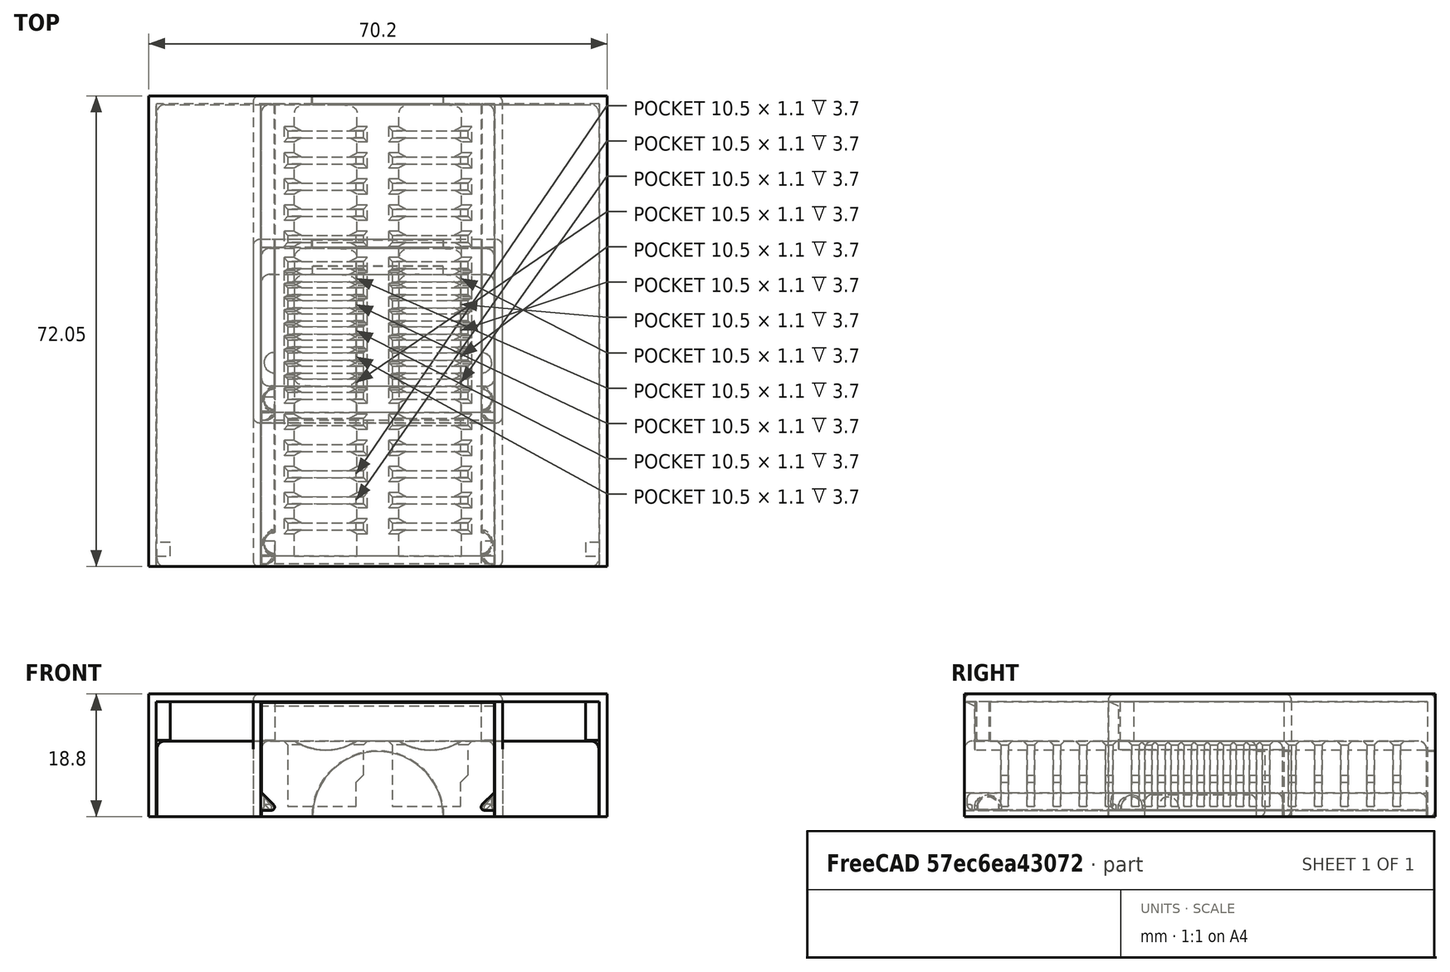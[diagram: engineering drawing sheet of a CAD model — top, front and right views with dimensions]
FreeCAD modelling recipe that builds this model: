
FCSTD DOCUMENT  (FreeCAD 1.0R39109 (Git))
Label: MicroSDHolder
License: All rights reserved
LicenseURL: http://en.wikipedia.org/wiki/All_rights_reserved
objects: Sketcher::SketchObject×55, PartDesign::Pad×27, PartDesign::Pocket×18, PartDesign::Fillet×16, PartDesign::Chamfer×7, PartDesign::Body×7, PartDesign::SubShapeBinder×6, PartDesign::Plane×4, PartDesign::LinearPattern×4, App::Part×3, PartDesign::ShapeBinder×2, Spreadsheet::Sheet×1
note: 341 computed .brp shape members not serialized (recipe doc carries the construction recipe); baked Part::Feature solids carry a one-line shape summary decoded from their .brp

FEATURE [Spreadsheet::Sheet] Spreadsheet
  cells = B3='Tolerance; C3(Tolerance)==0.1 mm; B4='BaseHeight; C4(BaseHeight)==SDOffset + SDHeight - SDFree; B5='WallThickness; C5(WallThickness)==1.2 mm; B6='BackWallThickness; C6(BackWallThickness)==1.6 mm; B7='SDHoleWidth; C7(SDHoleWidth)==11.6 mm; B8='SDHoleWidthSrinkage; C8(SDHoleWidthSrinkage)==1 mm; B9='SDHoleThickness; C9(SDHoleThickness)==1.1 mm; B10='SDHeight; C10(SDHeight)==15 mm; B11='SDFree; C11(SDFree)==5 mm; B12='SDOffset; C12(SDOffset)==1.6 mm; B13='SpacingX; C13(SpacingX)==16 mm; B14='SpacingY; C14(SpacingY)==4 mm; B15='Margin; C15(Margin)==4 mm; B16='Columns_4; C16(Columns_4)=4; B17='Columns_2; C17(Columns_2)=2; B18='Rows; C18(Rows)=16; B19='Rows_short; C19(Rows_short)=5; B20='Rows_test; C20(Rows_test)=3; B21='RidgeDepth; C21(RidgeDepth)==2 mm; B22='RidgeOffset; C22(RidgeOffset)==1 mm; B23='LockRadius; C23(LockRadius)==1.6 mm
FEATURE [Sketcher::SketchObject] Sketch  label="Template_XY"
  ArcFitTolerance = 0
  AttachmentSupport = -> [XY_Plane]
  FullyConstrained = true
  MakeInternals = false
  MapMode = 5
  expr: .Constraints.BaseLength = <<Spreadsheet>>.SpacingY * (<<Spreadsheet>>.Rows - 1) + <<Spreadsheet>>.SDHoleThickness + 2 * <<Spreadsheet>>.Margin
  expr: .Constraints.Width = <<Spreadsheet>>.SpacingX * (<<Spreadsheet>>.Columns_4 - 1) + <<Spreadsheet>>.SDHoleWidth + 2 * <<Spreadsheet>>.Margin
  expr: Constraints[42] = <<Spreadsheet>>.LockRadius
  expr: Constraints[43] = <<Spreadsheet>>.LockRadius + <<Spreadsheet>>.Tolerance
  expr: Constraints[55] = <<Spreadsheet>>.Tolerance * 1.5
  expr: Constraints[59] = <<Spreadsheet>>.BackWallThickness
  expr: Constraints[64] = <<Spreadsheet>>.RidgeDepth
  expr: Constraints[67] = <<Spreadsheet>>.Tolerance
  sketch-geometry (22):
    g0: LineSegment StartX=33.8 StartY=34.55 StartZ=0 EndX=33.8 EndY=-36.15 EndZ=0
    g1: LineSegment StartX=33.8 StartY=-36.15 StartZ=0 EndX=-33.8 EndY=-36.15 EndZ=0
    g2: LineSegment StartX=-33.8 StartY=-36.15 StartZ=0 EndX=-33.8 EndY=34.55 EndZ=0
    g3: LineSegment StartX=-33.8 StartY=-6.2e-15 StartZ=0 EndX=33.8 EndY=-6.2e-15 EndZ=0
    g4: LineSegment StartX=-2.3e-15 StartY=34.55 StartZ=0 EndX=-2.3e-15 EndY=-36.15 EndZ=0
    g5: LineSegment StartX=-33.8 StartY=34.55 StartZ=0 EndX=-31.8 EndY=34.55 EndZ=0
    g6: LineSegment StartX=-31.8 StartY=34.55 StartZ=0 EndX=31.8 EndY=34.55 EndZ=0
    g7: ArcOfCircle CenterX=-31.8 CenterY=-32.55 CenterZ=0 NormalX=0 NormalY=0 NormalZ=1 AngleXU=0 Radius=1.6 StartAngle=1.5708 EndAngle=4.71239
    g8: LineSegment StartX=-31.8 StartY=-36.15 StartZ=0 EndX=-31.8 EndY=34.55 EndZ=0
    g9: ArcOfCircle CenterX=-31.8 CenterY=-32.55 CenterZ=0 NormalX=0 NormalY=0 NormalZ=1 AngleXU=0 Radius=1.7 StartAngle=1.5708 EndAngle=4.71239
    g10: LineSegment StartX=31.8 StartY=34.55 StartZ=0 EndX=31.8 EndY=-36.15 EndZ=0
    g11: ArcOfCircle CenterX=31.8 CenterY=-32.55 CenterZ=0 NormalX=0 NormalY=0 NormalZ=1 AngleXU=0 Radius=1.6 StartAngle=4.71239 EndAngle=7.85398
    g12: ArcOfCircle CenterX=31.8 CenterY=-32.55 CenterZ=0 NormalX=0 NormalY=0 NormalZ=1 AngleXU=0 Radius=1.7 StartAngle=4.71239 EndAngle=7.85398
    g13: LineSegment [constr] StartX=-31.8 StartY=-32.55 StartZ=0 EndX=31.8 EndY=-32.55 EndZ=0
    g14: LineSegment StartX=31.8 StartY=34.55 StartZ=0 EndX=33.8 EndY=34.55 EndZ=0
    g15: LineSegment StartX=-33.9 StartY=-36.15 StartZ=0 EndX=-33.9 EndY=34.7 EndZ=0
    g16: LineSegment StartX=-33.9 StartY=34.7 StartZ=0 EndX=33.9 EndY=34.7 EndZ=0
    g17: LineSegment StartX=33.9 StartY=34.7 StartZ=0 EndX=33.9 EndY=-36.15 EndZ=0
    g18: LineSegment [constr] StartX=33.8 StartY=-36.15 StartZ=0 EndX=33.9 EndY=-36.15 EndZ=0
    g19: LineSegment [constr] StartX=33.8 StartY=34.55 StartZ=0 EndX=33.8 EndY=34.7 EndZ=0
    g20: LineSegment StartX=-33.8 StartY=-34.55 StartZ=0 EndX=33.8 EndY=-34.55 EndZ=0
    g21: LineSegment [constr] StartX=-33.8 StartY=-36.15 StartZ=0 EndX=-33.9 EndY=-36.15 EndZ=0
  constraints (70):
    c: Coincident(g0,g1)
    c: Coincident(g1,g2)
    c: Coincident(g2,g5)
    c: Horizontal(g1)
    c: Vertical(g0)
    c: Vertical(g2)
    c: DistanceX(g5,g0) = 67.6  'Width'
    c: PointOnObject(g3,g2)
    c: PointOnObject(g3,g0)
    c: PointOnObject(g4,g1)
    c: Symmetric(g1,g0,g4)
    c: Coincident(g5,g6)
    c: Horizontal(g5)
    c: PointOnObject(g4,g6)
    c: Coincident(g8,g5)
    c: Vertical(g8)
    c: PointOnObject(g7,g8)
    c: PointOnObject(g7,g8)
    c: Coincident(g9,g7)
    c: PointOnObject(g9,g8)
    c: Vertical(g10)
    c: PointOnObject(g11,g10)
    c: PointOnObject(g11,g10)
    c: Coincident(g12,g11)
    c: PointOnObject(g12,g10)
    c: Equal(g7,g11)
    c: Equal(g12,g9)
    c: PointOnObject(g8,g1)
    c: PointOnObject(g9,g8)
    c: PointOnObject(g7,g8)
    c: DistanceY(g8,g7) = 2
    c: PointOnObject(g10,g1)
    c: PointOnObject(g12,g10)
    c: PointOnObject(g11,g10)
    c: Coincident(g13,g7)
    c: Coincident(g13,g11)
    c: Horizontal(g13)
    c: Coincident(g6,g10)
    c: Coincident(g14,g6)
    c: Coincident(g14,g0)
    c: Horizontal(g14)
    c: Symmetric(g5,g6,g4)
    c: Radius(g7) = 1.6
    c: Radius(g9) = 1.7
    c: Vertical(g15)
    c: Coincident(g15,g16)
    c: Horizontal(g16)
    c: Coincident(g16,g17)
    c: Vertical(g17)
    c: PointOnObject(g17,g1)
    c: Coincident(g18,g0)
    c: PointOnObject(g15,g1)
    c: Coincident(g19,g0)
    c: PointOnObject(g19,g16)
    c: Vertical(g19)
    c: DistanceY(g19,g19) = 0.15
    c: DistanceY(g15,g15) = 70.85  'CoverLength'
    c: PointOnObject(g20,g2)
    c: Horizontal(g20)
    c: DistanceY(g1,g20) = 1.6
    c: Symmetric(g20,g0,g-1)  '__ANCHOR__'
    c: DistanceY(g20,g2) = 69.1  'BaseLength'
    c: Symmetric(g20,g0,g3)
    c: Horizontal(g3)
    c: DistanceX(g1,g8) = 2
    c: Coincident(g21,g1)
    c: Coincident(g21,g15)
    c: DistanceX(g21,g21) = 0.1
    c: Equal(g18,g21)
    c: Coincident(g18,g17)
FEATURE [Sketcher::SketchObject] Sketch001  label="Template_SD"
  ArcFitTolerance = 0
  AttachmentSupport = -> [XZ_Plane]
  ExternalGeometry = -> [Sketch]
  FullyConstrained = true
  MakeInternals = false
  MapMode = 5
  Placement = pos=(0,0,0) rot=(1,0,0;1.5708rad)
  expr: Constraints[70] = <<Spreadsheet>>.SDHeight
  expr: Constraints[71] = <<Spreadsheet>>.SDHoleWidth
  expr: Constraints[74] = <<Spreadsheet>>.SDHoleWidthSrinkage
  expr: Constraints[75] = <<Spreadsheet>>.SDOffset
  expr: Constraints[80] = <<Spreadsheet>>.SDFree
  expr: Constraints[81] = <<Spreadsheet>>.SpacingX
  sketch-geometry (30):
    g0: LineSegment StartX=-13.8 StartY=1.6 StartZ=0 EndX=-13.8 EndY=16.6 EndZ=0
    g1: LineSegment StartX=-13.8 StartY=16.6 StartZ=0 EndX=-2.2 EndY=16.6 EndZ=0
    g2: LineSegment StartX=-2.2 StartY=16.6 StartZ=0 EndX=-2.2 EndY=6.4 EndZ=0
    g3: LineSegment StartX=-3.2 StartY=1.6 StartZ=0 EndX=-13.8 EndY=1.6 EndZ=0
    g4: LineSegment StartX=-3.2 StartY=1.6 StartZ=0 EndX=-3.2 EndY=5.4 EndZ=0
    g5: LineSegment StartX=-3.2 StartY=5.4 StartZ=0 EndX=-2.2 EndY=6.4 EndZ=0
    g6: GeomPoint [constr] X=-1.105e-13 Y=0 Z=0
    g7: LineSegment [constr] StartX=-2.2 StartY=16.6 StartZ=0 EndX=2.2 EndY=16.6 EndZ=0
    g8: LineSegment [constr] StartX=13.8 StartY=16.6 StartZ=0 EndX=18.2 EndY=16.6 EndZ=0
    g9: LineSegment [constr] StartX=-13.8 StartY=16.6 StartZ=0 EndX=-18.2 EndY=16.6 EndZ=0
    g10: LineSegment StartX=2.2 StartY=16.6 StartZ=0 EndX=2.2 EndY=1.6 EndZ=0
    g11: LineSegment StartX=2.2 StartY=1.6 StartZ=0 EndX=12.8 EndY=1.6 EndZ=0
    g12: LineSegment StartX=12.8 StartY=1.6 StartZ=0 EndX=12.8 EndY=5.4 EndZ=0
    g13: LineSegment StartX=12.8 StartY=5.4 StartZ=0 EndX=13.8 EndY=6.4 EndZ=0
    g14: LineSegment StartX=13.8 StartY=6.4 StartZ=0 EndX=13.8 EndY=16.6 EndZ=0
    g15: LineSegment StartX=13.8 StartY=16.6 StartZ=0 EndX=2.2 EndY=16.6 EndZ=0
    g16: LineSegment StartX=18.2 StartY=16.6 StartZ=0 EndX=29.8 EndY=16.6 EndZ=0
    g17: LineSegment StartX=29.8 StartY=16.6 StartZ=0 EndX=29.8 EndY=6.4 EndZ=0
    g18: LineSegment StartX=29.8 StartY=6.4 StartZ=0 EndX=28.8 EndY=5.4 EndZ=0
    g19: LineSegment StartX=28.8 StartY=5.4 StartZ=0 EndX=28.8 EndY=1.6 EndZ=0
    g20: LineSegment StartX=28.8 StartY=1.6 StartZ=0 EndX=18.2 EndY=1.6 EndZ=0
    g21: LineSegment StartX=18.2 StartY=1.6 StartZ=0 EndX=18.2 EndY=16.6 EndZ=0
    g22: LineSegment StartX=-18.2 StartY=16.6 StartZ=0 EndX=-18.2 EndY=6.4 EndZ=0
    g23: LineSegment StartX=-18.2 StartY=6.4 StartZ=0 EndX=-19.2 EndY=5.4 EndZ=0
    g24: LineSegment StartX=-19.2 StartY=5.4 StartZ=0 EndX=-19.2 EndY=1.6 EndZ=0
    g25: LineSegment StartX=-19.2 StartY=1.6 StartZ=0 EndX=-29.8 EndY=1.6 EndZ=0
    g26: LineSegment StartX=-29.8 StartY=1.6 StartZ=0 EndX=-29.8 EndY=16.6 EndZ=0
    g27: LineSegment StartX=-29.8 StartY=16.6 StartZ=0 EndX=-18.2 EndY=16.6 EndZ=0
    g28: LineSegment StartX=-29.8 StartY=11.6 StartZ=0 EndX=29.8 EndY=11.6 EndZ=0
    g29: LineSegment [constr] StartX=-2.3e-15 StartY=16.6 StartZ=0 EndX=-2.3e-15 EndY=0 EndZ=0
  constraints (85):
    c: Coincident(g3,g0)
    c: Coincident(g0,g1)
    c: Coincident(g1,g2)
    c: Horizontal(g1)
    c: Vertical(g0)
    c: Vertical(g2)
    c: Horizontal(g3)
    c: Vertical(g4)
    c: Coincident(g5,g4)
    c: Coincident(g2,g5)
    c: Coincident(g7,g1)
    c: Horizontal(g7)
    c: Horizontal(g8)
    c: Horizontal(g9)
    c: Equal(g9,g7)
    c: Equal(g7,g8)
    c: Coincident(g7,g10)
    c: Vertical(g10)
    c: Coincident(g10,g11)
    c: Horizontal(g11)
    c: Coincident(g11,g12)
    c: Vertical(g12)
    c: Coincident(g12,g13)
    c: Coincident(g13,g14)
    c: Coincident(g14,g8)
    c: Vertical(g14)
    c: Coincident(g14,g15)
    c: Coincident(g15,g10)
    c: Horizontal(g15)
    c: Coincident(g8,g16)
    c: Horizontal(g16)
    c: Coincident(g16,g17)
    c: Vertical(g17)
    c: Coincident(g17,g18)
    c: Coincident(g18,g19)
    c: Vertical(g19)
    c: Coincident(g19,g20)
    c: Horizontal(g20)
    c: Coincident(g20,g21)
    c: Coincident(g21,g16)
    c: Vertical(g21)
    c: Coincident(g9,g0)
    c: Coincident(g9,g22)
    c: Vertical(g22)
    c: Coincident(g22,g23)
    c: Coincident(g23,g24)
    c: Vertical(g24)
    c: Coincident(g24,g25)
    c: Horizontal(g25)
    c: Coincident(g25,g26)
    c: Vertical(g26)
    c: Coincident(g26,g27)
    c: Coincident(g27,g22)
    c: Horizontal(g27)
    c: Equal(g27,g1)
    c: Equal(g1,g15)
    c: Equal(g15,g16)
    c: Equal(g26,g0)
    c: Equal(g0,g10)
    c: Equal(g10,g21)
    c: Equal(g22,g2)
    c: Equal(g2,g14)
    c: Equal(g14,g17)
    c: Equal(g25,g3)
    c: Equal(g3,g11)
    c: Equal(g11,g20)
    c: Equal(g24,g4)
    c: Equal(g4,g12)
    c: Equal(g12,g19)
    c: Coincident(g6,g-1)  '__ANCHOR__'
    c: DistanceY(g26,g26) = 15
    c: DistanceX(g27,g27) = 11.6
    c: Angle(g22,g23) = 2.35619
    c: DistanceY(g24,g22) = 4.8
    c: DistanceX(g24,g22) = 1
    c: DistanceY(g6,g3) = 1.6
    c: Coincident(g3,g4)
    c: PointOnObject(g28,g26)
    c: PointOnObject(g28,g17)
    c: Horizontal(g28)
    c: DistanceY(g28,g26) = 5
    c: DistanceX(g26,g0) = 16
    c: PointOnObject(g29,g7)
    c: Coincident(g-3,g29)
    c: Symmetric(g1,g10,g29)
FEATURE [Sketcher::SketchObject] Sketch002  label="MSHB_Foundation"
  ArcFitTolerance = 0
  AttachmentSupport = -> [XY_Plane]
  ExternalGeometry = -> [Sketch]
  FullyConstrained = true
  MakeInternals = false
  MapMode = 5
  sketch-geometry (4):
    g0: LineSegment StartX=33.8 StartY=34.55 StartZ=0 EndX=33.8 EndY=-36.15 EndZ=0
    g1: LineSegment StartX=33.8 StartY=-36.15 StartZ=0 EndX=-33.8 EndY=-36.15 EndZ=0
    g2: LineSegment StartX=-33.8 StartY=-36.15 StartZ=0 EndX=-33.8 EndY=34.55 EndZ=0
    g3: LineSegment StartX=-33.8 StartY=34.55 StartZ=0 EndX=33.8 EndY=34.55 EndZ=0
  constraints (8):
    c: Coincident(g0,g1)
    c: Coincident(g1,g2)
    c: Coincident(g2,g3)
    c: Coincident(g3,g0)
    c: Coincident(g0,g-4)
    c: Coincident(g0,g-4)
    c: Coincident(g2,g-3)
    c: Coincident(g1,g-3)
FEATURE [PartDesign::Pad] Pad  label="MSHB_Foundation_"
  Direction = (0,0,1)
  Length = 11.6
  Length2 = 10
  Profile = -> Sketch002
  ReferenceAxis = -> Sketch002 [N_Axis]
  Suppressed = false
  Type = 0
  expr: Length = <<Spreadsheet>>.BaseHeight
FEATURE [Sketcher::SketchObject] Sketch003  label="MSHB_SDHoles"
  ArcFitTolerance = 0
  AttachmentOffset = pos=(0,0,30.55) rot=(0,0,1;0rad)
  AttachmentSupport = -> [XZ_Plane]
  ExternalGeometry = -> [Sketch001]
  FullyConstrained = true
  MakeInternals = false
  MapMode = 5
  Placement = pos=(0,-30.55,6.8e-15) rot=(1,0,0;1.5708rad)
  expr: .AttachmentOffset.Base.z = Sketch.Constraints.BaseLength / 2 - <<Spreadsheet>>.Margin
  sketch-geometry (24):
    g0: LineSegment StartX=-29.8 StartY=16.6 StartZ=0 EndX=-18.2 EndY=16.6 EndZ=0
    g1: LineSegment StartX=-18.2 StartY=16.6 StartZ=0 EndX=-18.2 EndY=6.4 EndZ=0
    g2: LineSegment StartX=-18.2 StartY=6.4 StartZ=0 EndX=-19.2 EndY=5.4 EndZ=0
    g3: LineSegment StartX=-19.2 StartY=5.4 StartZ=0 EndX=-19.2 EndY=1.6 EndZ=0
    g4: LineSegment StartX=-19.2 StartY=1.6 StartZ=0 EndX=-29.8 EndY=1.6 EndZ=0
    g5: LineSegment StartX=-29.8 StartY=1.6 StartZ=0 EndX=-29.8 EndY=16.6 EndZ=0
    g6: LineSegment StartX=-13.8 StartY=16.6 StartZ=0 EndX=-2.2 EndY=16.6 EndZ=0
    g7: LineSegment StartX=-2.2 StartY=16.6 StartZ=0 EndX=-2.2 EndY=6.4 EndZ=0
    g8: LineSegment StartX=-2.2 StartY=6.4 StartZ=0 EndX=-3.2 EndY=5.4 EndZ=0
    g9: LineSegment StartX=-3.2 StartY=5.4 StartZ=0 EndX=-3.2 EndY=1.6 EndZ=0
    g10: LineSegment StartX=-3.2 StartY=1.6 StartZ=0 EndX=-13.8 EndY=1.6 EndZ=0
    g11: LineSegment StartX=-13.8 StartY=1.6 StartZ=0 EndX=-13.8 EndY=16.6 EndZ=0
    g12: LineSegment StartX=2.2 StartY=16.6 StartZ=0 EndX=13.8 EndY=16.6 EndZ=0
    g13: LineSegment StartX=13.8 StartY=16.6 StartZ=0 EndX=13.8 EndY=6.4 EndZ=0
    g14: LineSegment StartX=13.8 StartY=6.4 StartZ=0 EndX=12.8 EndY=5.4 EndZ=0
    g15: LineSegment StartX=12.8 StartY=5.4 StartZ=0 EndX=12.8 EndY=1.6 EndZ=0
    g16: LineSegment StartX=12.8 StartY=1.6 StartZ=0 EndX=2.2 EndY=1.6 EndZ=0
    g17: LineSegment StartX=2.2 StartY=1.6 StartZ=0 EndX=2.2 EndY=16.6 EndZ=0
    g18: LineSegment StartX=18.2 StartY=16.6 StartZ=0 EndX=29.8 EndY=16.6 EndZ=0
    g19: LineSegment StartX=29.8 StartY=16.6 StartZ=0 EndX=29.8 EndY=6.4 EndZ=0
    g20: LineSegment StartX=29.8 StartY=6.4 StartZ=0 EndX=28.8 EndY=5.4 EndZ=0
    g21: LineSegment StartX=28.8 StartY=5.4 StartZ=0 EndX=28.8 EndY=1.6 EndZ=0
    g22: LineSegment StartX=28.8 StartY=1.6 StartZ=0 EndX=18.2 EndY=1.6 EndZ=0
    g23: LineSegment StartX=18.2 StartY=1.6 StartZ=0 EndX=18.2 EndY=16.6 EndZ=0
  constraints (48):
    c: Coincident(g-3,g0)
    c: Coincident(g0,g-4)
    c: Coincident(g0,g1)
    c: Coincident(g1,g-4)
    c: Coincident(g1,g2)
    c: Coincident(g2,g-5)
    c: Coincident(g2,g3)
    c: Coincident(g3,g-5)
    c: Coincident(g3,g4)
    c: Coincident(g4,g-3)
    c: Coincident(g4,g5)
    c: Coincident(g5,g0)
    c: Coincident(g-6,g6)
    c: Coincident(g6,g-7)
    c: Coincident(g6,g7)
    c: Coincident(g7,g-7)
    c: Coincident(g7,g8)
    c: Coincident(g8,g-8)
    c: Coincident(g8,g9)
    c: Coincident(g9,g-8)
    c: Coincident(g9,g10)
    c: Coincident(g10,g-6)
    c: Coincident(g10,g11)
    c: Coincident(g11,g6)
    c: Coincident(g-9,g12)
    c: Coincident(g12,g-10)
    c: Coincident(g12,g13)
    c: Coincident(g13,g-10)
    c: Coincident(g13,g14)
    c: Coincident(g14,g-11)
    c: Coincident(g14,g15)
    c: Coincident(g15,g-11)
    c: Coincident(g15,g16)
    c: Coincident(g16,g-9)
    c: Coincident(g16,g17)
    c: Coincident(g12,g17)
    c: Coincident(g-12,g18)
    c: Coincident(g18,g-13)
    c: Coincident(g18,g19)
    c: Coincident(g19,g-13)
    c: Coincident(g19,g20)
    c: Coincident(g20,g-14)
    c: Coincident(g20,g21)
    c: Coincident(g21,g-14)
    c: Coincident(g21,g22)
    c: Coincident(g22,g-12)
    c: Coincident(g22,g23)
    c: Coincident(g23,g18)
FEATURE [Sketcher::SketchObject] Sketch006  label="MSHB_Lock"
  ArcFitTolerance = 0
  AttachmentOffset = pos=(0,0,1) rot=(0,0,1;0rad)
  AttachmentSupport = -> [XY_Plane]
  ExternalGeometry = -> [Sketch]
  FullyConstrained = true
  MakeInternals = false
  MapMode = 5
  Placement = pos=(0,0,1) rot=(0,0,1;0rad)
  expr: .AttachmentOffset.Base.z = <<Spreadsheet>>.RidgeOffset
  sketch-geometry (4):
    g0: ArcOfCircle CenterX=-31.8 CenterY=-32.55 CenterZ=0 NormalX=0 NormalY=0 NormalZ=1 AngleXU=0 Radius=1.6 StartAngle=1.5708 EndAngle=4.71239
    g1: ArcOfCircle CenterX=31.8 CenterY=-32.55 CenterZ=0 NormalX=0 NormalY=0 NormalZ=1 AngleXU=0 Radius=1.6 StartAngle=4.71239 EndAngle=7.85398
    g2: LineSegment StartX=31.8 StartY=-30.95 StartZ=0 EndX=31.8 EndY=-34.15 EndZ=0
    g3: LineSegment StartX=-31.8 StartY=-30.95 StartZ=0 EndX=-31.8 EndY=-34.15 EndZ=0
  constraints (10):
    c: Coincident(g2,g1)
    c: Coincident(g2,g1)
    c: Coincident(g3,g0)
    c: Coincident(g3,g0)
    c: Coincident(g1,g-4)
    c: Coincident(g1,g-4)
    c: Equal(g1,g-4)
    c: Coincident(g0,g-3)
    c: Coincident(g0,g-3)
    c: Equal(g0,g-3)
FEATURE [Sketcher::SketchObject] Sketch011  label="Template_XZ"
  ArcFitTolerance = 0
  AttachmentSupport = -> [XZ_Plane]
  FullyConstrained = true
  MakeInternals = false
  MapMode = 5
  Placement = pos=(0,0,0) rot=(1,0,0;1.5708rad)
  expr: Constraints[12] = <<Spreadsheet>>.Tolerance
  expr: Constraints[26] = <<Spreadsheet>>.RidgeOffset
  expr: Constraints[40] = <<Spreadsheet>>.RidgeDepth
  expr: Constraints[48] = <<Spreadsheet>>.SDOffset + <<Spreadsheet>>.SDHeight + 1 mm
  expr: Constraints[6] = Sketch.Constraints.Width
  expr: Constraints[73] = <<Spreadsheet>>.SDFree + 1 mm
  sketch-geometry (28):
    g0: LineSegment StartX=-33.8 StartY=0 StartZ=0 EndX=33.8 EndY=0 EndZ=0
    g1: LineSegment StartX=33.8 StartY=11.6 StartZ=0 EndX=-33.8 EndY=11.6 EndZ=0
    g2: LineSegment [constr] StartX=-33.8 StartY=0 StartZ=0 EndX=-33.9 EndY=0 EndZ=0
    g3: LineSegment [constr] StartX=33.8 StartY=0 StartZ=0 EndX=33.9 EndY=0 EndZ=0
    g4: LineSegment StartX=-33.8 StartY=1 StartZ=0 EndX=-33.8 EndY=0 EndZ=0
    g5: LineSegment StartX=-33.8 StartY=3 StartZ=0 EndX=-33.8 EndY=1 EndZ=0
    g6: LineSegment StartX=-33.8 StartY=11.6 StartZ=0 EndX=-33.8 EndY=5 EndZ=0
    g7: LineSegment StartX=-33.8 StartY=5 StartZ=0 EndX=-33.8 EndY=3 EndZ=0
    g8: LineSegment StartX=-33.8 StartY=1 StartZ=0 EndX=-31.8 EndY=3 EndZ=0
    g9: LineSegment StartX=-31.8 StartY=3 StartZ=0 EndX=-33.8 EndY=5 EndZ=0
    g10: LineSegment [constr] StartX=-31.8 StartY=3 StartZ=0 EndX=-33.8 EndY=3 EndZ=0
    g11: LineSegment StartX=33.8 StartY=0 StartZ=0 EndX=33.8 EndY=1 EndZ=0
    g12: LineSegment StartX=33.8 StartY=1 StartZ=0 EndX=33.8 EndY=11.6 EndZ=0
    g13: LineSegment StartX=33.8 StartY=1 StartZ=0 EndX=31.8 EndY=3 EndZ=0
    g14: LineSegment StartX=31.8 StartY=3 StartZ=0 EndX=33.8 EndY=5 EndZ=0
    g15: LineSegment [constr] StartX=31.8 StartY=3 StartZ=0 EndX=33.8 EndY=3 EndZ=0
    g16: LineSegment StartX=-33.9 StartY=17.6 StartZ=0 EndX=33.9 EndY=17.6 EndZ=0
    g17: LineSegment StartX=-33.9 StartY=1.04142 StartZ=0 EndX=-31.9414 EndY=3 EndZ=0
    g18: LineSegment StartX=-31.9414 StartY=3 StartZ=0 EndX=-33.9 EndY=4.95858 EndZ=0
    g19: LineSegment [constr] StartX=-33.8 StartY=5 StartZ=0 EndX=-33.8707 EndY=4.92929 EndZ=0
    g20: LineSegment [constr] StartX=-33.8 StartY=1 StartZ=0 EndX=-33.8707 EndY=1.07071 EndZ=0
    g21: LineSegment StartX=33.9 StartY=4.95858 StartZ=0 EndX=31.9414 EndY=3 EndZ=0
    g22: LineSegment StartX=31.9414 StartY=3 StartZ=0 EndX=33.9 EndY=1.04142 EndZ=0
    g23: LineSegment StartX=-33.9 StartY=0 StartZ=0 EndX=-33.9 EndY=1.04142 EndZ=0
    g24: LineSegment StartX=-33.9 StartY=1.04142 StartZ=0 EndX=-33.9 EndY=17.6 EndZ=0
    g25: LineSegment StartX=33.9 StartY=17.6 StartZ=0 EndX=33.9 EndY=1.04142 EndZ=0
    g26: LineSegment StartX=33.9 StartY=1.04142 StartZ=0 EndX=33.9 EndY=0 EndZ=0
    g27: ArcOfCircle CenterX=0 CenterY=0 CenterZ=0 NormalX=0 NormalY=0 NormalZ=1 AngleXU=0 Radius=10 StartAngle=0 EndAngle=3.14159
  constraints (81):
    c: Coincident(g0,g11)
    c: Coincident(g12,g1)
    c: Coincident(g1,g6)
    c: Coincident(g4,g0)
    c: Horizontal(g0)
    c: Horizontal(g1)
    c: DistanceX(g1,g1) = 67.6
    c: Coincident(g2,g0)
    c: Horizontal(g2)
    c: Coincident(g3,g0)
    c: Horizontal(g3)
    c: Equal(g3,g2)
    c: DistanceX(g2,g2) = 0.1
    c: Coincident(g5,g4)
    c: Vertical(g4)
    c: Coincident(g7,g5)
    c: Vertical(g5)
    c: Coincident(g6,g7)
    c: Vertical(g6)
    c: Vertical(g7)
    c: Coincident(g8,g4)
    c: Coincident(g9,g6)
    c: Coincident(g10,g5)
    c: Horizontal(g10)
    c: Equal(g10,g7)
    c: Equal(g7,g5)
    c: DistanceY(g4,g4) = 1
    c: Coincident(g11,g12)
    c: Vertical(g11)
    c: Vertical(g12)
    c: Equal(g4,g11)
    c: Coincident(g11,g13)
    c: Coincident(g13,g14)
    c: PointOnObject(g14,g12)
    c: Coincident(g13,g15)
    c: PointOnObject(g15,g12)
    c: Horizontal(g15)
    c: Equal(g14,g13)
    c: Equal(g13,g8)
    c: Equal(g10,g15)
    c: DistanceX(g6,g8) = 2
    c: Coincident(g8,g9)
    c: Coincident(g8,g10)
    c: Coincident(g2,g23)
    c: Coincident(g24,g16)
    c: Horizontal(g16)
    c: Coincident(g16,g25)
    c: Coincident(g26,g3)
    c: DistanceY(g23,g24) = 17.6
    c: PointOnObject(g17,g10)
    c: Coincident(g18,g17)
    c: Coincident(g19,g6)
    c: PointOnObject(g19,g18)
    c: Coincident(g20,g4)
    c: PointOnObject(g20,g17)
    c: Perpendicular(g20,g17)
    c: Perpendicular(g9,g19)
    c: Equal(g2,g20)
    c: PointOnObject(g21,g15)
    c: Coincident(g21,g22)
    c: Equal(g21,g22)
    c: Equal(g22,g17)
    c: Coincident(g23,g24)
    c: Vertical(g23)
    c: Vertical(g24)
    c: PointOnObject(g18,g24)
    c: Coincident(g23,g17)
    c: Coincident(g25,g26)
    c: Vertical(g25)
    c: Vertical(g26)
    c: PointOnObject(g21,g25)
    c: Coincident(g22,g25)
    c: Equal(g26,g23)
    c: DistanceY(g1,g16) = 6
    c: Parallel(g17,g8)
    c: Parallel(g18,g9)
    c: PointOnObject(g27,g0)
    c: PointOnObject(g27,g0)
    c: Radius(g27) = 10
    c: Symmetric(g0,g0,g27)
    c: Coincident(g27,g-1)  '__ANCHOR__'
FEATURE [Sketcher::SketchObject] Sketch004  label="MSHB_BackWall"
  ArcFitTolerance = 0
  AttachmentOffset = pos=(0,0,34.55) rot=(0,0,1;0rad)
  AttachmentSupport = -> [XZ_Plane]
  ExternalGeometry = -> [Sketch011]
  FullyConstrained = true
  MakeInternals = false
  MapMode = 5
  Placement = pos=(0,-34.55,7.7e-15) rot=(1,0,0;1.5708rad)
  expr: .AttachmentOffset.Base.z = Sketch.Constraints.BaseLength / 2
  expr: Constraints[9] = <<Spreadsheet>>.Tolerance
  sketch-geometry (4):
    g0: LineSegment StartX=-33.8 StartY=0 StartZ=0 EndX=33.8 EndY=0 EndZ=0
    g1: LineSegment StartX=33.8 StartY=0 StartZ=0 EndX=33.8 EndY=17.5 EndZ=0
    g2: LineSegment StartX=33.8 StartY=17.5 StartZ=0 EndX=-33.8 EndY=17.5 EndZ=0
    g3: LineSegment StartX=-33.8 StartY=17.5 StartZ=0 EndX=-33.8 EndY=0 EndZ=0
  constraints (10):
    c: Coincident(g0,g1)
    c: Coincident(g1,g2)
    c: Coincident(g2,g3)
    c: Coincident(g3,g0)
    c: Horizontal(g2)
    c: Vertical(g1)
    c: Vertical(g3)
    c: Coincident(g0,g-3)
    c: Coincident(g0,g-3)
    c: DistanceY(g1,g-4) = 0.1
FEATURE [Sketcher::SketchObject] Sketch005  label="MSHB_Ridge"
  ArcFitTolerance = 0
  AttachmentSupport = -> [XZ_Plane]
  ExternalGeometry = -> [Sketch011]
  FullyConstrained = true
  MakeInternals = false
  MapMode = 5
  Placement = pos=(0,0,0) rot=(1,0,0;1.5708rad)
  sketch-geometry (6):
    g0: LineSegment StartX=-33.8 StartY=1 StartZ=0 EndX=-31.8 EndY=3 EndZ=0
    g1: LineSegment StartX=-31.8 StartY=3 StartZ=0 EndX=-33.8 EndY=5 EndZ=0
    g2: LineSegment StartX=-33.8 StartY=5 StartZ=0 EndX=-33.8 EndY=1 EndZ=0
    g3: LineSegment StartX=33.8 StartY=5 StartZ=0 EndX=31.8 EndY=3 EndZ=0
    g4: LineSegment StartX=31.8 StartY=3 StartZ=0 EndX=33.8 EndY=1 EndZ=0
    g5: LineSegment StartX=33.8 StartY=1 StartZ=0 EndX=33.8 EndY=5 EndZ=0
  constraints (12):
    c: Coincident(g-4,g0)
    c: Coincident(g0,g-4)
    c: Coincident(g0,g1)
    c: Coincident(g1,g-3)
    c: Coincident(g1,g2)
    c: Coincident(g2,g0)
    c: Coincident(g-5,g3)
    c: Coincident(g3,g-6)
    c: Coincident(g3,g4)
    c: Coincident(g4,g-6)
    c: Coincident(g4,g5)
    c: Coincident(g5,g3)
FEATURE [PartDesign::SubShapeBinder] Binder
  BindCopyOnChange = 0
  BindMode = 0
  ClaimChildren = false
  Context = -> Part [Body002.Binder.]
  Fuse = false
  MakeFace = true
  OffsetFill = false
  OffsetIntersection = false
  OffsetJoinType = 0
  OffsetOpenResult = false
  PartialLoad = false
  Relative = true
  Support = -> [Body[Sketch.]]
  _Version = 2
FEATURE [PartDesign::SubShapeBinder] Binder001
  BindCopyOnChange = 0
  BindMode = 0
  ClaimChildren = false
  Context = -> Part [Body002.Binder001.]
  Fuse = false
  MakeFace = true
  OffsetFill = false
  OffsetIntersection = false
  OffsetJoinType = 0
  OffsetOpenResult = false
  PartialLoad = false
  Relative = true
  Support = -> [Body[Sketch011.]]
  _Version = 2
FEATURE [Sketcher::SketchObject] Sketch012
  ArcFitTolerance = 0
  AttachmentSupport = -> [XY_Plane002]
  ExternalGeometry = -> [Binder]
  FullyConstrained = true
  MakeInternals = false
  MapMode = 5
  sketch-geometry (4):
    g0: LineSegment StartX=-33.9 StartY=34.7 StartZ=0 EndX=33.9 EndY=34.7 EndZ=0
    g1: LineSegment StartX=33.9 StartY=34.7 StartZ=0 EndX=33.9 EndY=-36.15 EndZ=0
    g2: LineSegment StartX=33.9 StartY=-36.15 StartZ=0 EndX=-33.9 EndY=-36.15 EndZ=0
    g3: LineSegment StartX=-33.9 StartY=-36.15 StartZ=0 EndX=-33.9 EndY=34.7 EndZ=0
  constraints (8):
    c: Coincident(g0,g1)
    c: Coincident(g1,g2)
    c: Coincident(g2,g3)
    c: Coincident(g3,g0)
    c: Coincident(g0,g-3)
    c: Coincident(g1,g-4)
    c: Coincident(g0,g-4)
    c: Coincident(g2,g-3)
FEATURE [PartDesign::Pad] Pad004
  Direction = (0,0,1)
  Length = 1.2
  Length2 = 10
  Profile = -> Sketch012
  ReferenceAxis = -> Sketch012 [N_Axis]
  Suppressed = false
  Type = 0
  expr: Length = <<Spreadsheet>>.WallThickness
FEATURE [Sketcher::SketchObject] Sketch013
  ArcFitTolerance = 0
  AttachmentSupport = -> [XY_Plane002]
  ExternalGeometry = -> [Binder]
  FullyConstrained = true
  MakeInternals = false
  MapMode = 5
  expr: .AttachmentOffset.Base.z = 0
  expr: Constraints[8] = <<Spreadsheet>>.WallThickness
  sketch-geometry (9):
    g0: LineSegment StartX=-33.9 StartY=-36.15 StartZ=0 EndX=-35.1 EndY=-36.15 EndZ=0
    g1: LineSegment StartX=-35.1 StartY=-36.15 StartZ=0 EndX=-35.1 EndY=35.9 EndZ=0
    g2: LineSegment StartX=-35.1 StartY=35.9 StartZ=0 EndX=35.1 EndY=35.9 EndZ=0
    g3: LineSegment StartX=35.1 StartY=35.9 StartZ=0 EndX=35.1 EndY=-36.15 EndZ=0
    g4: LineSegment StartX=33.9 StartY=-36.15 StartZ=0 EndX=33.9 EndY=34.7 EndZ=0
    g5: LineSegment StartX=33.9 StartY=34.7 StartZ=0 EndX=-33.9 EndY=34.7 EndZ=0
    g6: LineSegment StartX=-33.9 StartY=34.7 StartZ=0 EndX=-33.9 EndY=-36.15 EndZ=0
    g7: LineSegment [constr] StartX=-33.9 StartY=34.7 StartZ=0 EndX=-33.9 EndY=35.9 EndZ=0
    g8: LineSegment StartX=33.9 StartY=-36.15 StartZ=0 EndX=35.1 EndY=-36.15 EndZ=0
  constraints (23):
    c: Horizontal(g0)
    c: Coincident(g0,g1)
    c: Vertical(g1)
    c: Coincident(g1,g2)
    c: Horizontal(g2)
    c: Coincident(g2,g3)
    c: Vertical(g3)
    c: Coincident(g6,g0)
    c: DistanceX(g0,g0) = 1.2
    c: PointOnObject(g7,g2)
    c: Coincident(g8,g4)
    c: Coincident(g8,g3)
    c: Horizontal(g8)
    c: Equal(g0,g7)
    c: Equal(g7,g8)
    c: Coincident(g0,g-3)
    c: Coincident(g4,g-4)
    c: Vertical(g7)
    c: Coincident(g6,g-3)
    c: Coincident(g4,g-4)
    c: Coincident(g5,g4)
    c: Coincident(g5,g6)
    c: Coincident(g7,g5)
FEATURE [PartDesign::Pad] Pad005
  BaseFeature = -> Pad004
  Direction = (0,0,1)
  Length = 18.8
  Length2 = 10
  Profile = -> Sketch013
  ReferenceAxis = -> Sketch013 [N_Axis]
  Refine = true
  Suppressed = false
  Type = 0
  expr: Length = <<Spreadsheet>>.SDOffset + <<Spreadsheet>>.SDHeight + 1 mm + <<Spreadsheet>>.WallThickness
FEATURE [Sketcher::SketchObject] Sketch014
  ArcFitTolerance = 0
  AttachmentOffset = pos=(0,0,35.75) rot=(0,0,1;0rad)
  AttachmentSupport = -> [XZ_Plane002]
  ExternalGeometry = -> [Binder001]
  FullyConstrained = true
  MakeInternals = false
  MapMode = 5
  Placement = pos=(0,-35.75,7.9e-15) rot=(1,0,0;1.5708rad)
  expr: .AttachmentOffset.Base.z = Sketch.Constraints.BaseLength / 2 + <<Spreadsheet>>.WallThickness
  sketch-geometry (6):
    g0: LineSegment StartX=33.9 StartY=17.7586 StartZ=0 EndX=31.9414 EndY=15.8 EndZ=0
    g1: LineSegment StartX=31.9414 StartY=15.8 StartZ=0 EndX=33.9 EndY=13.8414 EndZ=0
    g2: LineSegment StartX=33.9 StartY=13.8414 StartZ=0 EndX=33.9 EndY=17.7586 EndZ=0
    g3: LineSegment StartX=-33.9 StartY=13.8414 StartZ=0 EndX=-31.9414 EndY=15.8 EndZ=0
    g4: LineSegment StartX=-31.9414 StartY=15.8 StartZ=0 EndX=-33.9 EndY=17.7586 EndZ=0
    g5: LineSegment StartX=-33.9 StartY=17.7586 StartZ=0 EndX=-33.9 EndY=13.8414 EndZ=0
  constraints (12):
    c: Coincident(g-5,g0)
    c: Coincident(g0,g-6)
    c: Coincident(g0,g1)
    c: Coincident(g1,g-6)
    c: Coincident(g1,g2)
    c: Coincident(g2,g0)
    c: Coincident(g-4,g3)
    c: Coincident(g3,g-4)
    c: Coincident(g3,g4)
    c: Coincident(g4,g-3)
    c: Coincident(g4,g5)
    c: Coincident(g5,g3)
FEATURE [Sketcher::SketchObject] Sketch015
  ArcFitTolerance = 0
  AttachmentOffset = pos=(0,0,17.8) rot=(0,0,1;0rad)
  AttachmentSupport = -> [XY_Plane002]
  ExternalGeometry = -> [Binder]
  FullyConstrained = true
  MakeInternals = false
  MapMode = 5
  Placement = pos=(0,0,17.8) rot=(0,0,1;0rad)
  expr: .AttachmentOffset.Base.z = <<Spreadsheet>>.SDOffset + <<Spreadsheet>>.SDHeight + 1 mm + <<Spreadsheet>>.WallThickness - <<Spreadsheet>>.RidgeOffset
  sketch-geometry (4):
    g0: ArcOfCircle CenterX=31.8 CenterY=-32.55 CenterZ=0 NormalX=0 NormalY=0 NormalZ=1 AngleXU=0 Radius=1.7 StartAngle=4.71239 EndAngle=7.85398
    g1: LineSegment StartX=31.8 StartY=-30.85 StartZ=0 EndX=31.8 EndY=-34.25 EndZ=0
    g2: ArcOfCircle CenterX=-31.8 CenterY=-32.55 CenterZ=0 NormalX=0 NormalY=0 NormalZ=1 AngleXU=0 Radius=1.7 StartAngle=1.5708 EndAngle=4.71239
    g3: LineSegment StartX=-31.8 StartY=-30.85 StartZ=0 EndX=-31.8 EndY=-34.25 EndZ=0
  constraints (10):
    c: Coincident(g0,g-4)
    c: Coincident(g0,g-4)
    c: Equal(g0,g-4)
    c: Coincident(g1,g0)
    c: Coincident(g1,g0)
    c: Coincident(g2,g-3)
    c: Coincident(g2,g-3)
    c: Equal(g2,g-3)
    c: Coincident(g3,g2)
    c: Coincident(g3,g2)
FEATURE [Sketcher::SketchObject] Sketch016  label="MSH4B_SDRidges"
  ArcFitTolerance = 0
  AttachmentSupport = -> [XZ_Plane]
  ExternalGeometry = -> [Sketch001]
  FullyConstrained = true
  MakeInternals = false
  MapMode = 5
  Placement = pos=(0,0,0) rot=(1,0,0;1.5708rad)
  sketch-geometry (13):
    g0: ArcOfCircle CenterX=-24 CenterY=19.2131 CenterZ=0 NormalX=0 NormalY=0 NormalZ=1 AngleXU=0 Radius=9 StartAngle=4.14985 EndAngle=5.27493
    g1: LineSegment StartX=-28.8 StartY=11.6 StartZ=0 EndX=-19.2 EndY=11.6 EndZ=0
    g2: ArcOfCircle CenterX=24 CenterY=19.2131 CenterZ=0 NormalX=0 NormalY=0 NormalZ=1 AngleXU=0 Radius=9 StartAngle=4.14985 EndAngle=5.27493
    g3: ArcOfCircle CenterX=-8 CenterY=19.2131 CenterZ=0 NormalX=0 NormalY=0 NormalZ=1 AngleXU=0 Radius=9 StartAngle=4.14985 EndAngle=5.27493
    g4: ArcOfCircle CenterX=8 CenterY=19.2131 CenterZ=0 NormalX=0 NormalY=0 NormalZ=1 AngleXU=0 Radius=9 StartAngle=4.14985 EndAngle=5.27493
    g5: LineSegment StartX=-12.8 StartY=11.6 StartZ=0 EndX=-3.2 EndY=11.6 EndZ=0
    g6: LineSegment StartX=3.2 StartY=11.6 StartZ=0 EndX=12.8 EndY=11.6 EndZ=0
    g7: LineSegment StartX=19.2 StartY=11.6 StartZ=0 EndX=28.8 EndY=11.6 EndZ=0
    g8: LineSegment [constr] StartX=-24 StartY=19.2131 StartZ=0 EndX=-24 EndY=10.2131 EndZ=0
    g9: LineSegment [constr] StartX=-8 StartY=19.2131 StartZ=0 EndX=-8 EndY=10.2131 EndZ=0
    g10: LineSegment [constr] StartX=8 StartY=19.2131 StartZ=0 EndX=8 EndY=10.2131 EndZ=0
    g11: LineSegment [constr] StartX=24 StartY=19.2131 StartZ=0 EndX=24 EndY=10.2131 EndZ=0
    g12: LineSegment [constr] StartX=-24 StartY=19.2131 StartZ=0 EndX=24 EndY=19.2131 EndZ=0
  constraints (38):
    c: PointOnObject(g0,g-3)
    c: PointOnObject(g0,g-3)
    c: DistanceX(g-3,g0) = 1
    c: Coincident(g1,g0)
    c: Coincident(g1,g0)
    c: PointOnObject(g2,g-3)
    c: PointOnObject(g2,g-3)
    c: PointOnObject(g3,g-3)
    c: PointOnObject(g3,g-3)
    c: PointOnObject(g4,g-3)
    c: PointOnObject(g4,g-3)
    c: Equal(g0,g3)
    c: Equal(g3,g4)
    c: Equal(g4,g2)
    c: Coincident(g5,g3)
    c: Coincident(g5,g3)
    c: Coincident(g6,g4)
    c: Coincident(g6,g4)
    c: Coincident(g7,g2)
    c: Coincident(g7,g2)
    c: Radius(g0) = 9
    c: Coincident(g8,g0)
    c: PointOnObject(g8,g0)
    c: Symmetric(g-4,g-5,g8)
    c: Coincident(g9,g3)
    c: PointOnObject(g9,g3)
    c: Coincident(g10,g4)
    c: PointOnObject(g10,g4)
    c: Coincident(g11,g2)
    c: PointOnObject(g11,g2)
    c: Symmetric(g-6,g-7,g9)
    c: Coincident(g12,g0)
    c: Coincident(g12,g2)
    c: Horizontal(g12)
    c: PointOnObject(g3,g12)
    c: PointOnObject(g4,g12)
    c: Symmetric(g-8,g-9,g10)
    c: Symmetric(g-10,g-11,g11)
FEATURE [Sketcher::SketchObject] Sketch017
  ArcFitTolerance = 0
  AttachmentSupport = -> [XZ_Plane002]
  ExternalGeometry = -> [Binder001]
  FullyConstrained = true
  MakeInternals = false
  MapMode = 5
  Placement = pos=(0,0,0) rot=(1,0,0;1.5708rad)
  expr: Constraints[6] = <<Spreadsheet>>.Tolerance
  sketch-geometry (4):
    g0: LineSegment StartX=-10 StartY=18.8 StartZ=0 EndX=10 EndY=18.8 EndZ=0
    g1: LineSegment StartX=-10 StartY=18.8 StartZ=0 EndX=-10.1 EndY=18.8 EndZ=0
    g2: LineSegment StartX=10 StartY=18.8 StartZ=0 EndX=10.1 EndY=18.8 EndZ=0
    g3: ArcOfCircle CenterX=-1.08156e-11 CenterY=18.8 CenterZ=0 NormalX=0 NormalY=0 NormalZ=1 AngleXU=0 Radius=10.1 StartAngle=3.14159 EndAngle=6.28319
  constraints (11):
    c: Coincident(g0,g-3)
    c: Coincident(g0,g-3)
    c: Coincident(g1,g0)
    c: Coincident(g2,g0)
    c: Horizontal(g2)
    c: Horizontal(g1)
    c: DistanceX(g1,g1) = 0.1
    c: Equal(g1,g2)
    c: PointOnObject(g3,g0)
    c: Coincident(g3,g2)
    c: Coincident(g3,g1)
FEATURE [Sketcher::SketchObject] Sketch018  label="MSH2B_Template_XY"
  ArcFitTolerance = 0
  AttachmentSupport = -> [XY_Plane003]
  FullyConstrained = true
  MakeInternals = false
  MapMode = 5
  expr: .Constraints.BaseLength = <<Spreadsheet>>.SpacingY * (<<Spreadsheet>>.Rows - 1) + <<Spreadsheet>>.SDHoleThickness + 2 * <<Spreadsheet>>.Margin
  expr: .Constraints.Width = <<Spreadsheet>>.SpacingX * (<<Spreadsheet>>.Columns_2 - 1) + <<Spreadsheet>>.SDHoleWidth + 2 * <<Spreadsheet>>.Margin
  expr: Constraints[42] = <<Spreadsheet>>.LockRadius
  expr: Constraints[43] = <<Spreadsheet>>.LockRadius + <<Spreadsheet>>.Tolerance
  expr: Constraints[54] = <<Spreadsheet>>.Tolerance * 1.5
  expr: Constraints[58] = <<Spreadsheet>>.BackWallThickness
  expr: Constraints[63] = <<Spreadsheet>>.RidgeDepth
  expr: Constraints[66] = <<Spreadsheet>>.Tolerance
  sketch-geometry (22):
    g0: LineSegment StartX=17.8 StartY=34.55 StartZ=0 EndX=17.8 EndY=-36.15 EndZ=0
    g1: LineSegment StartX=17.8 StartY=-36.15 StartZ=0 EndX=-17.8 EndY=-36.15 EndZ=0
    g2: LineSegment StartX=-17.8 StartY=-36.15 StartZ=0 EndX=-17.8 EndY=34.55 EndZ=0
    g3: LineSegment StartX=-17.8 StartY=-4e-15 StartZ=0 EndX=17.8 EndY=-4e-15 EndZ=0
    g4: LineSegment StartX=-2e-16 StartY=34.55 StartZ=0 EndX=-2e-16 EndY=-36.15 EndZ=0
    g5: LineSegment StartX=-17.8 StartY=34.55 StartZ=0 EndX=-15.8 EndY=34.55 EndZ=0
    g6: LineSegment StartX=-15.8 StartY=34.55 StartZ=0 EndX=15.8 EndY=34.55 EndZ=0
    g7: ArcOfCircle CenterX=-15.8 CenterY=-32.55 CenterZ=0 NormalX=0 NormalY=0 NormalZ=1 AngleXU=0 Radius=1.6 StartAngle=1.5708 EndAngle=4.71239
    g8: LineSegment StartX=-15.8 StartY=-36.15 StartZ=0 EndX=-15.8 EndY=34.55 EndZ=0
    g9: ArcOfCircle CenterX=-15.8 CenterY=-32.55 CenterZ=0 NormalX=0 NormalY=0 NormalZ=1 AngleXU=0 Radius=1.7 StartAngle=1.5708 EndAngle=4.71239
    g10: LineSegment StartX=15.8 StartY=34.55 StartZ=0 EndX=15.8 EndY=-36.15 EndZ=0
    g11: ArcOfCircle CenterX=15.8 CenterY=-32.55 CenterZ=0 NormalX=0 NormalY=0 NormalZ=1 AngleXU=0 Radius=1.6 StartAngle=4.71239 EndAngle=7.85398
    g12: ArcOfCircle CenterX=15.8 CenterY=-32.55 CenterZ=0 NormalX=0 NormalY=0 NormalZ=1 AngleXU=0 Radius=1.7 StartAngle=4.71239 EndAngle=7.85398
    g13: LineSegment [constr] StartX=-15.8 StartY=-32.55 StartZ=0 EndX=15.8 EndY=-32.55 EndZ=0
    g14: LineSegment StartX=15.8 StartY=34.55 StartZ=0 EndX=17.8 EndY=34.55 EndZ=0
    g15: LineSegment StartX=-17.9 StartY=-36.15 StartZ=0 EndX=-17.9 EndY=34.7 EndZ=0
    g16: LineSegment StartX=-17.9 StartY=34.7 StartZ=0 EndX=17.9 EndY=34.7 EndZ=0
    g17: LineSegment StartX=17.9 StartY=34.7 StartZ=0 EndX=17.9 EndY=-36.15 EndZ=0
    g18: LineSegment [constr] StartX=17.8 StartY=34.55 StartZ=0 EndX=17.8 EndY=34.7 EndZ=0
    g19: LineSegment StartX=-17.8 StartY=-34.55 StartZ=0 EndX=17.8 EndY=-34.55 EndZ=0
    g20: LineSegment [constr] StartX=-17.9 StartY=-36.15 StartZ=0 EndX=-17.8 EndY=-36.15 EndZ=0
    g21: LineSegment [constr] StartX=17.8 StartY=-36.15 StartZ=0 EndX=17.9 EndY=-36.15 EndZ=0
  constraints (70):
    c: Coincident(g0,g1)
    c: Coincident(g1,g2)
    c: Coincident(g2,g5)
    c: Horizontal(g1)
    c: Vertical(g0)
    c: Vertical(g2)
    c: DistanceX(g5,g0) = 35.6  'Width'
    c: PointOnObject(g3,g2)
    c: PointOnObject(g3,g0)
    c: PointOnObject(g4,g1)
    c: Symmetric(g1,g0,g4)
    c: Coincident(g5,g6)
    c: Horizontal(g5)
    c: PointOnObject(g4,g6)
    c: Coincident(g8,g5)
    c: Vertical(g8)
    c: PointOnObject(g7,g8)
    c: PointOnObject(g7,g8)
    c: Coincident(g9,g7)
    c: PointOnObject(g9,g8)
    c: Vertical(g10)
    c: PointOnObject(g11,g10)
    c: PointOnObject(g11,g10)
    c: Coincident(g12,g11)
    c: PointOnObject(g12,g10)
    c: Equal(g7,g11)
    c: Equal(g12,g9)
    c: PointOnObject(g8,g1)
    c: PointOnObject(g9,g8)
    c: PointOnObject(g7,g8)
    c: DistanceY(g8,g7) = 2
    c: PointOnObject(g10,g1)
    c: PointOnObject(g12,g10)
    c: PointOnObject(g11,g10)
    c: Coincident(g13,g7)
    c: Coincident(g13,g11)
    c: Horizontal(g13)
    c: Coincident(g6,g10)
    c: Coincident(g14,g6)
    c: Coincident(g14,g0)
    c: Horizontal(g14)
    c: Symmetric(g5,g6,g4)
    c: Radius(g7) = 1.6
    c: Radius(g9) = 1.7
    c: Vertical(g15)
    c: Coincident(g15,g16)
    c: Horizontal(g16)
    c: Coincident(g16,g17)
    c: Vertical(g17)
    c: PointOnObject(g17,g1)
    c: PointOnObject(g15,g1)
    c: Coincident(g18,g0)
    c: PointOnObject(g18,g16)
    c: Vertical(g18)
    c: DistanceY(g18,g18) = 0.15
    c: DistanceY(g15,g15) = 70.85  'CoverLength'
    c: PointOnObject(g19,g2)
    c: Horizontal(g19)
    c: DistanceY(g1,g19) = 1.6
    c: Symmetric(g19,g0,g-1)  '__ANCHOR__'
    c: DistanceY(g19,g2) = 69.1  'BaseLength'
    c: Symmetric(g19,g0,g3)
    c: Horizontal(g3)
    c: DistanceX(g1,g8) = 2
    c: Coincident(g20,g15)
    c: Coincident(g1,g20)
    c: DistanceX(g20,g20) = 0.1
    c: Coincident(g21,g0)
    c: Coincident(g21,g17)
    c: Equal(g21,g20)
FEATURE [Sketcher::SketchObject] Sketch019  label="MSH2B_Template_SD"
  ArcFitTolerance = 0
  AttachmentSupport = -> [XZ_Plane003]
  ExternalGeometry = -> [Sketch018]
  FullyConstrained = true
  MakeInternals = false
  MapMode = 5
  Placement = pos=(0,0,0) rot=(1,0,0;1.5708rad)
  expr: Constraints[30] = <<Spreadsheet>>.SDHeight
  expr: Constraints[31] = <<Spreadsheet>>.SDHoleWidth
  expr: Constraints[38] = <<Spreadsheet>>.SDFree
  expr: Constraints[39] = <<Spreadsheet>>.SpacingX
  expr: Constraints[43] = <<Spreadsheet>>.SDOffset
  sketch-geometry (16):
    g0: LineSegment StartX=2.2 StartY=1.6 StartZ=0 EndX=2.2 EndY=16.6 EndZ=0
    g1: LineSegment StartX=2.2 StartY=16.6 StartZ=0 EndX=13.8 EndY=16.6 EndZ=0
    g2: LineSegment StartX=13.8 StartY=16.6 StartZ=0 EndX=13.8 EndY=6.4 EndZ=0
    g3: LineSegment StartX=12.7 StartY=1.6 StartZ=0 EndX=2.2 EndY=1.6 EndZ=0
    g4: LineSegment StartX=12.7 StartY=1.6 StartZ=0 EndX=12.7 EndY=5.3 EndZ=0
    g5: LineSegment StartX=12.7 StartY=5.3 StartZ=0 EndX=13.8 EndY=6.4 EndZ=0
    g6: GeomPoint [constr] X=-1.105e-13 Y=0 Z=0
    g7: LineSegment [constr] StartX=2.2 StartY=16.6 StartZ=0 EndX=-2.2 EndY=16.6 EndZ=0
    g8: LineSegment StartX=-2.2 StartY=16.6 StartZ=0 EndX=-2.2 EndY=6.4 EndZ=0
    g9: LineSegment StartX=-2.2 StartY=6.4 StartZ=0 EndX=-3.3 EndY=5.3 EndZ=0
    g10: LineSegment StartX=-3.3 StartY=5.3 StartZ=0 EndX=-3.3 EndY=1.6 EndZ=0
    g11: LineSegment StartX=-3.3 StartY=1.6 StartZ=0 EndX=-13.8 EndY=1.6 EndZ=0
    g12: LineSegment StartX=-13.8 StartY=1.6 StartZ=0 EndX=-13.8 EndY=16.6 EndZ=0
    g13: LineSegment StartX=-13.8 StartY=16.6 StartZ=0 EndX=-2.2 EndY=16.6 EndZ=0
    g14: LineSegment StartX=-13.8 StartY=11.6 StartZ=0 EndX=13.8 EndY=11.6 EndZ=0
    g15: LineSegment [constr] StartX=-2e-16 StartY=16.6 StartZ=0 EndX=-2e-16 EndY=0 EndZ=0
  constraints (45):
    c: Coincident(g3,g0)
    c: Coincident(g0,g1)
    c: Coincident(g1,g2)
    c: Horizontal(g1)
    c: Vertical(g0)
    c: Vertical(g2)
    c: Horizontal(g3)
    c: Vertical(g4)
    c: Coincident(g5,g4)
    c: Coincident(g2,g5)
    c: Horizontal(g7)
    c: Coincident(g7,g0)
    c: Coincident(g7,g8)
    c: Vertical(g8)
    c: Coincident(g8,g9)
    c: Coincident(g9,g10)
    c: Vertical(g10)
    c: Coincident(g10,g11)
    c: Horizontal(g11)
    c: Coincident(g11,g12)
    c: Vertical(g12)
    c: Coincident(g12,g13)
    c: Coincident(g13,g8)
    c: Horizontal(g13)
    c: Equal(g13,g1)
    c: Equal(g12,g0)
    c: Equal(g8,g2)
    c: Equal(g11,g3)
    c: Equal(g10,g4)
    c: Coincident(g6,g-1)  '__ANCHOR__'
    c: DistanceY(g12,g12) = 15
    c: DistanceX(g13,g13) = 11.6
    c: Angle(g8,g9) = 2.35619
    c: DistanceY(g10,g8) = 4.8
    c: DistanceX(g10,g8) = 1.1
    c: Coincident(g3,g4)
    c: PointOnObject(g14,g12)
    c: Horizontal(g14)
    c: DistanceY(g14,g12) = 5
    c: DistanceX(g12,g0) = 16
    c: Coincident(g-3,g15)
    c: Symmetric(g8,g0,g15)
    c: Vertical(g15)
    c: DistanceY(g6,g0) = 1.6
    c: PointOnObject(g14,g2)
FEATURE [Sketcher::SketchObject] Sketch020  label="MSH2B_Foundation001"
  ArcFitTolerance = 0
  AttachmentSupport = -> [XY_Plane003]
  ExternalGeometry = -> [Sketch018]
  FullyConstrained = true
  MakeInternals = false
  MapMode = 5
  sketch-geometry (4):
    g0: LineSegment StartX=17.8 StartY=34.55 StartZ=0 EndX=17.8 EndY=-36.15 EndZ=0
    g1: LineSegment StartX=17.8 StartY=-36.15 StartZ=0 EndX=-17.8 EndY=-36.15 EndZ=0
    g2: LineSegment StartX=-17.8 StartY=-36.15 StartZ=0 EndX=-17.8 EndY=34.55 EndZ=0
    g3: LineSegment StartX=-17.8 StartY=34.55 StartZ=0 EndX=17.8 EndY=34.55 EndZ=0
  constraints (8):
    c: Coincident(g0,g1)
    c: Coincident(g1,g2)
    c: Coincident(g2,g3)
    c: Coincident(g3,g0)
    c: Coincident(g0,g-4)
    c: Coincident(g0,g-4)
    c: Coincident(g2,g-3)
    c: Coincident(g1,g-3)
FEATURE [PartDesign::Pad] Pad007  label="MSH2B_Foundation"
  Direction = (0,0,1)
  Length = 11.6
  Length2 = 10
  Profile = -> Sketch020
  ReferenceAxis = -> Sketch020 [N_Axis]
  Suppressed = false
  Type = 0
  expr: Length = <<Spreadsheet>>.BaseHeight
FEATURE [Sketcher::SketchObject] Sketch021  label="MSH2B_SDHoles"
  ArcFitTolerance = 0
  AttachmentOffset = pos=(0,0,30.55) rot=(0,0,1;0rad)
  AttachmentSupport = -> [XZ_Plane003]
  ExternalGeometry = -> [Sketch019]
  FullyConstrained = true
  MakeInternals = false
  MapMode = 5
  Placement = pos=(0,-30.55,6.8e-15) rot=(1,0,0;1.5708rad)
  expr: .AttachmentOffset.Base.z = Sketch018.Constraints.BaseLength / 2 - <<Spreadsheet>>.Margin
  sketch-geometry (12):
    g0: LineSegment StartX=-2.2 StartY=6.4 StartZ=0 EndX=-2.2 EndY=16.6 EndZ=0
    g1: LineSegment StartX=-2.2 StartY=16.6 StartZ=0 EndX=-13.8 EndY=16.6 EndZ=0
    g2: LineSegment StartX=-13.8 StartY=16.6 StartZ=0 EndX=-13.8 EndY=1.6 EndZ=0
    g3: LineSegment StartX=-13.8 StartY=1.6 StartZ=0 EndX=-3.3 EndY=1.6 EndZ=0
    g4: LineSegment StartX=-3.3 StartY=1.6 StartZ=0 EndX=-3.3 EndY=5.3 EndZ=0
    g5: LineSegment StartX=-3.3 StartY=5.3 StartZ=0 EndX=-2.2 EndY=6.4 EndZ=0
    g6: LineSegment StartX=2.2 StartY=16.6 StartZ=0 EndX=2.2 EndY=1.6 EndZ=0
    g7: LineSegment StartX=2.2 StartY=1.6 StartZ=0 EndX=12.7 EndY=1.6 EndZ=0
    g8: LineSegment StartX=12.7 StartY=1.6 StartZ=0 EndX=12.7 EndY=5.3 EndZ=0
    g9: LineSegment StartX=12.7 StartY=5.3 StartZ=0 EndX=13.8 EndY=6.4 EndZ=0
    g10: LineSegment StartX=13.8 StartY=6.4 StartZ=0 EndX=13.8 EndY=16.6 EndZ=0
    g11: LineSegment StartX=13.8 StartY=16.6 StartZ=0 EndX=2.2 EndY=16.6 EndZ=0
  constraints (24):
    c: Coincident(g-4,g0)
    c: Coincident(g0,g-4)
    c: Coincident(g0,g1)
    c: Coincident(g1,g-3)
    c: Coincident(g1,g2)
    c: Coincident(g2,g-3)
    c: Coincident(g2,g3)
    c: Coincident(g3,g-5)
    c: Coincident(g3,g4)
    c: Coincident(g4,g-5)
    c: Coincident(g4,g5)
    c: Coincident(g5,g0)
    c: Coincident(g-6,g6)
    c: Coincident(g6,g-6)
    c: Coincident(g6,g7)
    c: Coincident(g7,g-8)
    c: Coincident(g7,g8)
    c: Coincident(g8,g-8)
    c: Coincident(g8,g9)
    c: Coincident(g9,g-7)
    c: Coincident(g9,g10)
    c: Coincident(g10,g-7)
    c: Coincident(g10,g11)
    c: Coincident(g11,g6)
FEATURE [Sketcher::SketchObject] Sketch024  label="MSH2B_Lock"
  ArcFitTolerance = 0
  AttachmentOffset = pos=(0,0,1) rot=(0,0,1;0rad)
  AttachmentSupport = -> [XY_Plane003]
  ExternalGeometry = -> [Sketch018]
  FullyConstrained = true
  MakeInternals = false
  MapMode = 5
  Placement = pos=(0,0,1) rot=(0,0,1;0rad)
  expr: .AttachmentOffset.Base.z = <<Spreadsheet>>.RidgeOffset
  sketch-geometry (4):
    g0: ArcOfCircle CenterX=-15.8 CenterY=-32.55 CenterZ=0 NormalX=0 NormalY=0 NormalZ=1 AngleXU=0 Radius=1.6 StartAngle=1.5708 EndAngle=4.71239
    g1: ArcOfCircle CenterX=15.8 CenterY=-32.55 CenterZ=0 NormalX=0 NormalY=0 NormalZ=1 AngleXU=0 Radius=1.6 StartAngle=4.71239 EndAngle=7.85398
    g2: LineSegment StartX=15.8 StartY=-30.95 StartZ=0 EndX=15.8 EndY=-34.15 EndZ=0
    g3: LineSegment StartX=-15.8 StartY=-30.95 StartZ=0 EndX=-15.8 EndY=-34.15 EndZ=0
  constraints (10):
    c: Coincident(g2,g1)
    c: Coincident(g2,g1)
    c: Coincident(g3,g0)
    c: Coincident(g3,g0)
    c: Coincident(g1,g-4)
    c: Coincident(g1,g-4)
    c: Equal(g1,g-4)
    c: Coincident(g0,g-3)
    c: Coincident(g0,g-3)
    c: Equal(g0,g-3)
FEATURE [Sketcher::SketchObject] Sketch025  label="MSH2B_Template_XZ"
  ArcFitTolerance = 0
  AttachmentSupport = -> [XZ_Plane003]
  FullyConstrained = true
  MakeInternals = false
  MapMode = 5
  Placement = pos=(0,0,0) rot=(1,0,0;1.5708rad)
  expr: Constraints[13] = <<Spreadsheet>>.Tolerance
  expr: Constraints[29] = <<Spreadsheet>>.SDOffset + <<Spreadsheet>>.SDHeight + 1 mm
  expr: Constraints[41] = <<Spreadsheet>>.SDFree + 1 mm
  expr: Constraints[67] = <<Spreadsheet>>.RidgeDepth
  expr: Constraints[68] = <<Spreadsheet>>.RidgeOffset
  expr: Constraints[6] = <<MSH2B_Template_XY>>.Constraints.Width
  sketch-geometry (31):
    g0: LineSegment StartX=-17.8 StartY=0 StartZ=0 EndX=17.8 EndY=0 EndZ=0
    g1: LineSegment StartX=17.8 StartY=11.6 StartZ=0 EndX=-17.8 EndY=11.6 EndZ=0
    g2: LineSegment [constr] StartX=-17.8 StartY=0 StartZ=0 EndX=-17.9 EndY=0 EndZ=0
    g3: LineSegment [constr] StartX=17.8 StartY=0 StartZ=0 EndX=17.9 EndY=0 EndZ=0
    g4: LineSegment StartX=-17.8 StartY=1 StartZ=0 EndX=-17.8 EndY=0 EndZ=0
    g5: LineSegment StartX=-17.8 StartY=3.70711 StartZ=0 EndX=-17.8 EndY=1 EndZ=0
    g6: LineSegment StartX=-17.8 StartY=11.6 StartZ=0 EndX=-17.8 EndY=3.70711 EndZ=0
    g7: LineSegment StartX=-17.8 StartY=1 StartZ=0 EndX=-16.3 EndY=1 EndZ=0
    g8: LineSegment StartX=17.8 StartY=0 StartZ=0 EndX=17.8 EndY=1 EndZ=0
    g9: LineSegment StartX=17.8 StartY=1 StartZ=0 EndX=16.3 EndY=1 EndZ=0
    g10: LineSegment StartX=16.0172 StartY=1.78284 StartZ=0 EndX=17.9 EndY=3.66569 EndZ=0
    g11: LineSegment StartX=-17.9 StartY=17.6 StartZ=0 EndX=17.9 EndY=17.6 EndZ=0
    g12: LineSegment StartX=-17.9 StartY=1.1 StartZ=0 EndX=-16.3 EndY=1.1 EndZ=0
    g13: LineSegment [constr] StartX=-16.3 StartY=1 StartZ=0 EndX=-16.3 EndY=1.1 EndZ=0
    g14: LineSegment StartX=17.8 StartY=3.70711 StartZ=0 EndX=15.9464 EndY=1.85355 EndZ=0
    g15: LineSegment StartX=16.3 StartY=1.1 StartZ=0 EndX=17.9 EndY=1.1 EndZ=0
    g16: LineSegment StartX=-17.9 StartY=0 StartZ=0 EndX=-17.9 EndY=1.1 EndZ=0
    g17: LineSegment StartX=-17.9 StartY=1.1 StartZ=0 EndX=-17.9 EndY=17.6 EndZ=0
    g18: LineSegment StartX=17.9 StartY=17.6 StartZ=0 EndX=17.9 EndY=1.1 EndZ=0
    g19: LineSegment StartX=17.9 StartY=1.1 StartZ=0 EndX=17.9 EndY=0 EndZ=0
    g20: ArcOfCircle CenterX=-6e-16 CenterY=0 CenterZ=0 NormalX=0 NormalY=0 NormalZ=1 AngleXU=0 Radius=10 StartAngle=0 EndAngle=3.14159
    g21: ArcOfCircle CenterX=-16.3 CenterY=1.5 CenterZ=0 NormalX=0 NormalY=0 NormalZ=1 AngleXU=0 Radius=0.4 StartAngle=4.71239 EndAngle=7.06858
    g22: LineSegment StartX=-16.0172 StartY=1.78284 StartZ=0 EndX=-17.9 EndY=3.66569 EndZ=0
    g23: LineSegment [constr] StartX=-16.3 StartY=1.5 StartZ=0 EndX=-15.8 EndY=1.5 EndZ=0
    g24: ArcOfCircle CenterX=-16.3 CenterY=1.5 CenterZ=0 NormalX=0 NormalY=0 NormalZ=1 AngleXU=0 Radius=0.5 StartAngle=4.71239 EndAngle=7.06858
    g25: LineSegment [constr] StartX=-16.0172 StartY=1.78284 StartZ=0 EndX=-15.9464 EndY=1.85355 EndZ=0
    g26: LineSegment StartX=-15.9464 StartY=1.85355 StartZ=0 EndX=-17.8 EndY=3.70711 EndZ=0
    g27: LineSegment StartX=17.8 StartY=1 StartZ=0 EndX=17.8 EndY=3.70711 EndZ=0
    g28: LineSegment StartX=17.8 StartY=3.70711 StartZ=0 EndX=17.8 EndY=11.6 EndZ=0
    g29: ArcOfCircle CenterX=16.3 CenterY=1.5 CenterZ=0 NormalX=0 NormalY=0 NormalZ=1 AngleXU=0 Radius=0.4 StartAngle=2.35619 EndAngle=4.71239
    g30: ArcOfCircle CenterX=16.3 CenterY=1.5 CenterZ=0 NormalX=0 NormalY=0 NormalZ=1 AngleXU=0 Radius=0.5 StartAngle=2.35619 EndAngle=4.71239
  constraints (83):
    c: Coincident(g0,g8)
    c: Coincident(g28,g1)
    c: Coincident(g1,g6)
    c: Coincident(g4,g0)
    c: Horizontal(g0)
    c: Horizontal(g1)
    c: DistanceX(g1,g1) = 35.6
    c: Symmetric(g0,g0,g-1)  '__ANCHOR__'
    c: Coincident(g2,g0)
    c: Horizontal(g2)
    c: Coincident(g3,g0)
    c: Horizontal(g3)
    c: Equal(g3,g2)
    c: DistanceX(g2,g2) = 0.1
    c: Coincident(g5,g4)
    c: Vertical(g4)
    c: Vertical(g5)
    c: Vertical(g6)
    c: Coincident(g7,g4)
    c: Coincident(g8,g27)
    c: Vertical(g8)
    c: Equal(g4,g8)
    c: Coincident(g8,g9)
    c: Equal(g9,g7)
    c: Coincident(g2,g16)
    c: Coincident(g17,g11)
    c: Horizontal(g11)
    c: Coincident(g11,g18)
    c: Coincident(g19,g3)
    c: DistanceY(g16,g17) = 17.6
    c: Equal(g2,g13)
    c: Equal(g15,g12)
    c: Coincident(g16,g17)
    c: Vertical(g16)
    c: Vertical(g17)
    c: Coincident(g16,g12)
    c: Coincident(g18,g19)
    c: Vertical(g18)
    c: Vertical(g19)
    c: Coincident(g15,g18)
    c: Equal(g19,g16)
    c: DistanceY(g1,g11) = 6
    c: Parallel(g12,g7)
    c: PointOnObject(g20,g0)
    c: PointOnObject(g20,g0)
    c: Symmetric(g0,g0,g20)
    c: Radius(g20) = 10
    c: PointOnObject(g13,g7)
    c: Coincident(g13,g12)
    c: Horizontal(g7)
    c: Tangent(g12,g21) = -1.5708
    c: Radius(g21) = 0.4
    c: PointOnObject(g22,g17)
    c: Tangent(g21,g22) = -1.5708
    c: Vertical(g13)
    c: Coincident(g23,g21)
    c: Horizontal(g23)
    c: Coincident(g24,g21)
    c: Tangent(g7,g24) = -1.5708
    c: Coincident(g25,g21)
    c: Perpendicular(g22,g25)
    c: Coincident(g26,g5)
    c: Tangent(g26,g24) = -1.5708
    c: Coincident(g25,g24)
    c: Angle(g22,g12) = 0.785398
    c: PointOnObject(g23,g24)
    c: Coincident(g6,g5)
    c: DistanceX(g5,g23) = 2
    c: DistanceY(g2,g4) = 1
    c: Horizontal(g9)
    c: Coincident(g27,g28)
    c: Vertical(g27)
    c: Vertical(g28)
    c: Equal(g27,g5)
    c: Coincident(g30,g29)
    c: Tangent(g15,g29) = -1.5708
    c: Tangent(g9,g30) = 1.5708
    c: Tangent(g10,g29) = 1.5708
    c: Tangent(g14,g30) = -1.5708
    c: Parallel(g10,g14)
    c: Equal(g29,g21)
    c: Coincident(g14,g27)
    c: PointOnObject(g10,g18)
FEATURE [Sketcher::SketchObject] Sketch022  label="MSH2B_BackWall"
  ArcFitTolerance = 0
  AttachmentOffset = pos=(0,0,34.55) rot=(0,0,1;0rad)
  AttachmentSupport = -> [XZ_Plane003]
  ExternalGeometry = -> [Sketch025]
  FullyConstrained = true
  MakeInternals = false
  MapMode = 5
  Placement = pos=(0,-34.55,7.7e-15) rot=(1,0,0;1.5708rad)
  expr: .AttachmentOffset.Base.z = Sketch018.Constraints.BaseLength / 2
  expr: Constraints[9] = <<Spreadsheet>>.Tolerance
  sketch-geometry (4):
    g0: LineSegment StartX=-17.8 StartY=0 StartZ=0 EndX=17.8 EndY=0 EndZ=0
    g1: LineSegment StartX=17.8 StartY=0 StartZ=0 EndX=17.8 EndY=17.5 EndZ=0
    g2: LineSegment StartX=17.8 StartY=17.5 StartZ=0 EndX=-17.8 EndY=17.5 EndZ=0
    g3: LineSegment StartX=-17.8 StartY=17.5 StartZ=0 EndX=-17.8 EndY=0 EndZ=0
  constraints (10):
    c: Coincident(g0,g1)
    c: Coincident(g1,g2)
    c: Coincident(g2,g3)
    c: Coincident(g3,g0)
    c: Horizontal(g2)
    c: Vertical(g1)
    c: Vertical(g3)
    c: Coincident(g0,g-3)
    c: Coincident(g0,g-3)
    c: DistanceY(g1,g-4) = 0.1
FEATURE [Sketcher::SketchObject] Sketch023  label="MSH2B_Ridge"
  ArcFitTolerance = 0
  AttachmentSupport = -> [XZ_Plane003]
  ExternalGeometry = -> [Sketch025]
  FullyConstrained = true
  MakeInternals = false
  MapMode = 5
  Placement = pos=(0,0,0) rot=(1,0,0;1.5708rad)
  sketch-geometry (8):
    g0: LineSegment StartX=-16.3 StartY=1 StartZ=0 EndX=-17.8 EndY=1 EndZ=0
    g1: LineSegment StartX=-17.8 StartY=1 StartZ=0 EndX=-17.8 EndY=3.70711 EndZ=0
    g2: LineSegment StartX=-17.8 StartY=3.70711 StartZ=0 EndX=-15.9464 EndY=1.85355 EndZ=0
    g3: ArcOfCircle CenterX=-16.3 CenterY=1.5 CenterZ=0 NormalX=0 NormalY=0 NormalZ=1 AngleXU=0 Radius=0.5 StartAngle=4.71239 EndAngle=7.06858
    g4: LineSegment StartX=16.3 StartY=1 StartZ=0 EndX=17.8 EndY=1 EndZ=0
    g5: LineSegment StartX=17.8 StartY=1 StartZ=0 EndX=17.8 EndY=3.70711 EndZ=0
    g6: LineSegment StartX=17.8 StartY=3.70711 StartZ=0 EndX=15.9464 EndY=1.85355 EndZ=0
    g7: ArcOfCircle CenterX=16.3 CenterY=1.5 CenterZ=0 NormalX=0 NormalY=0 NormalZ=1 AngleXU=0 Radius=0.5 StartAngle=2.35619 EndAngle=4.71239
  constraints (18):
    c: Coincident(g0,g-4)
    c: Coincident(g0,g-4)
    c: Coincident(g1,g0)
    c: Coincident(g1,g-5)
    c: Coincident(g2,g1)
    c: Coincident(g2,g-5)
    c: Coincident(g3,g-5)
    c: Coincident(g3,g0)
    c: Equal(g3,g-3)
    c: Coincident(g-8,g4)
    c: Coincident(g4,g-8)
    c: Coincident(g4,g5)
    c: Coincident(g5,g-6)
    c: Coincident(g5,g6)
    c: Coincident(g6,g-7)
    c: Coincident(g7,g4)
    c: Coincident(g7,g-7)
    c: Equal(g7,g-7)
FEATURE [Sketcher::SketchObject] Sketch026  label="MSH2B_SDRidges"
  ArcFitTolerance = 0
  AttachmentSupport = -> [XZ_Plane003]
  ExternalGeometry = -> [Sketch019]
  FullyConstrained = true
  MakeInternals = false
  MapMode = 5
  Placement = pos=(0,0,0) rot=(1,0,0;1.5708rad)
  sketch-geometry (7):
    g0: ArcOfCircle CenterX=-8 CenterY=19.2131 CenterZ=0 NormalX=0 NormalY=0 NormalZ=1 AngleXU=0 Radius=9 StartAngle=4.14985 EndAngle=5.27493
    g1: ArcOfCircle CenterX=8 CenterY=19.2131 CenterZ=0 NormalX=0 NormalY=0 NormalZ=1 AngleXU=0 Radius=9 StartAngle=4.14985 EndAngle=5.27493
    g2: LineSegment StartX=-12.8 StartY=11.6 StartZ=0 EndX=-3.2 EndY=11.6 EndZ=0
    g3: LineSegment StartX=3.2 StartY=11.6 StartZ=0 EndX=12.8 EndY=11.6 EndZ=0
    g4: LineSegment [constr] StartX=-8 StartY=19.2131 StartZ=0 EndX=-8 EndY=10.2131 EndZ=0
    g5: LineSegment [constr] StartX=8 StartY=19.2131 StartZ=0 EndX=8 EndY=10.2131 EndZ=0
    g6: LineSegment [constr] StartX=-8 StartY=19.2131 StartZ=0 EndX=8 EndY=19.2131 EndZ=0
  constraints (20):
    c: Equal(g0,g1)
    c: Coincident(g2,g0)
    c: Coincident(g2,g0)
    c: Coincident(g3,g1)
    c: Coincident(g3,g1)
    c: Coincident(g4,g0)
    c: PointOnObject(g4,g0)
    c: Coincident(g5,g1)
    c: PointOnObject(g5,g1)
    c: Horizontal(g6)
    c: Radius(g0) = 9
    c: PointOnObject(g0,g-3)
    c: PointOnObject(g0,g-3)
    c: PointOnObject(g1,g-3)
    c: PointOnObject(g1,g-3)
    c: DistanceX(g-3,g0) = 1
    c: Coincident(g0,g6)
    c: Symmetric(g-5,g-4,g4)
    c: Symmetric(g-6,g-7,g5)
    c: Coincident(g6,g1)
FEATURE [PartDesign::SubShapeBinder] Binder004
  BindCopyOnChange = 0
  BindMode = 0
  ClaimChildren = false
  Context = -> Part001 [Body004.Binder004.]
  Fuse = false
  MakeFace = true
  OffsetFill = false
  OffsetIntersection = false
  OffsetJoinType = 0
  OffsetOpenResult = false
  PartialLoad = false
  Relative = true
  Support = -> [Body003[Sketch018.]]
  _Version = 2
FEATURE [Sketcher::SketchObject] Sketch032  label="MSH2C_Top"
  ArcFitTolerance = 0
  AttachmentSupport = -> [XY_Plane005]
  ExternalGeometry = -> [Binder004]
  FullyConstrained = true
  MakeInternals = false
  MapMode = 5
  sketch-geometry (4):
    g0: LineSegment StartX=-17.9 StartY=34.7 StartZ=0 EndX=17.9 EndY=34.7 EndZ=0
    g1: LineSegment StartX=17.9 StartY=34.7 StartZ=0 EndX=17.9 EndY=-36.15 EndZ=0
    g2: LineSegment StartX=17.9 StartY=-36.15 StartZ=0 EndX=-17.9 EndY=-36.15 EndZ=0
    g3: LineSegment StartX=-17.9 StartY=-36.15 StartZ=0 EndX=-17.9 EndY=34.7 EndZ=0
  constraints (8):
    c: Coincident(g0,g1)
    c: Coincident(g1,g2)
    c: Coincident(g2,g3)
    c: Coincident(g3,g0)
    c: Coincident(g1,g-4)
    c: Coincident(g2,g-3)
    c: Coincident(g0,g-3)
    c: Coincident(g0,g-4)
FEATURE [PartDesign::Pad] Pad013  label="MSH2C_Top_"
  Direction = (0,0,1)
  Length = 1.2
  Length2 = 10
  Profile = -> Sketch032
  ReferenceAxis = -> Sketch032 [N_Axis]
  Suppressed = false
  Type = 0
  expr: Length = <<Spreadsheet>>.WallThickness
FEATURE [Sketcher::SketchObject] Sketch033  label="MSH2C_Walls"
  ArcFitTolerance = 0
  AttachmentSupport = -> [XY_Plane005]
  ExternalGeometry = -> [Binder004]
  FullyConstrained = true
  MakeInternals = false
  MapMode = 5
  expr: .AttachmentOffset.Base.z = 0
  expr: Constraints[10] = <<Spreadsheet>>.WallThickness
  sketch-geometry (9):
    g0: LineSegment StartX=-17.9 StartY=-36.15 StartZ=0 EndX=-19.1 EndY=-36.15 EndZ=0
    g1: LineSegment StartX=-19.1 StartY=-36.15 StartZ=0 EndX=-19.1 EndY=35.9 EndZ=0
    g2: LineSegment StartX=-19.1 StartY=35.9 StartZ=0 EndX=19.1 EndY=35.9 EndZ=0
    g3: LineSegment StartX=19.1 StartY=35.9 StartZ=0 EndX=19.1 EndY=-36.15 EndZ=0
    g4: LineSegment StartX=17.9 StartY=-36.15 StartZ=0 EndX=17.9 EndY=34.7 EndZ=0
    g5: LineSegment StartX=17.9 StartY=34.7 StartZ=0 EndX=-17.9 EndY=34.7 EndZ=0
    g6: LineSegment StartX=-17.9 StartY=34.7 StartZ=0 EndX=-17.9 EndY=-36.15 EndZ=0
    g7: LineSegment StartX=17.9 StartY=-36.15 StartZ=0 EndX=19.1 EndY=-36.15 EndZ=0
    g8: LineSegment [constr] StartX=-17.9 StartY=34.7 StartZ=0 EndX=-17.9 EndY=35.9 EndZ=0
  constraints (23):
    c: Horizontal(g0)
    c: Coincident(g0,g1)
    c: Vertical(g1)
    c: Coincident(g1,g2)
    c: Horizontal(g2)
    c: Coincident(g2,g3)
    c: Vertical(g3)
    c: Coincident(g4,g5)
    c: Coincident(g5,g6)
    c: Coincident(g6,g0)
    c: DistanceX(g0,g0) = 1.2
    c: Coincident(g7,g4)
    c: Coincident(g7,g3)
    c: Horizontal(g7)
    c: Coincident(g4,g-4)
    c: Coincident(g4,g-4)
    c: Coincident(g5,g-3)
    c: Coincident(g0,g-3)
    c: Coincident(g8,g5)
    c: PointOnObject(g8,g2)
    c: Vertical(g8)
    c: Equal(g0,g7)
    c: Equal(g7,g8)
FEATURE [PartDesign::Pad] Pad014  label="MSH2C_Walls_"
  BaseFeature = -> Pad013
  Direction = (0,0,1)
  Length = 18.8
  Length2 = 10
  Profile = -> Sketch033
  ReferenceAxis = -> Sketch033 [N_Axis]
  Refine = true
  Suppressed = false
  Type = 0
  expr: Length = <<Spreadsheet>>.SDOffset + <<Spreadsheet>>.SDHeight + 1 mm + <<Spreadsheet>>.WallThickness
FEATURE [Sketcher::SketchObject] Sketch035
  ArcFitTolerance = 0
  AttachmentOffset = pos=(0,0,17.8) rot=(0,0,1;0rad)
  AttachmentSupport = -> [XY_Plane005]
  ExternalGeometry = -> [Binder004]
  FullyConstrained = true
  MakeInternals = false
  MapMode = 5
  Placement = pos=(0,0,17.8) rot=(0,0,1;0rad)
  expr: .AttachmentOffset.Base.z = <<Spreadsheet>>.SDOffset + <<Spreadsheet>>.SDHeight + 1 mm + <<Spreadsheet>>.WallThickness - <<Spreadsheet>>.RidgeOffset
  sketch-geometry (4):
    g0: ArcOfCircle CenterX=15.8 CenterY=-32.55 CenterZ=0 NormalX=0 NormalY=0 NormalZ=1 AngleXU=0 Radius=1.7 StartAngle=4.71239 EndAngle=7.85398
    g1: LineSegment StartX=15.8 StartY=-30.85 StartZ=0 EndX=15.8 EndY=-34.25 EndZ=0
    g2: ArcOfCircle CenterX=-15.8 CenterY=-32.55 CenterZ=0 NormalX=0 NormalY=0 NormalZ=1 AngleXU=0 Radius=1.7 StartAngle=1.5708 EndAngle=4.71239
    g3: LineSegment StartX=-15.8 StartY=-30.85 StartZ=0 EndX=-15.8 EndY=-34.25 EndZ=0
  constraints (10):
    c: Coincident(g1,g0)
    c: Coincident(g1,g0)
    c: Coincident(g3,g2)
    c: Coincident(g3,g2)
    c: Equal(g0,g-3)
    c: Equal(g2,g-4)
    c: Coincident(g2,g-4)
    c: Coincident(g-4,g2)
    c: Coincident(g0,g-3)
    c: Coincident(g0,g-3)
FEATURE [PartDesign::SubShapeBinder] Binder005
  BindCopyOnChange = 0
  BindMode = 0
  ClaimChildren = false
  Context = -> Part001 [Body004.Binder005.]
  Fuse = false
  MakeFace = true
  OffsetFill = false
  OffsetIntersection = false
  OffsetJoinType = 0
  OffsetOpenResult = false
  PartialLoad = false
  Relative = true
  Support = -> [Body003[Sketch025.]]
  _Version = 2
FEATURE [Sketcher::SketchObject] Sketch034
  ArcFitTolerance = 0
  AttachmentOffset = pos=(0,0,35.75) rot=(0,0,1;0rad)
  AttachmentSupport = -> [XZ_Plane005]
  ExternalGeometry = -> [Binder005]
  FullyConstrained = true
  MakeInternals = false
  MapMode = 5
  Placement = pos=(0,-35.75,7.9e-15) rot=(1,0,0;1.5708rad)
  expr: .AttachmentOffset.Base.z = Sketch018.Constraints.BaseLength / 2 + <<Spreadsheet>>.WallThickness
  sketch-geometry (8):
    g0: LineSegment StartX=-16.3 StartY=17.7 StartZ=0 EndX=-17.9 EndY=17.7 EndZ=0
    g1: LineSegment StartX=-17.9 StartY=17.7 StartZ=0 EndX=-17.9 EndY=15.1343 EndZ=0
    g2: LineSegment StartX=-17.9 StartY=15.1343 StartZ=0 EndX=-16.0172 EndY=17.0172 EndZ=0
    g3: LineSegment StartX=16.3 StartY=17.7 StartZ=0 EndX=17.9 EndY=17.7 EndZ=0
    g4: LineSegment StartX=17.9 StartY=17.7 StartZ=0 EndX=17.9 EndY=15.1343 EndZ=0
    g5: LineSegment StartX=17.9 StartY=15.1343 StartZ=0 EndX=16.0172 EndY=17.0172 EndZ=0
    g6: ArcOfCircle CenterX=16.3 CenterY=17.3 CenterZ=0 NormalX=0 NormalY=0 NormalZ=1 AngleXU=0 Radius=0.4 StartAngle=1.5708 EndAngle=3.92699
    g7: ArcOfCircle CenterX=-16.3 CenterY=17.3 CenterZ=0 NormalX=0 NormalY=0 NormalZ=1 AngleXU=0 Radius=0.4 StartAngle=5.49779 EndAngle=7.85398
  constraints (18):
    c: Coincident(g0,g1)
    c: Coincident(g1,g-5)
    c: Coincident(g1,g2)
    c: Coincident(g2,g-5)
    c: Coincident(g0,g-3)
    c: Coincident(g0,g-4)
    c: Coincident(g3,g4)
    c: Coincident(g4,g-8)
    c: Coincident(g4,g5)
    c: Coincident(g5,g-8)
    c: Coincident(g3,g-7)
    c: Coincident(g3,g-6)
    c: Coincident(g6,g5)
    c: Coincident(g6,g3)
    c: Coincident(g7,g0)
    c: Coincident(g7,g2)
    c: Equal(g7,g-4)
    c: Equal(g6,g-7)
FEATURE [Sketcher::SketchObject] Sketch036  label="MSH2C_Push"
  ArcFitTolerance = 0
  AttachmentSupport = -> [XZ_Plane005]
  ExternalGeometry = -> [Binder005]
  FullyConstrained = true
  MakeInternals = false
  MapMode = 5
  Placement = pos=(0,0,0) rot=(1,0,0;1.5708rad)
  expr: Constraints[5] = <<Spreadsheet>>.Tolerance
  sketch-geometry (2):
    g0: ArcOfCircle CenterX=-1.3e-15 CenterY=18.8 CenterZ=0 NormalX=0 NormalY=0 NormalZ=1 AngleXU=0 Radius=10.1 StartAngle=3.14159 EndAngle=6.28319
    g1: LineSegment StartX=-10.1 StartY=18.8 StartZ=0 EndX=10.1 EndY=18.8 EndZ=0
  constraints (6):
    c: Coincident(g1,g0)
    c: Coincident(g1,g0)
    c: Horizontal(g1)
    c: PointOnObject(g-3,g1)
    c: Coincident(g0,g-3)
    c: DistanceX(g0,g-3) = 0.1
FEATURE [PartDesign::Plane] DatumPlane
  AttachmentSupport = -> [Sketch018]
  Length = 60
  MapMode = 7
  Placement = pos=(17.8,34.55,0) rot=(0,0.707107,0.707107;3.14159rad)
  ResizeMode = 0
  Width = 60
FEATURE [Sketcher::SketchObject] Sketch038  label="MSH2B_Button"
  ArcFitTolerance = 0
  AttachmentSupport = -> [DatumPlane]
  ExternalGeometry = -> [Sketch025]
  FullyConstrained = true
  MakeInternals = false
  MapMode = 5
  Placement = pos=(17.8,34.55,0) rot=(0,0.707107,0.707107;3.14159rad)
  sketch-geometry (2):
    g0: ArcOfCircle CenterX=17.8 CenterY=-2.04825e-05 CenterZ=0 NormalX=0 NormalY=0 NormalZ=1 AngleXU=0 Radius=10 StartAngle=2.04825e-06 EndAngle=3.14159
    g1: LineSegment StartX=7.8 StartY=-9.5e-15 StartZ=0 EndX=27.8 EndY=-6.7e-15 EndZ=0
  constraints (5):
    c: Coincident(g0,g-3)
    c: Coincident(g0,g-3)
    c: Equal(g0,g-3)
    c: Coincident(g1,g0)
    c: Coincident(g1,g0)
FEATURE [PartDesign::Pad] Pad016  label="MSH2B_Button_"
  BaseFeature = -> Pad007
  Direction = (0,1,-2e-16)
  Length = 1.3
  Length2 = 10
  Profile = -> Sketch038
  ReferenceAxis = -> Sketch038 [N_Axis]
  Refine = true
  Suppressed = false
  Type = 0
  expr: Length = <<Spreadsheet>>.WallThickness + <<Spreadsheet>>.Tolerance
FEATURE [PartDesign::Fillet] Fillet004
  Base = -> Pad016 [Edge9,Edge1,Face4]
  BaseFeature = -> Pad016
  Radius = 1.2
  SupportTransform = false
  Suppressed = false
  UseAllEdges = false
  expr: Radius = <<Spreadsheet>>.WallThickness
FEATURE [PartDesign::Fillet] Fillet009
  Base = -> Fillet004 [Edge16]
  BaseFeature = -> Fillet004
  Radius = 1
  SupportTransform = false
  Suppressed = false
  UseAllEdges = false
FEATURE [PartDesign::Pocket] Pocket006  label="MSH2B_SDHoles_"
  BaseFeature = -> Fillet009
  Direction = (0,1,-2e-16)
  Length = 1.1
  Length2 = 5
  Profile = -> Sketch021
  ReferenceAxis = -> Sketch021 [N_Axis]
  Suppressed = false
  Type = 0
  expr: Length = <<Spreadsheet>>.SDHoleThickness
FEATURE [PartDesign::LinearPattern] LinearPattern001
  BaseFeature = -> Pocket006
  Direction = -> Y_Axis003
  Length = 60
  Mode = 0
  Occurrences = 16
  Offset = 4
  Originals = -> [Pocket006]
  Suppressed = false
  TransformMode = 0
  expr: Length = <<Spreadsheet>>.SpacingY * (<<Spreadsheet>>.Rows - 1)
  expr: Occurrences = <<Spreadsheet>>.Rows
FEATURE [PartDesign::Chamfer] Chamfer002
  Angle = 45
  Base = -> LinearPattern001 [Face17]
  BaseFeature = -> LinearPattern001
  ChamferType = 0
  FlipDirection = false
  Size = 0.6
  Size2 = 1
  SupportTransform = false
  Suppressed = false
  UseAllEdges = false
FEATURE [PartDesign::Pocket] Pocket008  label="MSH2B_SDRidges_"
  BaseFeature = -> Chamfer002
  Direction = (0,1,-2e-16)
  Length = 5
  Length2 = 5
  Midplane = true
  Profile = -> Sketch026
  ReferenceAxis = -> Sketch026 [N_Axis]
  Suppressed = false
  Type = 1
FEATURE [PartDesign::Pad] Pad008  label="MSH2B_BackWall_"
  BaseFeature = -> Pocket008
  Direction = (0,-1,2e-16)
  Length = 1.6
  Length2 = 10
  Profile = -> Sketch022
  ReferenceAxis = -> Sketch022 [N_Axis]
  Refine = true
  Suppressed = false
  Type = 0
  expr: Length = <<Spreadsheet>>.BackWallThickness
FEATURE [PartDesign::Chamfer] Chamfer003
  Angle = 50
  Base = -> Pad008 [Edge528]
  BaseFeature = -> Pad008
  ChamferType = 1
  FlipDirection = false
  Size = 0.6
  Size2 = 1.2
  SupportTransform = false
  Suppressed = false
  UseAllEdges = false
  expr: Size = (<<Spreadsheet>>.BackWallThickness - 0.4 mm) / 2
  expr: Size2 = <<Spreadsheet>>.BackWallThickness - 0.4 mm
FEATURE [PartDesign::Pocket] Pocket007  label="MSH2B_Ridge_"
  BaseFeature = -> Chamfer003
  Direction = (0,1,-2e-16)
  Length = 5
  Length2 = 5
  Midplane = true
  Profile = -> Sketch023
  ReferenceAxis = -> Sketch023 [N_Axis]
  Suppressed = false
  Type = 1
FEATURE [PartDesign::Pad] Pad009  label="MSH2B_Lock_"
  BaseFeature = -> Pocket007
  Direction = (0,0,1)
  Length = 4
  Length2 = 10
  Profile = -> Sketch024
  ReferenceAxis = -> Sketch024 [N_Axis]
  Suppressed = false
  Type = 0
  expr: Length = <<Spreadsheet>>.RidgeDepth * 2
FEATURE [PartDesign::Body] Body003  label="Base_2"
  AllowCompound = false
  Group = -> [Sketch019,Sketch018,Sketch025,Sketch020,Pad007,DatumPlane,Sketch038,Pad016,Fillet004,Sketch021,Fillet009,Pocket006,LinearPattern001,Sketch022,Chamfer002,Sketch026,Pocket008,Pad008,Sketch023,Chamfer003,Pocket007,Sketch024,Pad009]
  Origin = -> Origin003
  Tip = -> Pad009
FEATURE [PartDesign::Plane] DatumPlane001
  AttachmentSupport = -> [Pad]
  Length = 79.2276
  MapMode = 7
  Placement = pos=(33.8,34.55,11.6) rot=(0,0.707107,0.707107;3.14159rad)
  ResizeMode = 0
  Width = 61.6276
FEATURE [Sketcher::SketchObject] Sketch039  label="MSH4B_Button"
  ArcFitTolerance = 0
  AttachmentSupport = -> [DatumPlane001]
  ExternalGeometry = -> [Sketch011]
  FullyConstrained = true
  MakeInternals = false
  MapMode = 5
  Placement = pos=(33.8,34.55,11.6) rot=(0,0.707107,0.707107;3.14159rad)
  sketch-geometry (2):
    g0: ArcOfCircle CenterX=33.8 CenterY=-11.6 CenterZ=0 NormalX=0 NormalY=0 NormalZ=1 AngleXU=0 Radius=10 StartAngle=2.31381e-06 EndAngle=3.14159
    g1: LineSegment StartX=23.8 StartY=-11.6 StartZ=0 EndX=43.8 EndY=-11.6 EndZ=0
  constraints (5):
    c: Coincident(g0,g-3)
    c: Coincident(g0,g-3)
    c: Equal(g0,g-3)
    c: Coincident(g1,g0)
    c: Coincident(g1,g0)
FEATURE [PartDesign::Pad] Pad017  label="MSH4B_Button_"
  BaseFeature = -> Pad
  Direction = (0,1,-2e-16)
  Length = 1.3
  Length2 = 10
  Profile = -> Sketch039
  ReferenceAxis = -> Sketch039 [N_Axis]
  Suppressed = false
  Type = 0
  expr: Length = <<Spreadsheet>>.WallThickness + <<Spreadsheet>>.Tolerance
FEATURE [PartDesign::Fillet] Fillet
  Base = -> Pad017 [Face5,Edge9,Edge10,Edge2,Edge1]
  BaseFeature = -> Pad017
  Radius = 1.2
  SupportTransform = false
  Suppressed = false
  UseAllEdges = false
  expr: Radius = <<Spreadsheet>>.WallThickness
FEATURE [PartDesign::Fillet] Fillet010
  Base = -> Fillet [Edge28]
  BaseFeature = -> Fillet
  Radius = 1
  SupportTransform = false
  Suppressed = false
  UseAllEdges = false
FEATURE [PartDesign::Pocket] Pocket  label="MSHB_SDHoles_"
  BaseFeature = -> Fillet010
  Direction = (0,1,-2e-16)
  Length = 1.1
  Length2 = 5
  Profile = -> Sketch003
  ReferenceAxis = -> Sketch003 [N_Axis]
  Suppressed = false
  Type = 0
  expr: Length = <<Spreadsheet>>.SDHoleThickness
FEATURE [PartDesign::LinearPattern] LinearPattern
  BaseFeature = -> Pocket
  Direction = -> Y_Axis
  Length = 60
  Mode = 0
  Occurrences = 16
  Offset = 4
  Originals = -> [Pocket]
  Suppressed = false
  TransformMode = 0
  expr: Length = <<Spreadsheet>>.SpacingY * (<<Spreadsheet>>.Rows - 1)
  expr: Occurrences = <<Spreadsheet>>.Rows
FEATURE [PartDesign::Chamfer] Chamfer001
  Angle = 45
  Base = -> LinearPattern [Face22]
  BaseFeature = -> LinearPattern
  ChamferType = 0
  FlipDirection = false
  Size = 0.6
  Size2 = 1
  SupportTransform = false
  Suppressed = false
  UseAllEdges = false
FEATURE [PartDesign::Pocket] Pocket004  label="MSH4B_SDRidges_"
  BaseFeature = -> Chamfer001
  Direction = (0,1,-2e-16)
  Length = 5
  Length2 = 5
  Midplane = true
  Profile = -> Sketch016
  ReferenceAxis = -> Sketch016 [N_Axis]
  Suppressed = false
  Type = 1
FEATURE [PartDesign::Pad] Pad001  label="MSHB_BackWall_"
  BaseFeature = -> Pocket004
  Direction = (0,-1,2e-16)
  Length = 1.6
  Length2 = 10
  Profile = -> Sketch004
  ReferenceAxis = -> Sketch004 [N_Axis]
  Refine = true
  Suppressed = false
  Type = 0
  expr: Length = <<Spreadsheet>>.BackWallThickness
FEATURE [PartDesign::Chamfer] Chamfer
  Angle = 45
  Base = -> Pad001 [Edge530]
  BaseFeature = -> Pad001
  ChamferType = 1
  FlipDirection = false
  Size = 0.6
  Size2 = 1.2
  SupportTransform = false
  Suppressed = false
  UseAllEdges = false
  expr: Size = (<<Spreadsheet>>.BackWallThickness - 0.4 mm) / 2
  expr: Size2 = <<Spreadsheet>>.BackWallThickness - 0.4 mm
FEATURE [PartDesign::Pocket] Pocket001  label="MSHB_Ridge_"
  BaseFeature = -> Chamfer
  Direction = (0,1,-2e-16)
  Length = 5
  Length2 = 5
  Midplane = true
  Profile = -> Sketch005
  ReferenceAxis = -> Sketch005 [N_Axis]
  Suppressed = false
  Type = 1
FEATURE [PartDesign::Pad] Pad002  label="MSHB_Lock_"
  BaseFeature = -> Pocket001
  Direction = (0,0,1)
  Length = 4
  Length2 = 10
  Profile = -> Sketch006
  ReferenceAxis = -> Sketch006 [N_Axis]
  Suppressed = false
  Type = 0
  expr: Length = <<Spreadsheet>>.RidgeDepth * 2
FEATURE [PartDesign::Body] Body  label="Base_4"
  AllowCompound = false
  Group = -> [Sketch,Sketch001,Sketch011,Sketch002,Pad,DatumPlane001,Sketch039,Pad017,Fillet,Sketch003,Fillet010,Pocket,LinearPattern,Sketch004,Chamfer001,Sketch016,Pocket004,Pad001,Sketch005,Chamfer,Pocket001,Sketch006,Pad002]
  Origin = -> Origin
  Tip = -> Fillet010
FEATURE [PartDesign::SubShapeBinder] Binder006
  BindCopyOnChange = 0
  BindMode = 0
  ClaimChildren = false
  Context = -> Part002 [Body007.Binder006.]
  Fuse = false
  MakeFace = true
  OffsetFill = false
  OffsetIntersection = false
  OffsetJoinType = 0
  OffsetOpenResult = false
  PartialLoad = false
  Relative = true
  Support = -> [Body006[Sketch040.]]
  _Version = 2
FEATURE [PartDesign::SubShapeBinder] Binder007
  BindCopyOnChange = 0
  BindMode = 0
  ClaimChildren = false
  Context = -> Part002 [Body007.Binder007.]
  Fuse = false
  MakeFace = true
  OffsetFill = false
  OffsetIntersection = false
  OffsetJoinType = 0
  OffsetOpenResult = false
  PartialLoad = false
  Relative = true
  Support = -> [Body006[Sketch047.]]
  _Version = 2
FEATURE [Sketcher::SketchObject] Sketch040  label="MSH2BS_Template_XY"
  ArcFitTolerance = 0
  AttachmentSupport = -> [XY_Plane009]
  FullyConstrained = true
  MakeInternals = false
  MapMode = 5
  expr: .Constraints.BaseLength = <<Spreadsheet>>.SpacingY * (<<Spreadsheet>>.Rows_short - 1) + <<Spreadsheet>>.SDHoleThickness + 2 * <<Spreadsheet>>.Margin
  expr: .Constraints.Width = <<Spreadsheet>>.SpacingX * (<<Spreadsheet>>.Columns_2 - 1) + <<Spreadsheet>>.SDHoleWidth + 2 * <<Spreadsheet>>.Margin
  expr: Constraints[42] = <<Spreadsheet>>.LockRadius
  expr: Constraints[43] = <<Spreadsheet>>.LockRadius + <<Spreadsheet>>.Tolerance
  expr: Constraints[54] = <<Spreadsheet>>.Tolerance * 1.5
  expr: Constraints[58] = <<Spreadsheet>>.BackWallThickness
  expr: Constraints[63] = <<Spreadsheet>>.RidgeDepth
  expr: Constraints[66] = <<Spreadsheet>>.Tolerance
  sketch-geometry (22):
    g0: LineSegment StartX=17.8 StartY=12.55 StartZ=0 EndX=17.8 EndY=-14.15 EndZ=0
    g1: LineSegment StartX=17.8 StartY=-14.15 StartZ=0 EndX=-17.8 EndY=-14.15 EndZ=0
    g2: LineSegment StartX=-17.8 StartY=-14.15 StartZ=0 EndX=-17.8 EndY=12.55 EndZ=0
    g3: LineSegment StartX=-17.8 StartY=2e-16 StartZ=0 EndX=17.8 EndY=2e-16 EndZ=0
    g4: LineSegment StartX=6e-16 StartY=12.55 StartZ=0 EndX=6e-16 EndY=-14.15 EndZ=0
    g5: LineSegment StartX=-17.8 StartY=12.55 StartZ=0 EndX=-15.8 EndY=12.55 EndZ=0
    g6: LineSegment StartX=-15.8 StartY=12.55 StartZ=0 EndX=15.8 EndY=12.55 EndZ=0
    g7: ArcOfCircle CenterX=-15.8 CenterY=-10.55 CenterZ=0 NormalX=0 NormalY=0 NormalZ=1 AngleXU=0 Radius=1.6 StartAngle=1.5708 EndAngle=4.71239
    g8: LineSegment StartX=-15.8 StartY=-14.15 StartZ=0 EndX=-15.8 EndY=12.55 EndZ=0
    g9: ArcOfCircle CenterX=-15.8 CenterY=-10.55 CenterZ=0 NormalX=0 NormalY=0 NormalZ=1 AngleXU=0 Radius=1.7 StartAngle=1.5708 EndAngle=4.71239
    g10: LineSegment StartX=15.8 StartY=12.55 StartZ=0 EndX=15.8 EndY=-14.15 EndZ=0
    g11: ArcOfCircle CenterX=15.8 CenterY=-10.55 CenterZ=0 NormalX=0 NormalY=0 NormalZ=1 AngleXU=0 Radius=1.6 StartAngle=4.71239 EndAngle=7.85398
    g12: ArcOfCircle CenterX=15.8 CenterY=-10.55 CenterZ=0 NormalX=0 NormalY=0 NormalZ=1 AngleXU=0 Radius=1.7 StartAngle=4.71239 EndAngle=7.85398
    g13: LineSegment [constr] StartX=-15.8 StartY=-10.55 StartZ=0 EndX=15.8 EndY=-10.55 EndZ=0
    g14: LineSegment StartX=15.8 StartY=12.55 StartZ=0 EndX=17.8 EndY=12.55 EndZ=0
    g15: LineSegment StartX=-17.9 StartY=-14.15 StartZ=0 EndX=-17.9 EndY=12.7 EndZ=0
    g16: LineSegment StartX=-17.9 StartY=12.7 StartZ=0 EndX=17.9 EndY=12.7 EndZ=0
    g17: LineSegment StartX=17.9 StartY=12.7 StartZ=0 EndX=17.9 EndY=-14.15 EndZ=0
    g18: LineSegment [constr] StartX=17.8 StartY=12.55 StartZ=0 EndX=17.8 EndY=12.7 EndZ=0
    g19: LineSegment StartX=-17.8 StartY=-12.55 StartZ=0 EndX=17.8 EndY=-12.55 EndZ=0
    g20: LineSegment [constr] StartX=-17.9 StartY=-14.15 StartZ=0 EndX=-17.8 EndY=-14.15 EndZ=0
    g21: LineSegment [constr] StartX=17.8 StartY=-14.15 StartZ=0 EndX=17.9 EndY=-14.15 EndZ=0
  constraints (70):
    c: Coincident(g0,g1)
    c: Coincident(g1,g2)
    c: Coincident(g2,g5)
    c: Horizontal(g1)
    c: Vertical(g0)
    c: Vertical(g2)
    c: DistanceX(g5,g0) = 35.6  'Width'
    c: PointOnObject(g3,g2)
    c: PointOnObject(g3,g0)
    c: PointOnObject(g4,g1)
    c: Symmetric(g1,g0,g4)
    c: Coincident(g5,g6)
    c: Horizontal(g5)
    c: PointOnObject(g4,g6)
    c: Coincident(g8,g5)
    c: Vertical(g8)
    c: PointOnObject(g7,g8)
    c: PointOnObject(g7,g8)
    c: Coincident(g9,g7)
    c: PointOnObject(g9,g8)
    c: Vertical(g10)
    c: PointOnObject(g11,g10)
    c: PointOnObject(g11,g10)
    c: Coincident(g12,g11)
    c: PointOnObject(g12,g10)
    c: Equal(g7,g11)
    c: Equal(g12,g9)
    c: PointOnObject(g8,g1)
    c: PointOnObject(g9,g8)
    c: PointOnObject(g7,g8)
    c: DistanceY(g8,g7) = 2
    c: PointOnObject(g10,g1)
    c: PointOnObject(g12,g10)
    c: PointOnObject(g11,g10)
    c: Coincident(g13,g7)
    c: Coincident(g13,g11)
    c: Horizontal(g13)
    c: Coincident(g6,g10)
    c: Coincident(g14,g6)
    c: Coincident(g14,g0)
    c: Horizontal(g14)
    c: Symmetric(g5,g6,g4)
    c: Radius(g7) = 1.6
    c: Radius(g9) = 1.7
    c: Vertical(g15)
    c: Coincident(g15,g16)
    c: Horizontal(g16)
    c: Coincident(g16,g17)
    c: Vertical(g17)
    c: PointOnObject(g17,g1)
    c: PointOnObject(g15,g1)
    c: Coincident(g18,g0)
    c: PointOnObject(g18,g16)
    c: Vertical(g18)
    c: DistanceY(g18,g18) = 0.15
    c: DistanceY(g15,g15) = 26.85  'CoverLength'
    c: PointOnObject(g19,g2)
    c: Horizontal(g19)
    c: DistanceY(g1,g19) = 1.6
    c: Symmetric(g19,g0,g-1)  '__ANCHOR__'
    c: DistanceY(g19,g2) = 25.1  'BaseLength'
    c: Symmetric(g19,g0,g3)
    c: Horizontal(g3)
    c: DistanceX(g1,g8) = 2
    c: Coincident(g20,g15)
    c: Coincident(g1,g20)
    c: DistanceX(g20,g20) = 0.1
    c: Coincident(g21,g0)
    c: Coincident(g21,g17)
    c: Equal(g21,g20)
FEATURE [PartDesign::Plane] DatumPlane002
  AttachmentSupport = -> [Sketch040]
  Length = 60
  MapMode = 7
  Placement = pos=(17.8,12.55,0) rot=(0,0.707107,0.707107;3.14159rad)
  ResizeMode = 0
  Width = 60
FEATURE [Sketcher::SketchObject] Sketch042  label="MSH2B_Foundation003"
  ArcFitTolerance = 0
  AttachmentSupport = -> [XY_Plane009]
  ExternalGeometry = -> [Sketch040]
  FullyConstrained = true
  MakeInternals = false
  MapMode = 5
  sketch-geometry (4):
    g0: LineSegment StartX=17.8 StartY=12.55 StartZ=0 EndX=17.8 EndY=-14.15 EndZ=0
    g1: LineSegment StartX=17.8 StartY=-14.15 StartZ=0 EndX=-17.8 EndY=-14.15 EndZ=0
    g2: LineSegment StartX=-17.8 StartY=-14.15 StartZ=0 EndX=-17.8 EndY=12.55 EndZ=0
    g3: LineSegment StartX=-17.8 StartY=12.55 StartZ=0 EndX=17.8 EndY=12.55 EndZ=0
  constraints (8):
    c: Coincident(g0,g1)
    c: Coincident(g1,g2)
    c: Coincident(g2,g3)
    c: Coincident(g3,g0)
    c: Coincident(g0,g-4)
    c: Coincident(g0,g-4)
    c: Coincident(g2,g-3)
    c: Coincident(g1,g-3)
FEATURE [PartDesign::Pad] Pad018  label="MSH2BS_Foundation"
  Direction = (0,0,1)
  Length = 11.6
  Length2 = 10
  Profile = -> Sketch042
  ReferenceAxis = -> Sketch042 [N_Axis]
  Suppressed = false
  Type = 0
  expr: Length = <<Spreadsheet>>.BaseHeight
FEATURE [Sketcher::SketchObject] Sketch046  label="MSH2BS_Lock"
  ArcFitTolerance = 0
  AttachmentOffset = pos=(0,0,1) rot=(0,0,1;0rad)
  AttachmentSupport = -> [XY_Plane009]
  ExternalGeometry = -> [Sketch040]
  FullyConstrained = true
  MakeInternals = false
  MapMode = 5
  Placement = pos=(0,0,1) rot=(0,0,1;0rad)
  expr: .AttachmentOffset.Base.z = <<Spreadsheet>>.RidgeOffset
  sketch-geometry (4):
    g0: ArcOfCircle CenterX=-15.8 CenterY=-10.55 CenterZ=0 NormalX=0 NormalY=0 NormalZ=1 AngleXU=0 Radius=1.6 StartAngle=1.5708 EndAngle=4.71239
    g1: ArcOfCircle CenterX=15.8 CenterY=-10.55 CenterZ=0 NormalX=0 NormalY=0 NormalZ=1 AngleXU=0 Radius=1.6 StartAngle=4.71239 EndAngle=7.85398
    g2: LineSegment StartX=15.8 StartY=-8.95 StartZ=0 EndX=15.8 EndY=-12.15 EndZ=0
    g3: LineSegment StartX=-15.8 StartY=-8.95 StartZ=0 EndX=-15.8 EndY=-12.15 EndZ=0
  constraints (10):
    c: Coincident(g2,g1)
    c: Coincident(g2,g1)
    c: Coincident(g3,g0)
    c: Coincident(g3,g0)
    c: Coincident(g1,g-4)
    c: Coincident(g1,g-4)
    c: Equal(g1,g-4)
    c: Coincident(g0,g-3)
    c: Coincident(g0,g-3)
    c: Equal(g0,g-3)
FEATURE [Sketcher::SketchObject] Sketch047  label="MSH2BS_Template_XZ"
  ArcFitTolerance = 0
  AttachmentSupport = -> [XZ_Plane009]
  FullyConstrained = true
  MakeInternals = false
  MapMode = 5
  Placement = pos=(0,0,0) rot=(1,0,0;1.5708rad)
  expr: Constraints[13] = <<Spreadsheet>>.Tolerance
  expr: Constraints[29] = <<Spreadsheet>>.SDOffset + <<Spreadsheet>>.SDHeight + 1 mm
  expr: Constraints[39] = <<Spreadsheet>>.SDFree + 1 mm
  expr: Constraints[46] = <<Spreadsheet>>.RidgeOffset
  expr: Constraints[58] = <<Spreadsheet>>.RidgeDepth
  expr: Constraints[6] = <<MSH2BS_Template_XY>>.Constraints.Width
  sketch-geometry (29):
    g0: LineSegment StartX=-17.8 StartY=0 StartZ=0 EndX=17.8 EndY=0 EndZ=0
    g1: LineSegment StartX=17.8 StartY=11.6 StartZ=0 EndX=-17.8 EndY=11.6 EndZ=0
    g2: LineSegment [constr] StartX=-17.8 StartY=0 StartZ=0 EndX=-17.9 EndY=0 EndZ=0
    g3: LineSegment [constr] StartX=17.8 StartY=0 StartZ=0 EndX=17.9 EndY=0 EndZ=0
    g4: LineSegment StartX=-17.8 StartY=1 StartZ=0 EndX=-17.8 EndY=0 EndZ=0
    g5: LineSegment StartX=-17.8 StartY=11.6 StartZ=0 EndX=-17.8 EndY=3.70711 EndZ=0
    g6: LineSegment StartX=-17.8 StartY=3.70711 StartZ=0 EndX=-17.8 EndY=1 EndZ=0
    g7: LineSegment StartX=-17.9 StartY=1.1 StartZ=0 EndX=-16.3 EndY=1.1 EndZ=0
    g8: LineSegment StartX=-16.0172 StartY=1.78284 StartZ=0 EndX=-17.9 EndY=3.66569 EndZ=0
    g9: LineSegment StartX=17.8 StartY=0 StartZ=0 EndX=17.8 EndY=1 EndZ=0
    g10: LineSegment StartX=17.8 StartY=1 StartZ=0 EndX=17.8 EndY=11.6 EndZ=0
    g11: LineSegment StartX=17.8 StartY=1 StartZ=0 EndX=16.3 EndY=1 EndZ=0
    g12: LineSegment StartX=15.9464 StartY=1.85355 StartZ=0 EndX=17.8 EndY=3.70711 EndZ=0
    g13: LineSegment StartX=-17.9 StartY=17.6 StartZ=0 EndX=17.9 EndY=17.6 EndZ=0
    g14: LineSegment StartX=-17.8 StartY=1 StartZ=0 EndX=-16.3 EndY=1 EndZ=0
    g15: LineSegment StartX=-15.9464 StartY=1.85355 StartZ=0 EndX=-17.8 EndY=3.70711 EndZ=0
    g16: LineSegment StartX=17.9 StartY=3.66569 StartZ=0 EndX=16.0172 EndY=1.78284 EndZ=0
    g17: LineSegment StartX=16.3 StartY=1.1 StartZ=0 EndX=17.9 EndY=1.1 EndZ=0
    g18: LineSegment StartX=-17.9 StartY=0 StartZ=0 EndX=-17.9 EndY=1.1 EndZ=0
    g19: LineSegment StartX=-17.9 StartY=1.1 StartZ=0 EndX=-17.9 EndY=17.6 EndZ=0
    g20: LineSegment StartX=17.9 StartY=17.6 StartZ=0 EndX=17.9 EndY=1.1 EndZ=0
    g21: LineSegment StartX=17.9 StartY=1.1 StartZ=0 EndX=17.9 EndY=0 EndZ=0
    g22: ArcOfCircle CenterX=-1.1e-15 CenterY=0 CenterZ=0 NormalX=0 NormalY=0 NormalZ=1 AngleXU=0 Radius=10 StartAngle=0 EndAngle=3.14159
    g23: ArcOfCircle CenterX=-16.3 CenterY=1.5 CenterZ=0 NormalX=0 NormalY=0 NormalZ=1 AngleXU=0 Radius=0.4 StartAngle=4.71239 EndAngle=7.06858
    g24: LineSegment [constr] StartX=-16.3 StartY=1.5 StartZ=0 EndX=-15.8 EndY=1.5 EndZ=0
    g25: LineSegment [constr] StartX=-16.3 StartY=1.1 StartZ=0 EndX=-16.3 EndY=1 EndZ=0
    g26: ArcOfCircle CenterX=-16.3 CenterY=1.5 CenterZ=0 NormalX=0 NormalY=0 NormalZ=1 AngleXU=0 Radius=0.5 StartAngle=4.71239 EndAngle=7.06858
    g27: ArcOfCircle CenterX=16.3 CenterY=1.5 CenterZ=0 NormalX=0 NormalY=0 NormalZ=1 AngleXU=0 Radius=0.5 StartAngle=2.35619 EndAngle=4.71239
    g28: ArcOfCircle CenterX=16.3 CenterY=1.5 CenterZ=0 NormalX=0 NormalY=0 NormalZ=1 AngleXU=0 Radius=0.4 StartAngle=2.35619 EndAngle=4.71239
  constraints (79):
    c: Coincident(g0,g9)
    c: Coincident(g10,g1)
    c: Coincident(g1,g5)
    c: Coincident(g4,g0)
    c: Horizontal(g0)
    c: Horizontal(g1)
    c: DistanceX(g1,g1) = 35.6
    c: Symmetric(g0,g0,g-1)  '__ANCHOR__'
    c: Coincident(g2,g0)
    c: Horizontal(g2)
    c: Coincident(g3,g0)
    c: Horizontal(g3)
    c: Equal(g3,g2)
    c: DistanceX(g2,g2) = 0.1
    c: Vertical(g4)
    c: Coincident(g5,g6)
    c: Vertical(g5)
    c: Vertical(g6)
    c: Coincident(g9,g10)
    c: Vertical(g9)
    c: Vertical(g10)
    c: Equal(g4,g9)
    c: Coincident(g9,g11)
    c: PointOnObject(g12,g10)
    c: Coincident(g2,g18)
    c: Coincident(g19,g13)
    c: Horizontal(g13)
    c: Coincident(g13,g20)
    c: Coincident(g21,g3)
    c: DistanceY(g18,g19) = 17.6
    c: Coincident(g18,g19)
    c: Vertical(g18)
    c: Vertical(g19)
    c: Coincident(g20,g21)
    c: Vertical(g20)
    c: Vertical(g21)
    c: PointOnObject(g16,g20)
    c: Coincident(g17,g20)
    c: Equal(g21,g18)
    c: DistanceY(g1,g13) = 6
    c: Parallel(g15,g8)
    c: PointOnObject(g22,g0)
    c: PointOnObject(g22,g0)
    c: Symmetric(g0,g0,g22)
    c: Radius(g22) = 10
    c: Horizontal(g7)
    c: DistanceY(g2,g4) = 1
    c: Tangent(g7,g23) = -1.5708
    c: Tangent(g8,g23) = -1.5708
    c: Horizontal(g14)
    c: Coincident(g4,g6)
    c: Coincident(g24,g23)
    c: Horizontal(g24)
    c: Coincident(g25,g7)
    c: Equal(g2,g25)
    c: Coincident(g26,g23)
    c: Tangent(g14,g26) = -1.5708
    c: Tangent(g15,g26) = -1.5708
    c: DistanceX(g5,g24) = 2
    c: Horizontal(g11)
    c: Horizontal(g17)
    c: Coincident(g28,g27)
    c: Tangent(g28,g17) = -1.5708
    c: Tangent(g12,g27) = 1.5708
    c: Tangent(g16,g28) = -1.5708
    c: Coincident(g14,g4)
    c: Coincident(g7,g18)
    c: Coincident(g25,g14)
    c: Radius(g23) = 0.4
    c: PointOnObject(g8,g19)
    c: PointOnObject(g24,g26)
    c: Angle(g8,g7) = 0.785398
    c: Coincident(g5,g15)
    c: Equal(g28,g23)
    c: Equal(g11,g14)
    c: Equal(g7,g17)
    c: Equal(g16,g8)
    c: Equal(g15,g12)
    c: Coincident(g27,g11)
FEATURE [Sketcher::SketchObject] Sketch044  label="MSH2BS_BackWall"
  ArcFitTolerance = 0
  AttachmentOffset = pos=(0,0,12.55) rot=(0,0,1;0rad)
  AttachmentSupport = -> [XZ_Plane009]
  ExternalGeometry = -> [Sketch047]
  FullyConstrained = true
  MakeInternals = false
  MapMode = 5
  Placement = pos=(0,-12.55,2.8e-15) rot=(1,0,0;1.5708rad)
  expr: .AttachmentOffset.Base.z = Sketch040.Constraints.BaseLength / 2
  expr: Constraints[9] = <<Spreadsheet>>.Tolerance
  sketch-geometry (4):
    g0: LineSegment StartX=-17.8 StartY=0 StartZ=0 EndX=17.8 EndY=0 EndZ=0
    g1: LineSegment StartX=17.8 StartY=0 StartZ=0 EndX=17.8 EndY=17.5 EndZ=0
    g2: LineSegment StartX=17.8 StartY=17.5 StartZ=0 EndX=-17.8 EndY=17.5 EndZ=0
    g3: LineSegment StartX=-17.8 StartY=17.5 StartZ=0 EndX=-17.8 EndY=0 EndZ=0
  constraints (10):
    c: Coincident(g0,g1)
    c: Coincident(g1,g2)
    c: Coincident(g2,g3)
    c: Coincident(g3,g0)
    c: Horizontal(g2)
    c: Vertical(g1)
    c: Vertical(g3)
    c: Coincident(g0,g-3)
    c: Coincident(g0,g-3)
    c: DistanceY(g1,g-4) = 0.1
FEATURE [Sketcher::SketchObject] Sketch045  label="MSH2BS_Ridge"
  ArcFitTolerance = 0
  AttachmentSupport = -> [XZ_Plane009]
  ExternalGeometry = -> [Sketch047]
  FullyConstrained = true
  MakeInternals = false
  MapMode = 5
  Placement = pos=(0,0,0) rot=(1,0,0;1.5708rad)
  sketch-geometry (8):
    g0: LineSegment StartX=15.9464 StartY=1.85355 StartZ=0 EndX=17.8 EndY=3.70711 EndZ=0
    g1: LineSegment StartX=17.8 StartY=3.70711 StartZ=0 EndX=17.8 EndY=1 EndZ=0
    g2: LineSegment StartX=17.8 StartY=1 StartZ=0 EndX=16.3 EndY=1 EndZ=0
    g3: LineSegment StartX=-16.3 StartY=1 StartZ=0 EndX=-17.8 EndY=1 EndZ=0
    g4: LineSegment StartX=-17.8 StartY=1 StartZ=0 EndX=-17.8 EndY=3.70711 EndZ=0
    g5: LineSegment StartX=-17.8 StartY=3.70711 StartZ=0 EndX=-15.9464 EndY=1.85355 EndZ=0
    g6: ArcOfCircle CenterX=-16.3 CenterY=1.5 CenterZ=0 NormalX=0 NormalY=0 NormalZ=1 AngleXU=0 Radius=0.5 StartAngle=4.71239 EndAngle=7.06858
    g7: ArcOfCircle CenterX=16.3 CenterY=1.5 CenterZ=0 NormalX=0 NormalY=0 NormalZ=1 AngleXU=0 Radius=0.5 StartAngle=2.35619 EndAngle=4.71239
  constraints (18):
    c: Coincident(g-8,g0)
    c: Coincident(g0,g-8)
    c: Coincident(g0,g1)
    c: Coincident(g1,g-6)
    c: Coincident(g1,g2)
    c: Coincident(g2,g-7)
    c: Coincident(g-5,g3)
    c: Coincident(g3,g-5)
    c: Coincident(g3,g4)
    c: Coincident(g4,g-3)
    c: Coincident(g4,g5)
    c: Coincident(g5,g-4)
    c: Coincident(g6,g-4)
    c: Coincident(g6,g3)
    c: Coincident(g7,g2)
    c: Coincident(g7,g0)
    c: Equal(g7,g-7)
    c: Equal(g6,g-4)
FEATURE [Sketcher::SketchObject] Sketch048  label="MSH2BS_SDRidges"
  ArcFitTolerance = 0
  AttachmentSupport = -> [XZ_Plane009]
  FullyConstrained = true
  MakeInternals = false
  MapMode = 5
  Placement = pos=(0,0,0) rot=(1,0,0;1.5708rad)
  sketch-geometry (7):
    g0: ArcOfCircle CenterX=-8 CenterY=19.2444 CenterZ=0 NormalX=0 NormalY=0 NormalZ=1 AngleXU=0 Radius=9 StartAngle=4.15641 EndAngle=5.26837
    g1: ArcOfCircle CenterX=8 CenterY=19.2444 CenterZ=0 NormalX=0 NormalY=0 NormalZ=1 AngleXU=0 Radius=9 StartAngle=4.15641 EndAngle=5.26837
    g2: LineSegment StartX=-12.75 StartY=11.6 StartZ=0 EndX=-3.25 EndY=11.6 EndZ=0
    g3: LineSegment StartX=3.25 StartY=11.6 StartZ=0 EndX=12.75 EndY=11.6 EndZ=0
    g4: LineSegment [constr] StartX=-8 StartY=19.2444 StartZ=0 EndX=-8 EndY=10.2444 EndZ=0
    g5: LineSegment [constr] StartX=8 StartY=19.2444 StartZ=0 EndX=8 EndY=10.2444 EndZ=0
    g6: LineSegment [constr] StartX=-8 StartY=19.2444 StartZ=0 EndX=8 EndY=19.2444 EndZ=0
  constraints (20):
    c: Equal(g0,g1)
    c: Coincident(g2,g0)
    c: Coincident(g2,g0)
    c: Coincident(g3,g1)
    c: Coincident(g3,g1)
    c: Coincident(g4,g0)
    c: PointOnObject(g4,g0)
    c: Coincident(g5,g1)
    c: PointOnObject(g5,g1)
    c: Horizontal(g6)
    c: Radius(g0) = 9
    c: PointOnObject(g0,g-3)
    c: PointOnObject(g0,g-3)
    c: PointOnObject(g1,g-3)
    c: PointOnObject(g1,g-3)
    c: DistanceX(g-3,g0) = 1
    c: Coincident(g0,g6)
    c: Symmetric(g-5,g-4,g4)
    c: Symmetric(g-6,g-7,g5)
    c: Coincident(g6,g1)
FEATURE [Sketcher::SketchObject] Sketch049  label="MSH2CS_Top"
  ArcFitTolerance = 0
  AttachmentSupport = -> [XY_Plane010]
  ExternalGeometry = -> [Binder006]
  FullyConstrained = true
  MakeInternals = false
  MapMode = 5
  sketch-geometry (4):
    g0: LineSegment StartX=-17.9 StartY=12.7 StartZ=0 EndX=17.9 EndY=12.7 EndZ=0
    g1: LineSegment StartX=17.9 StartY=12.7 StartZ=0 EndX=17.9 EndY=-14.15 EndZ=0
    g2: LineSegment StartX=17.9 StartY=-14.15 StartZ=0 EndX=-17.9 EndY=-14.15 EndZ=0
    g3: LineSegment StartX=-17.9 StartY=-14.15 StartZ=0 EndX=-17.9 EndY=12.7 EndZ=0
  constraints (8):
    c: Coincident(g0,g1)
    c: Coincident(g1,g2)
    c: Coincident(g2,g3)
    c: Coincident(g3,g0)
    c: Coincident(g1,g-4)
    c: Coincident(g2,g-3)
    c: Coincident(g0,g-3)
    c: Coincident(g0,g-4)
FEATURE [PartDesign::Pad] Pad021  label="MSH2CS_Top_"
  Direction = (0,0,1)
  Length = 1.2
  Length2 = 10
  Profile = -> Sketch049
  ReferenceAxis = -> Sketch049 [N_Axis]
  Suppressed = false
  Type = 0
  expr: Length = <<Spreadsheet>>.WallThickness
FEATURE [Sketcher::SketchObject] Sketch050  label="MSH2CS_Walls"
  ArcFitTolerance = 0
  AttachmentSupport = -> [XY_Plane010]
  ExternalGeometry = -> [Binder006]
  FullyConstrained = true
  MakeInternals = false
  MapMode = 5
  expr: Constraints[10] = <<Spreadsheet>>.WallThickness
  sketch-geometry (9):
    g0: LineSegment StartX=-17.9 StartY=-14.15 StartZ=0 EndX=-19.1 EndY=-14.15 EndZ=0
    g1: LineSegment StartX=-19.1 StartY=-14.15 StartZ=0 EndX=-19.1 EndY=13.9 EndZ=0
    g2: LineSegment StartX=-19.1 StartY=13.9 StartZ=0 EndX=19.1 EndY=13.9 EndZ=0
    g3: LineSegment StartX=19.1 StartY=13.9 StartZ=0 EndX=19.1 EndY=-14.15 EndZ=0
    g4: LineSegment StartX=17.9 StartY=-14.15 StartZ=0 EndX=17.9 EndY=12.7 EndZ=0
    g5: LineSegment StartX=17.9 StartY=12.7 StartZ=0 EndX=-17.9 EndY=12.7 EndZ=0
    g6: LineSegment StartX=-17.9 StartY=12.7 StartZ=0 EndX=-17.9 EndY=-14.15 EndZ=0
    g7: LineSegment StartX=17.9 StartY=-14.15 StartZ=0 EndX=19.1 EndY=-14.15 EndZ=0
    g8: LineSegment [constr] StartX=-17.9 StartY=12.7 StartZ=0 EndX=-17.9 EndY=13.9 EndZ=0
  constraints (23):
    c: Horizontal(g0)
    c: Coincident(g0,g1)
    c: Vertical(g1)
    c: Coincident(g1,g2)
    c: Horizontal(g2)
    c: Coincident(g2,g3)
    c: Vertical(g3)
    c: Coincident(g4,g5)
    c: Coincident(g5,g6)
    c: Coincident(g6,g0)
    c: DistanceX(g0,g0) = 1.2
    c: Coincident(g7,g4)
    c: Coincident(g7,g3)
    c: Horizontal(g7)
    c: Coincident(g4,g-4)
    c: Coincident(g4,g-4)
    c: Coincident(g5,g-3)
    c: Coincident(g0,g-3)
    c: Coincident(g8,g5)
    c: PointOnObject(g8,g2)
    c: Vertical(g8)
    c: Equal(g0,g7)
    c: Equal(g7,g8)
FEATURE [PartDesign::Pad] Pad022  label="MSH2CS_Walls_"
  BaseFeature = -> Pad021
  Direction = (0,0,1)
  Length = 18.8
  Length2 = 10
  Profile = -> Sketch050
  ReferenceAxis = -> Sketch050 [N_Axis]
  Suppressed = false
  Type = 0
  expr: Length = <<Spreadsheet>>.SDOffset + <<Spreadsheet>>.SDHeight + 1 mm + <<Spreadsheet>>.WallThickness
FEATURE [Sketcher::SketchObject] Sketch051
  ArcFitTolerance = 0
  AttachmentOffset = pos=(0,0,13.75) rot=(0,0,1;0rad)
  AttachmentSupport = -> [XZ_Plane010]
  ExternalGeometry = -> [Binder007]
  FullyConstrained = true
  MakeInternals = false
  MapMode = 5
  Placement = pos=(0,-13.75,3.1e-15) rot=(1,0,0;1.5708rad)
  expr: .AttachmentOffset.Base.z = Sketch040.Constraints.BaseLength / 2 + <<Spreadsheet>>.WallThickness
  sketch-geometry (8):
    g0: LineSegment StartX=-16.0172 StartY=17.0172 StartZ=0 EndX=-17.9 EndY=15.1343 EndZ=0
    g1: LineSegment StartX=-17.9 StartY=15.1343 StartZ=0 EndX=-17.9 EndY=17.7 EndZ=0
    g2: LineSegment StartX=-17.9 StartY=17.7 StartZ=0 EndX=-16.3 EndY=17.7 EndZ=0
    g3: LineSegment StartX=16.3 StartY=17.7 StartZ=0 EndX=17.9 EndY=17.7 EndZ=0
    g4: LineSegment StartX=17.9 StartY=17.7 StartZ=0 EndX=17.9 EndY=15.1343 EndZ=0
    g5: LineSegment StartX=17.9 StartY=15.1343 StartZ=0 EndX=16.0172 EndY=17.0172 EndZ=0
    g6: ArcOfCircle CenterX=16.3 CenterY=17.3 CenterZ=0 NormalX=0 NormalY=0 NormalZ=1 AngleXU=0 Radius=0.4 StartAngle=1.5708 EndAngle=3.92699
    g7: ArcOfCircle CenterX=-16.3 CenterY=17.3 CenterZ=0 NormalX=0 NormalY=0 NormalZ=1 AngleXU=0 Radius=0.4 StartAngle=5.49779 EndAngle=7.85398
  constraints (18):
    c: Coincident(g-5,g0)
    c: Coincident(g0,g-5)
    c: Coincident(g0,g1)
    c: Coincident(g1,g-3)
    c: Coincident(g1,g2)
    c: Coincident(g2,g-4)
    c: Coincident(g-7,g3)
    c: Coincident(g3,g-6)
    c: Coincident(g3,g4)
    c: Coincident(g4,g-8)
    c: Coincident(g4,g5)
    c: Coincident(g5,g-8)
    c: Coincident(g6,g3)
    c: Coincident(g6,g5)
    c: Coincident(g7,g2)
    c: Coincident(g7,g0)
    c: Equal(g7,g-4)
    c: Equal(g6,g-7)
FEATURE [Sketcher::SketchObject] Sketch052
  ArcFitTolerance = 0
  AttachmentOffset = pos=(0,0,17.8) rot=(0,0,1;0rad)
  AttachmentSupport = -> [XY_Plane010]
  ExternalGeometry = -> [Binder006]
  FullyConstrained = true
  MakeInternals = false
  MapMode = 5
  Placement = pos=(0,0,17.8) rot=(0,0,1;0rad)
  expr: .AttachmentOffset.Base.z = <<Spreadsheet>>.SDOffset + <<Spreadsheet>>.SDHeight + 1 mm + <<Spreadsheet>>.WallThickness - <<Spreadsheet>>.RidgeOffset
  sketch-geometry (4):
    g0: ArcOfCircle CenterX=15.8 CenterY=-10.55 CenterZ=0 NormalX=0 NormalY=0 NormalZ=1 AngleXU=0 Radius=1.7 StartAngle=4.71239 EndAngle=7.85398
    g1: LineSegment StartX=15.8 StartY=-8.85 StartZ=0 EndX=15.8 EndY=-12.25 EndZ=0
    g2: ArcOfCircle CenterX=-15.8 CenterY=-10.55 CenterZ=0 NormalX=0 NormalY=0 NormalZ=1 AngleXU=0 Radius=1.7 StartAngle=1.5708 EndAngle=4.71239
    g3: LineSegment StartX=-15.8 StartY=-8.85 StartZ=0 EndX=-15.8 EndY=-12.25 EndZ=0
  constraints (10):
    c: Coincident(g1,g0)
    c: Coincident(g1,g0)
    c: Coincident(g3,g2)
    c: Coincident(g3,g2)
    c: Equal(g0,g-3)
    c: Equal(g2,g-4)
    c: Coincident(g2,g-4)
    c: Coincident(g-4,g2)
    c: Coincident(g0,g-3)
    c: Coincident(g0,g-3)
FEATURE [Sketcher::SketchObject] Sketch053  label="MSH2CS_Push"
  ArcFitTolerance = 0
  AttachmentSupport = -> [XZ_Plane010]
  ExternalGeometry = -> [Binder007]
  FullyConstrained = true
  MakeInternals = false
  MapMode = 5
  Placement = pos=(0,0,0) rot=(1,0,0;1.5708rad)
  expr: Constraints[5] = <<Spreadsheet>>.Tolerance
  sketch-geometry (2):
    g0: ArcOfCircle CenterX=-1.3e-15 CenterY=18.8 CenterZ=0 NormalX=0 NormalY=0 NormalZ=1 AngleXU=0 Radius=10.1 StartAngle=3.14159 EndAngle=6.28319
    g1: LineSegment StartX=-10.1 StartY=18.8 StartZ=0 EndX=10.1 EndY=18.8 EndZ=0
  constraints (6):
    c: Coincident(g1,g0)
    c: Coincident(g1,g0)
    c: Horizontal(g1)
    c: PointOnObject(g-3,g1)
    c: Coincident(g0,g-3)
    c: DistanceX(g0,g-3) = 0.1
FEATURE [Sketcher::SketchObject] Sketch054  label="MSH2BS_Button"
  ArcFitTolerance = 0
  AttachmentSupport = -> [DatumPlane002]
  ExternalGeometry = -> [Sketch047]
  FullyConstrained = true
  MakeInternals = false
  MapMode = 5
  Placement = pos=(17.8,12.55,0) rot=(0,0.707107,0.707107;3.14159rad)
  sketch-geometry (2):
    g0: ArcOfCircle CenterX=17.8 CenterY=-2.04825e-05 CenterZ=0 NormalX=0 NormalY=0 NormalZ=1 AngleXU=0 Radius=10 StartAngle=2.04825e-06 EndAngle=3.14159
    g1: LineSegment StartX=7.8 StartY=-7e-16 StartZ=0 EndX=27.8 EndY=-1.8e-15 EndZ=0
  constraints (5):
    c: Coincident(g0,g-3)
    c: Coincident(g0,g-3)
    c: Equal(g0,g-3)
    c: Coincident(g1,g0)
    c: Coincident(g1,g0)
FEATURE [PartDesign::Pad] Pad024  label="MSH2BS_Button_"
  BaseFeature = -> Pad018
  Direction = (0,1,-2e-16)
  Length = 1.3
  Length2 = 10
  Profile = -> Sketch054
  ReferenceAxis = -> Sketch054 [N_Axis]
  Refine = true
  Suppressed = false
  Type = 0
  expr: Length = <<Spreadsheet>>.WallThickness + <<Spreadsheet>>.Tolerance
FEATURE [PartDesign::Fillet] Fillet011
  Base = -> Pad024 [Face4,Edge1,Edge9]
  BaseFeature = -> Pad024
  Radius = 1.2
  SupportTransform = false
  Suppressed = false
  UseAllEdges = false
  expr: Radius = <<Spreadsheet>>.WallThickness
FEATURE [PartDesign::Fillet] Fillet014
  Base = -> Fillet011 [Edge16]
  BaseFeature = -> Fillet011
  Radius = 1
  SupportTransform = false
  Suppressed = false
  UseAllEdges = false
FEATURE [Sketcher::SketchObject] Sketch055  label="MSH2CS_Pillar"
  ArcFitTolerance = 0
  AttachmentSupport = -> [XY_Plane010]
  ExternalGeometry = -> [Binder006]
  FullyConstrained = true
  MakeInternals = false
  MapMode = 5
  expr: Constraints[25] = <<Spreadsheet>>.Tolerance * 2
  sketch-geometry (12):
    g0: LineSegment StartX=-17.9 StartY=-12.35 StartZ=0 EndX=-15.8 EndY=-12.35 EndZ=0
    g1: LineSegment StartX=-15.8 StartY=-12.35 StartZ=0 EndX=-15.8 EndY=-10.25 EndZ=0
    g2: LineSegment StartX=-15.8 StartY=-10.25 StartZ=0 EndX=-17.9 EndY=-10.25 EndZ=0
    g3: LineSegment StartX=-17.9 StartY=-10.25 StartZ=0 EndX=-17.9 EndY=-12.35 EndZ=0
    g4: LineSegment StartX=15.8 StartY=-12.35 StartZ=0 EndX=17.9 EndY=-12.35 EndZ=0
    g5: LineSegment StartX=17.9 StartY=-12.35 StartZ=0 EndX=17.9 EndY=-10.25 EndZ=0
    g6: LineSegment StartX=17.9 StartY=-10.25 StartZ=0 EndX=15.8 EndY=-10.25 EndZ=0
    g7: LineSegment StartX=15.8 StartY=-10.25 StartZ=0 EndX=15.8 EndY=-12.35 EndZ=0
    g8: LineSegment [constr] StartX=-17.8 StartY=-12.35 StartZ=0 EndX=-17.8 EndY=-12.55 EndZ=0
    g9: LineSegment [constr] StartX=-15.8 StartY=-12.35 StartZ=0 EndX=-15.8 EndY=-12.55 EndZ=0
    g10: LineSegment [constr] StartX=15.8 StartY=-12.35 StartZ=0 EndX=15.8 EndY=-12.55 EndZ=0
    g11: LineSegment [constr] StartX=17.8 StartY=-12.55 StartZ=0 EndX=17.8 EndY=-12.35 EndZ=0
  constraints (36):
    c: PointOnObject(g1,g-6)
    c: Coincident(g1,g2)
    c: PointOnObject(g2,g-3)
    c: Coincident(g2,g3)
    c: Equal(g3,g0)
    c: Equal(g0,g1)
    c: Coincident(g4,g5)
    c: PointOnObject(g5,g-4)
    c: Coincident(g5,g6)
    c: PointOnObject(g6,g-5)
    c: Coincident(g6,g7)
    c: Coincident(g7,g4)
    c: Equal(g7,g4)
    c: Equal(g4,g5)
    c: Coincident(g0,g3)
    c: Coincident(g0,g1)
    c: PointOnObject(g0,g-3)
    c: PointOnObject(g0,g-6)
    c: PointOnObject(g8,g0)
    c: Coincident(g8,g-7)
    c: Vertical(g8)
    c: Coincident(g9,g0)
    c: PointOnObject(g9,g-7)
    c: Vertical(g9)
    c: Equal(g8,g9)
    c: DistanceY(g8,g0) = 0.2
    c: PointOnObject(g4,g-5)
    c: PointOnObject(g4,g-4)
    c: Coincident(g10,g4)
    c: Coincident(g11,g-7)
    c: PointOnObject(g11,g4)
    c: Vertical(g11)
    c: PointOnObject(g10,g-7)
    c: Vertical(g10)
    c: Equal(g9,g10)
    c: Equal(g10,g11)
FEATURE [PartDesign::Pad] Pad025  label="MSH2CS_Pillar_"
  BaseFeature = -> Pad022
  Direction = (0,0,1)
  Length = 7.1
  Length2 = 10
  Profile = -> Sketch055
  ReferenceAxis = -> Sketch055 [N_Axis]
  Refine = true
  Suppressed = false
  Type = 0
  expr: Length = <<MSH2CS_Walls_>>.Length - <<MSH2BS_Foundation>>.Length - <<Spreadsheet>>.Tolerance
FEATURE [PartDesign::Pocket] Pocket018  label="MSH2CS_Push_"
  BaseFeature = -> Pad025
  Direction = (0,1,-2e-16)
  Length = 5
  Length2 = 5
  Profile = -> Sketch053
  ReferenceAxis = -> Sketch053 [N_Axis]
  Suppressed = false
  Type = 1
FEATURE [PartDesign::Fillet] Fillet012
  Base = -> Pocket018 [Face18,Edge32,Edge28,Edge52,Edge50]
  BaseFeature = -> Pocket018
  Radius = 1
  SupportTransform = false
  Suppressed = false
  UseAllEdges = false
FEATURE [PartDesign::Pad] Pad023
  BaseFeature = -> Fillet012
  Direction = (0,-1,2e-16)
  Length = 26.85
  Length2 = 10
  Profile = -> Sketch051
  ReferenceAxis = -> Sketch051 [N_Axis]
  Refine = true
  Reversed = true
  Suppressed = false
  Type = 0
  expr: Length = Sketch040.Constraints.CoverLength
FEATURE [PartDesign::Pocket] Pocket017
  BaseFeature = -> Pad023
  Direction = (0,0,-1)
  Length = 4
  Length2 = 5
  Profile = -> Sketch052
  ReferenceAxis = -> Sketch052 [N_Axis]
  Suppressed = false
  Type = 0
  expr: Length = <<Spreadsheet>>.RidgeDepth * 2
FEATURE [PartDesign::Fillet] Fillet013
  Base = -> Pocket017 [Face40,Face43]
  BaseFeature = -> Pocket017
  Radius = 0.39
  SupportTransform = false
  Suppressed = false
  UseAllEdges = false
FEATURE [Sketcher::SketchObject] Sketch056  label="MSH2C_Pillar"
  ArcFitTolerance = 0
  AttachmentSupport = -> [XY_Plane005]
  ExternalGeometry = -> [Binder004]
  FullyConstrained = true
  MakeInternals = false
  MapMode = 5
  expr: Constraints[13] = <<Spreadsheet>>.Tolerance * 2
  sketch-geometry (9):
    g0: LineSegment StartX=-17.9 StartY=-34.35 StartZ=0 EndX=-15.8 EndY=-34.35 EndZ=0
    g1: LineSegment StartX=-15.8 StartY=-34.35 StartZ=0 EndX=-15.8 EndY=-32.25 EndZ=0
    g2: LineSegment StartX=-15.8 StartY=-32.25 StartZ=0 EndX=-17.9 EndY=-32.25 EndZ=0
    g3: LineSegment StartX=-17.9 StartY=-32.25 StartZ=0 EndX=-17.9 EndY=-34.35 EndZ=0
    g4: LineSegment [constr] StartX=-17.8 StartY=-34.55 StartZ=0 EndX=-17.8 EndY=-34.35 EndZ=0
    g5: LineSegment StartX=15.8 StartY=-34.35 StartZ=0 EndX=17.9 EndY=-34.35 EndZ=0
    g6: LineSegment StartX=17.9 StartY=-34.35 StartZ=0 EndX=17.9 EndY=-32.25 EndZ=0
    g7: LineSegment StartX=17.9 StartY=-32.25 StartZ=0 EndX=15.8 EndY=-32.25 EndZ=0
    g8: LineSegment StartX=15.8 StartY=-32.25 StartZ=0 EndX=15.8 EndY=-34.35 EndZ=0
  constraints (27):
    c: PointOnObject(g0,g-3)
    c: PointOnObject(g0,g-7)
    c: Horizontal(g0)
    c: Coincident(g1,g0)
    c: PointOnObject(g1,g-7)
    c: Coincident(g2,g1)
    c: PointOnObject(g2,g-3)
    c: Horizontal(g2)
    c: Coincident(g3,g2)
    c: Coincident(g3,g0)
    c: Coincident(g4,g-4)
    c: PointOnObject(g4,g0)
    c: Vertical(g4)
    c: DistanceY(g4,g0) = 0.2
    c: Equal(g3,g0)
    c: Coincident(g5,g6)
    c: Coincident(g6,g7)
    c: Coincident(g7,g8)
    c: Coincident(g8,g5)
    c: Horizontal(g5)
    c: Horizontal(g7)
    c: Vertical(g6)
    c: Vertical(g8)
    c: PointOnObject(g5,g-6)
    c: PointOnObject(g6,g-5)
    c: Equal(g5,g6)
    c: PointOnObject(g5,g0)
FEATURE [PartDesign::Pad] Pad026  label="MSH2C_Pillar_"
  BaseFeature = -> Pad014
  Direction = (0,0,1)
  Length = 7.1
  Length2 = 10
  Profile = -> Sketch056
  ReferenceAxis = -> Sketch056 [N_Axis]
  Refine = true
  Suppressed = false
  Type = 0
  expr: Length = <<MSH2C_Walls_>>.Length - <<MSH2B_Foundation>>.Length - <<Spreadsheet>>.Tolerance
FEATURE [PartDesign::Pocket] Pocket012  label="MSH2C_Push_"
  BaseFeature = -> Pad026
  Direction = (0,1,-2e-16)
  Length = 5
  Length2 = 5
  Profile = -> Sketch036
  ReferenceAxis = -> Sketch036 [N_Axis]
  Suppressed = false
  Type = 1
FEATURE [PartDesign::Fillet] Fillet006
  Base = -> Pocket012 [Face18,Edge50,Edge28,Edge32,Edge52]
  BaseFeature = -> Pocket012
  Radius = 1
  SupportTransform = false
  Suppressed = false
  UseAllEdges = false
FEATURE [PartDesign::Pad] Pad015
  BaseFeature = -> Fillet006
  Direction = (0,-1,2e-16)
  Length = 70.85
  Length2 = 10
  Profile = -> Sketch034
  ReferenceAxis = -> Sketch034 [N_Axis]
  Refine = true
  Reversed = true
  Suppressed = false
  Type = 0
  expr: Length = Sketch018.Constraints.CoverLength
FEATURE [PartDesign::Pocket] Pocket011
  BaseFeature = -> Pad015
  Direction = (0,0,-1)
  Length = 4
  Length2 = 5
  Profile = -> Sketch035
  ReferenceAxis = -> Sketch035 [N_Axis]
  Suppressed = false
  Type = 0
  expr: Length = <<Spreadsheet>>.RidgeDepth * 2
FEATURE [PartDesign::Fillet] Fillet007
  Base = -> Pocket011 [Face42,Edge93,Edge82,Face40]
  BaseFeature = -> Pocket011
  Radius = 0.4
  SupportTransform = false
  Suppressed = false
  UseAllEdges = false
FEATURE [PartDesign::Fillet] Fillet015
  Base = -> Fillet007 [Edge135,Edge24]
  BaseFeature = -> Fillet007
  Radius = 0.8
  SupportTransform = false
  Suppressed = false
  UseAllEdges = false
FEATURE [PartDesign::Body] Body004  label="Cap_2"
  AllowCompound = false
  Group = -> [Binder004,Binder005,Sketch032,Pad013,Sketch033,Pad014,Sketch036,Sketch056,Pad026,Pocket012,Fillet006,Sketch034,Pad015,Sketch035,Pocket011,Fillet007,Fillet015]
  Origin = -> Origin005
  Placement = pos=(0,0,18.8) rot=(0,1,0;3.14159rad)
  Tip = -> Fillet015
  expr: .Placement.Base.z = <<Spreadsheet>>.SDOffset + <<Spreadsheet>>.SDHeight + 1 mm + <<Spreadsheet>>.WallThickness
FEATURE [App::Part] Part001  label="2x"
  Group = -> [Body003,Body004]
  Origin = -> Origin007
  Placement = pos=(60,0,0) rot=(0,0,1;0rad)
FEATURE [PartDesign::Fillet] Fillet016
  Base = -> Fillet013 [Edge117,Edge8]
  BaseFeature = -> Fillet013
  Radius = 0.8
  SupportTransform = false
  Suppressed = false
  UseAllEdges = false
FEATURE [PartDesign::Body] Body007  label="Cap_short"
  AllowCompound = false
  Group = -> [Binder006,Binder007,Sketch049,Pad021,Sketch050,Pad022,Sketch053,Sketch055,Pad025,Pocket018,Fillet012,Sketch051,Pad023,Sketch052,Pocket017,Fillet013,Fillet016]
  Origin = -> Origin010
  Placement = pos=(0,0,18.8) rot=(0,1,0;3.14159rad)
  Tip = -> Fillet016
  expr: .Placement.Base.z = <<Spreadsheet>>.SDOffset + <<Spreadsheet>>.SDHeight + 1 mm + <<Spreadsheet>>.WallThickness
FEATURE [PartDesign::ShapeBinder] ShapeBinder002  label="MSH2BS_Template_SD"
  Placement = pos=(0,0,0) rot=(1,0,0;1.5708rad)
  Support = -> [Sketch019]
  TraceSupport = false
FEATURE [Sketcher::SketchObject] Sketch043  label="MSH2BS_SDHoles"
  ArcFitTolerance = 0
  AttachmentOffset = pos=(0,0,8.55) rot=(0,0,1;0rad)
  AttachmentSupport = -> [XZ_Plane009]
  ExternalGeometry = -> [ShapeBinder002]
  FullyConstrained = true
  MakeInternals = false
  MapMode = 5
  Placement = pos=(0,-8.55,1.9e-15) rot=(1,0,0;1.5708rad)
  expr: .AttachmentOffset.Base.z = Sketch040.Constraints.BaseLength / 2 - <<Spreadsheet>>.Margin
  sketch-geometry (12):
    g0: LineSegment StartX=-2.2 StartY=6.4 StartZ=0 EndX=-2.2 EndY=16.6 EndZ=0
    g1: LineSegment StartX=-2.2 StartY=16.6 StartZ=0 EndX=-13.8 EndY=16.6 EndZ=0
    g2: LineSegment StartX=-13.8 StartY=16.6 StartZ=0 EndX=-13.8 EndY=1.6 EndZ=0
    g3: LineSegment StartX=-13.8 StartY=1.6 StartZ=0 EndX=-3.3 EndY=1.6 EndZ=0
    g4: LineSegment StartX=-3.3 StartY=1.6 StartZ=0 EndX=-3.3 EndY=5.3 EndZ=0
    g5: LineSegment StartX=-3.3 StartY=5.3 StartZ=0 EndX=-2.2 EndY=6.4 EndZ=0
    g6: LineSegment StartX=2.2 StartY=16.6 StartZ=0 EndX=2.2 EndY=1.6 EndZ=0
    g7: LineSegment StartX=2.2 StartY=1.6 StartZ=0 EndX=12.7 EndY=1.6 EndZ=0
    g8: LineSegment StartX=12.7 StartY=1.6 StartZ=0 EndX=12.7 EndY=5.3 EndZ=0
    g9: LineSegment StartX=12.7 StartY=5.3 StartZ=0 EndX=13.8 EndY=6.4 EndZ=0
    g10: LineSegment StartX=13.8 StartY=6.4 StartZ=0 EndX=13.8 EndY=16.6 EndZ=0
    g11: LineSegment StartX=13.8 StartY=16.6 StartZ=0 EndX=2.2 EndY=16.6 EndZ=0
  constraints (24):
    c: Coincident(g0,g1)
    c: Coincident(g1,g2)
    c: Coincident(g2,g3)
    c: Coincident(g3,g4)
    c: Coincident(g4,g5)
    c: Coincident(g5,g0)
    c: Coincident(g6,g7)
    c: Coincident(g7,g8)
    c: Coincident(g8,g9)
    c: Coincident(g9,g10)
    c: Coincident(g10,g11)
    c: Coincident(g11,g6)
    c: Coincident(g1,g-3)
    c: Coincident(g0,g-4)
    c: Coincident(g0,g-4)
    c: Coincident(g-5,g4)
    c: Coincident(g3,g-5)
    c: Coincident(g2,g-3)
    c: Coincident(g6,g-6)
    c: Coincident(g6,g-6)
    c: Coincident(g7,g-8)
    c: Coincident(g8,g-8)
    c: Coincident(g9,g-7)
    c: Coincident(g10,g-7)
FEATURE [PartDesign::Pocket] Pocket014  label="MSH2BS_SDHoles_"
  BaseFeature = -> Fillet014
  Direction = (0,1,-2e-16)
  Length = 1.1
  Length2 = 5
  Profile = -> Sketch043
  ReferenceAxis = -> Sketch043 [N_Axis]
  Suppressed = false
  Type = 0
  expr: Length = <<Spreadsheet>>.SDHoleThickness
FEATURE [PartDesign::LinearPattern] LinearPattern002
  BaseFeature = -> Pocket014
  Direction = -> Y_Axis009
  Length = 16
  Mode = 0
  Occurrences = 5
  Offset = 4
  Originals = -> [Pocket014]
  Suppressed = false
  TransformMode = 0
  expr: Length = <<Spreadsheet>>.SpacingY * (<<Spreadsheet>>.Rows_short - 1)
  expr: Occurrences = <<Spreadsheet>>.Rows_short
FEATURE [PartDesign::Chamfer] Chamfer004
  Angle = 45
  Base = -> LinearPattern002 [Face17]
  BaseFeature = -> LinearPattern002
  ChamferType = 0
  FlipDirection = false
  Size = 0.6
  Size2 = 1
  SupportTransform = false
  Suppressed = false
  UseAllEdges = false
FEATURE [PartDesign::Pocket] Pocket016  label="MSH2BS_SDRidges_"
  BaseFeature = -> Chamfer004
  Direction = (0,1,-2e-16)
  Length = 5
  Length2 = 5
  Midplane = true
  Profile = -> Sketch048
  ReferenceAxis = -> Sketch048 [N_Axis]
  Suppressed = false
  Type = 1
FEATURE [PartDesign::Pad] Pad019  label="MSH2BS_BackWall_"
  BaseFeature = -> Pocket016
  Direction = (0,-1,2e-16)
  Length = 1.6
  Length2 = 10
  Profile = -> Sketch044
  ReferenceAxis = -> Sketch044 [N_Axis]
  Refine = true
  Suppressed = false
  Type = 0
  expr: Length = <<Spreadsheet>>.BackWallThickness
FEATURE [PartDesign::Chamfer] Chamfer005
  Angle = 50
  Base = -> Pad019 [Edge176]
  BaseFeature = -> Pad019
  ChamferType = 1
  FlipDirection = false
  Size = 0.6
  Size2 = 1.2
  SupportTransform = false
  Suppressed = false
  UseAllEdges = false
  expr: Size = (<<Spreadsheet>>.BackWallThickness - 0.4 mm) / 2
  expr: Size2 = <<Spreadsheet>>.BackWallThickness - 0.4 mm
FEATURE [PartDesign::Pocket] Pocket015  label="MSH2BS_Ridge_"
  BaseFeature = -> Chamfer005
  Direction = (0,1,-2e-16)
  Length = 5
  Length2 = 5
  Midplane = true
  Profile = -> Sketch045
  ReferenceAxis = -> Sketch045 [N_Axis]
  Suppressed = false
  Type = 1
FEATURE [PartDesign::Pad] Pad020  label="MSH2BS_Lock_"
  BaseFeature = -> Pocket015
  Direction = (0,0,1)
  Length = 4
  Length2 = 10
  Profile = -> Sketch046
  ReferenceAxis = -> Sketch046 [N_Axis]
  Suppressed = false
  Type = 0
  expr: Length = <<Spreadsheet>>.RidgeDepth * 2
FEATURE [PartDesign::Body] Body006  label="Base_short"
  AllowCompound = false
  Group = -> [ShapeBinder002,Sketch040,Sketch047,Sketch042,Pad018,DatumPlane002,Sketch054,Pad024,Fillet011,Sketch043,Fillet014,Pocket014,LinearPattern002,Sketch044,Chamfer004,Sketch048,Pocket016,Pad019,Sketch045,Chamfer005,Pocket015,Sketch046,Pad020]
  Origin = -> Origin009
  Tip = -> Pad020
FEATURE [App::Part] Part002  label="2x_Short"
  Group = -> [Body006,Body007]
  Origin = -> Origin011
  Placement = pos=(60,0,0) rot=(0,0,1;0rad)
FEATURE [Sketcher::SketchObject] Sketch057
  ArcFitTolerance = 1e-06
  AttachmentSupport = -> [XY_Plane002]
  ExternalGeometry = -> [Binder]
  FullyConstrained = true
  MakeInternals = false
  MapMode = 5
  sketch-geometry (8):
    g0: LineSegment StartX=-33.9 StartY=-34.55 StartZ=0 EndX=-31.8 EndY=-34.55 EndZ=0
    g1: LineSegment StartX=-31.8 StartY=-34.55 StartZ=0 EndX=-31.8 EndY=-32.45 EndZ=0
    g2: LineSegment StartX=-31.8 StartY=-32.45 StartZ=0 EndX=-33.9 EndY=-32.45 EndZ=0
    g3: LineSegment StartX=-33.9 StartY=-32.45 StartZ=0 EndX=-33.9 EndY=-34.55 EndZ=0
    g4: LineSegment StartX=31.8 StartY=-32.45 StartZ=0 EndX=31.8 EndY=-34.55 EndZ=0
    g5: LineSegment StartX=31.8 StartY=-34.55 StartZ=0 EndX=33.9 EndY=-34.55 EndZ=0
    g6: LineSegment StartX=33.9 StartY=-34.55 StartZ=0 EndX=33.9 EndY=-32.45 EndZ=0
    g7: LineSegment StartX=33.9 StartY=-32.45 StartZ=0 EndX=31.8 EndY=-32.45 EndZ=0
  constraints (24):
    c: Coincident(g0,g1)
    c: Coincident(g1,g2)
    c: Coincident(g2,g3)
    c: Coincident(g3,g0)
    c: Horizontal(g0)
    c: Horizontal(g2)
    c: Vertical(g1)
    c: Vertical(g3)
    c: PointOnObject(g0,g-5)
    c: PointOnObject(g1,g-4)
    c: PointOnObject(g-3,g0)
    c: Equal(g1,g2)
    c: Coincident(g4,g5)
    c: Coincident(g5,g6)
    c: Coincident(g6,g7)
    c: Coincident(g7,g4)
    c: Vertical(g4)
    c: Vertical(g6)
    c: Horizontal(g5)
    c: Horizontal(g7)
    c: PointOnObject(g5,g-6)
    c: PointOnObject(g-3,g5)
    c: PointOnObject(g4,g-7)
    c: Equal(g7,g4)
FEATURE [PartDesign::Pad] Pad027
  BaseFeature = -> Pad005
  Direction = (0,0,1)
  Length = 7.1
  Length2 = 10
  Profile = -> Sketch057
  ReferenceAxis = -> Sketch057 [N_Axis]
  Refine = true
  Suppressed = false
  Type = 0
  expr: Length = <<Pad005>>.Length - <<MSHB_Foundation_>>.Length - <<Spreadsheet>>.Tolerance
FEATURE [PartDesign::Pocket] Pocket005
  BaseFeature = -> Pad027
  Direction = (0,1,-2e-16)
  Length = 5
  Length2 = 5
  Profile = -> Sketch017
  ReferenceAxis = -> Sketch017 [N_Axis]
  Suppressed = false
  Type = 1
FEATURE [PartDesign::Fillet] Fillet002
  Base = -> Pocket005 [Edge32,Edge28,Edge50,Edge52,Face18]
  BaseFeature = -> Pocket005
  Radius = 1
  SupportTransform = false
  Suppressed = false
  UseAllEdges = false
FEATURE [PartDesign::Pad] Pad006
  BaseFeature = -> Fillet002
  Direction = (0,-1,2e-16)
  Length = 70.85
  Length2 = 10
  Profile = -> Sketch014
  ReferenceAxis = -> Sketch014 [N_Axis]
  Refine = true
  Reversed = true
  Suppressed = false
  Type = 0
  expr: Length = Sketch.Constraints.CoverLength
FEATURE [PartDesign::Pocket] Pocket003
  BaseFeature = -> Pad006
  Direction = (0,0,-1)
  Length = 4
  Length2 = 5
  Profile = -> Sketch015
  ReferenceAxis = -> Sketch015 [N_Axis]
  Suppressed = false
  Type = 0
  expr: Length = <<Spreadsheet>>.RidgeDepth * 2
FEATURE [PartDesign::Fillet] Fillet003
  Base = -> Pocket003 [Edge75,Edge71,Edge74,Edge94,Edge98,Edge97]
  BaseFeature = -> Pocket003
  Radius = 0.6
  SupportTransform = false
  Suppressed = false
  UseAllEdges = false
FEATURE [PartDesign::Body] Body002  label="Cap_4"
  AllowCompound = false
  Group = -> [Binder,Binder001,Sketch012,Pad004,Sketch013,Pad005,Sketch017,Sketch057,Pad027,Pocket005,Fillet002,Sketch014,Pad006,Sketch015,Pocket003,Fillet003]
  Origin = -> Origin002
  Placement = pos=(0,0,18.8) rot=(0,1,0;3.14159rad)
  Tip = -> Pad027
  expr: .Placement.Base.z = <<Spreadsheet>>.SDOffset + <<Spreadsheet>>.SDHeight + 1 mm + <<Spreadsheet>>.WallThickness
FEATURE [App::Part] Part  label="4x"
  Group = -> [Body,Body002]
  Origin = -> Origin006
FEATURE [Sketcher::SketchObject] Sketch058  label="MSHT_SDRidges"
  ArcFitTolerance = 0
  AttachmentSupport = -> [XZ_Plane012]
  FullyConstrained = true
  MakeInternals = false
  MapMode = 5
  Placement = pos=(0,0,0) rot=(1,0,0;1.5708rad)
  sketch-geometry (7):
    g0: ArcOfCircle CenterX=-8 CenterY=19.2444 CenterZ=0 NormalX=0 NormalY=0 NormalZ=1 AngleXU=0 Radius=9 StartAngle=4.15641 EndAngle=5.26837
    g1: ArcOfCircle CenterX=8 CenterY=19.2444 CenterZ=0 NormalX=0 NormalY=0 NormalZ=1 AngleXU=0 Radius=9 StartAngle=4.15641 EndAngle=5.26837
    g2: LineSegment StartX=-12.75 StartY=11.6 StartZ=0 EndX=-3.25 EndY=11.6 EndZ=0
    g3: LineSegment StartX=3.25 StartY=11.6 StartZ=0 EndX=12.75 EndY=11.6 EndZ=0
    g4: LineSegment [constr] StartX=-8 StartY=19.2444 StartZ=0 EndX=-8 EndY=10.2444 EndZ=0
    g5: LineSegment [constr] StartX=8 StartY=19.2444 StartZ=0 EndX=8 EndY=10.2444 EndZ=0
    g6: LineSegment [constr] StartX=-8 StartY=19.2444 StartZ=0 EndX=8 EndY=19.2444 EndZ=0
  constraints (20):
    c: Equal(g0,g1)
    c: Coincident(g2,g0)
    c: Coincident(g2,g0)
    c: Coincident(g3,g1)
    c: Coincident(g3,g1)
    c: Coincident(g4,g0)
    c: PointOnObject(g4,g0)
    c: Coincident(g5,g1)
    c: PointOnObject(g5,g1)
    c: Horizontal(g6)
    c: Radius(g0) = 9
    c: PointOnObject(g0,g-3)
    c: PointOnObject(g0,g-3)
    c: PointOnObject(g1,g-3)
    c: PointOnObject(g1,g-3)
    c: DistanceX(g-3,g0) = 1
    c: Coincident(g0,g6)
    c: Symmetric(g-5,g-4,g4)
    c: Symmetric(g-6,g-7,g5)
    c: Coincident(g6,g1)
FEATURE [Sketcher::SketchObject] Sketch061  label="MSHT_Template_XZ"
  ArcFitTolerance = 0
  AttachmentSupport = -> [XZ_Plane012]
  FullyConstrained = true
  MakeInternals = false
  MapMode = 5
  Placement = pos=(0,0,0) rot=(1,0,0;1.5708rad)
  expr: Constraints[13] = <<Spreadsheet>>.Tolerance
  expr: Constraints[26] = <<Spreadsheet>>.SDOffset + <<Spreadsheet>>.SDHeight - <<Spreadsheet>>.SDFree
  expr: Constraints[42] = <<Spreadsheet>>.RidgeOffset
  expr: Constraints[54] = <<Spreadsheet>>.RidgeDepth
  expr: Constraints[6] = <<MSHT_Template_XY>>.Constraints.Width
  sketch-geometry (28):
    g0: LineSegment StartX=-17.8 StartY=0 StartZ=0 EndX=17.8 EndY=0 EndZ=0
    g1: LineSegment StartX=17.8 StartY=11.6 StartZ=0 EndX=-17.8 EndY=11.6 EndZ=0
    g2: LineSegment [constr] StartX=-17.8 StartY=0 StartZ=0 EndX=-17.9 EndY=0 EndZ=0
    g3: LineSegment [constr] StartX=17.8 StartY=0 StartZ=0 EndX=17.9 EndY=0 EndZ=0
    g4: LineSegment StartX=-17.8 StartY=1 StartZ=0 EndX=-17.8 EndY=0 EndZ=0
    g5: LineSegment StartX=-17.8 StartY=11.6 StartZ=0 EndX=-17.8 EndY=3.42426 EndZ=0
    g6: LineSegment StartX=-17.8 StartY=3.42426 StartZ=0 EndX=-17.8 EndY=1 EndZ=0
    g7: LineSegment StartX=-17.9 StartY=0.9 StartZ=0 EndX=-16.1 EndY=0.9 EndZ=0
    g8: LineSegment StartX=-15.8172 StartY=1.58284 StartZ=0 EndX=-17.9 EndY=3.66569 EndZ=0
    g9: LineSegment StartX=17.8 StartY=0 StartZ=0 EndX=17.8 EndY=1 EndZ=0
    g10: LineSegment StartX=17.8 StartY=1 StartZ=0 EndX=17.8 EndY=11.6 EndZ=0
    g11: LineSegment StartX=17.8 StartY=1 StartZ=0 EndX=16.1 EndY=1 EndZ=0
    g12: LineSegment StartX=15.8879 StartY=1.51213 StartZ=0 EndX=17.8 EndY=3.42426 EndZ=0
    g13: LineSegment StartX=-17.8 StartY=1 StartZ=0 EndX=-16.1 EndY=1 EndZ=0
    g14: LineSegment StartX=-15.8879 StartY=1.51213 StartZ=0 EndX=-17.8 EndY=3.42426 EndZ=0
    g15: LineSegment StartX=17.9 StartY=3.66569 StartZ=0 EndX=15.8172 EndY=1.58284 EndZ=0
    g16: LineSegment StartX=16.1 StartY=0.9 StartZ=0 EndX=17.9 EndY=0.9 EndZ=0
    g17: LineSegment StartX=-17.9 StartY=0 StartZ=0 EndX=-17.9 EndY=0.9 EndZ=0
    g18: LineSegment StartX=-17.9 StartY=0.9 StartZ=0 EndX=-17.9 EndY=11.6 EndZ=0
    g19: LineSegment StartX=17.9 StartY=11.6 StartZ=0 EndX=17.9 EndY=0.9 EndZ=0
    g20: LineSegment StartX=17.9 StartY=0.9 StartZ=0 EndX=17.9 EndY=0 EndZ=0
    g21: ArcOfCircle CenterX=1.5e-15 CenterY=0 CenterZ=0 NormalX=0 NormalY=0 NormalZ=1 AngleXU=0 Radius=10 StartAngle=0 EndAngle=3.14159
    g22: ArcOfCircle CenterX=-16.1 CenterY=1.3 CenterZ=0 NormalX=0 NormalY=0 NormalZ=1 AngleXU=0 Radius=0.4 StartAngle=4.71239 EndAngle=7.06858
    g23: LineSegment [constr] StartX=-16.1 StartY=1.3 StartZ=0 EndX=-15.8 EndY=1.3 EndZ=0
    g24: LineSegment [constr] StartX=-16.1 StartY=0.9 StartZ=0 EndX=-16.1 EndY=1 EndZ=0
    g25: ArcOfCircle CenterX=-16.1 CenterY=1.3 CenterZ=0 NormalX=0 NormalY=0 NormalZ=1 AngleXU=0 Radius=0.3 StartAngle=4.71239 EndAngle=7.06858
    g26: ArcOfCircle CenterX=16.1 CenterY=1.3 CenterZ=0 NormalX=0 NormalY=0 NormalZ=1 AngleXU=0 Radius=0.3 StartAngle=2.35619 EndAngle=4.71239
    g27: ArcOfCircle CenterX=16.1 CenterY=1.3 CenterZ=0 NormalX=0 NormalY=0 NormalZ=1 AngleXU=0 Radius=0.4 StartAngle=2.35619 EndAngle=4.71239
  constraints (77):
    c: Coincident(g0,g9)
    c: Coincident(g10,g1)
    c: Coincident(g1,g5)
    c: Coincident(g4,g0)
    c: Horizontal(g0)
    c: Horizontal(g1)
    c: DistanceX(g1,g1) = 35.6
    c: Symmetric(g0,g0,g-1)  '__ANCHOR__'
    c: Coincident(g2,g0)
    c: Horizontal(g2)
    c: Coincident(g3,g0)
    c: Horizontal(g3)
    c: Equal(g3,g2)
    c: DistanceX(g2,g2) = 0.1
    c: Vertical(g4)
    c: Coincident(g5,g6)
    c: Vertical(g5)
    c: Vertical(g6)
    c: Coincident(g9,g10)
    c: Vertical(g9)
    c: Vertical(g10)
    c: Equal(g4,g9)
    c: Coincident(g9,g11)
    c: PointOnObject(g12,g10)
    c: Coincident(g2,g17)
    c: Coincident(g20,g3)
    c: DistanceY(g17,g18) = 11.6
    c: Coincident(g17,g18)
    c: Vertical(g17)
    c: Vertical(g18)
    c: Coincident(g19,g20)
    c: Vertical(g19)
    c: Vertical(g20)
    c: PointOnObject(g15,g19)
    c: Coincident(g16,g19)
    c: Equal(g20,g17)
    c: Parallel(g14,g8)
    c: PointOnObject(g21,g0)
    c: PointOnObject(g21,g0)
    c: Symmetric(g0,g0,g21)
    c: Radius(g21) = 10
    c: Horizontal(g7)
    c: DistanceY(g2,g4) = 1
    c: Tangent(g7,g22) = -1.5708
    c: Tangent(g8,g22) = -1.5708
    c: Horizontal(g13)
    c: Coincident(g4,g6)
    c: Coincident(g23,g22)
    c: Horizontal(g23)
    c: Coincident(g24,g7)
    c: Equal(g2,g24)
    c: Coincident(g25,g22)
    c: Tangent(g13,g25) = -1.5708
    c: Tangent(g14,g25) = -1.5708
    c: DistanceX(g5,g23) = 2
    c: Horizontal(g11)
    c: Horizontal(g16)
    c: Coincident(g27,g26)
    c: Tangent(g27,g16) = -1.5708
    c: Tangent(g12,g26) = 1.5708
    c: Tangent(g15,g27) = -1.5708
    c: Coincident(g13,g4)
    c: Coincident(g7,g17)
    c: Coincident(g24,g13)
    c: Radius(g22) = 0.4
    c: PointOnObject(g8,g18)
    c: PointOnObject(g23,g25)
    c: Angle(g8,g7) = 0.785398
    c: Coincident(g5,g14)
    c: Equal(g27,g22)
    c: Equal(g11,g13)
    c: Equal(g7,g16)
    c: Equal(g15,g8)
    c: Equal(g14,g12)
    c: Coincident(g26,g11)
    c: PointOnObject(g18,g1)
    c: PointOnObject(g19,g1)
FEATURE [Sketcher::SketchObject] Sketch062  label="MSHT_Ridge"
  ArcFitTolerance = 0
  AttachmentSupport = -> [XZ_Plane012]
  ExternalGeometry = -> [Sketch061]
  FullyConstrained = true
  MakeInternals = false
  MapMode = 5
  Placement = pos=(0,0,0) rot=(1,0,0;1.5708rad)
  sketch-geometry (8):
    g0: LineSegment StartX=15.8879 StartY=1.51213 StartZ=0 EndX=17.8 EndY=3.42426 EndZ=0
    g1: LineSegment StartX=17.8 StartY=3.42426 StartZ=0 EndX=17.8 EndY=1 EndZ=0
    g2: LineSegment StartX=17.8 StartY=1 StartZ=0 EndX=16.1 EndY=1 EndZ=0
    g3: LineSegment StartX=-16.1 StartY=1 StartZ=0 EndX=-17.8 EndY=1 EndZ=0
    g4: LineSegment StartX=-17.8 StartY=1 StartZ=0 EndX=-17.8 EndY=3.42426 EndZ=0
    g5: LineSegment StartX=-17.8 StartY=3.42426 StartZ=0 EndX=-15.8879 EndY=1.51213 EndZ=0
    g6: ArcOfCircle CenterX=-16.1 CenterY=1.3 CenterZ=0 NormalX=0 NormalY=0 NormalZ=1 AngleXU=0 Radius=0.3 StartAngle=4.71239 EndAngle=7.06858
    g7: ArcOfCircle CenterX=16.1 CenterY=1.3 CenterZ=0 NormalX=0 NormalY=0 NormalZ=1 AngleXU=0 Radius=0.3 StartAngle=2.35619 EndAngle=4.71239
  constraints (18):
    c: Coincident(g-8,g0)
    c: Coincident(g0,g-8)
    c: Coincident(g0,g1)
    c: Coincident(g1,g-6)
    c: Coincident(g1,g2)
    c: Coincident(g2,g-7)
    c: Coincident(g-5,g3)
    c: Coincident(g3,g-5)
    c: Coincident(g3,g4)
    c: Coincident(g4,g-3)
    c: Coincident(g4,g5)
    c: Coincident(g5,g-4)
    c: Coincident(g6,g-4)
    c: Coincident(g6,g3)
    c: Coincident(g7,g2)
    c: Coincident(g7,g0)
    c: Equal(g7,g-7)
    c: Equal(g6,g-4)
FEATURE [PartDesign::ShapeBinder] ShapeBinder003  label="MSHT_Template_SD"
  Placement = pos=(0,0,0) rot=(1,0,0;1.5708rad)
  Support = -> [Sketch019]
  TraceSupport = false
FEATURE [Sketcher::SketchObject] Sketch060  label="MSHT_SDHoles"
  ArcFitTolerance = 0
  AttachmentOffset = pos=(0,0,4.55) rot=(0,0,1;0rad)
  AttachmentSupport = -> [XZ_Plane012]
  ExternalGeometry = -> [ShapeBinder003]
  FullyConstrained = true
  MakeInternals = false
  MapMode = 5
  Placement = pos=(0,-4.55,1e-15) rot=(1,0,0;1.5708rad)
  expr: .AttachmentOffset.Base.z = Sketch063.Constraints.BaseLength / 2 - <<Spreadsheet>>.Margin
  sketch-geometry (12):
    g0: LineSegment StartX=-2.2 StartY=6.4 StartZ=0 EndX=-2.2 EndY=16.6 EndZ=0
    g1: LineSegment StartX=-2.2 StartY=16.6 StartZ=0 EndX=-13.8 EndY=16.6 EndZ=0
    g2: LineSegment StartX=-13.8 StartY=16.6 StartZ=0 EndX=-13.8 EndY=1.6 EndZ=0
    g3: LineSegment StartX=-13.8 StartY=1.6 StartZ=0 EndX=-3.3 EndY=1.6 EndZ=0
    g4: LineSegment StartX=-3.3 StartY=1.6 StartZ=0 EndX=-3.3 EndY=5.3 EndZ=0
    g5: LineSegment StartX=-3.3 StartY=5.3 StartZ=0 EndX=-2.2 EndY=6.4 EndZ=0
    g6: LineSegment StartX=2.2 StartY=16.6 StartZ=0 EndX=2.2 EndY=1.6 EndZ=0
    g7: LineSegment StartX=2.2 StartY=1.6 StartZ=0 EndX=12.7 EndY=1.6 EndZ=0
    g8: LineSegment StartX=12.7 StartY=1.6 StartZ=0 EndX=12.7 EndY=5.3 EndZ=0
    g9: LineSegment StartX=12.7 StartY=5.3 StartZ=0 EndX=13.8 EndY=6.4 EndZ=0
    g10: LineSegment StartX=13.8 StartY=6.4 StartZ=0 EndX=13.8 EndY=16.6 EndZ=0
    g11: LineSegment StartX=13.8 StartY=16.6 StartZ=0 EndX=2.2 EndY=16.6 EndZ=0
  constraints (24):
    c: Coincident(g0,g1)
    c: Coincident(g1,g2)
    c: Coincident(g2,g3)
    c: Coincident(g3,g4)
    c: Coincident(g4,g5)
    c: Coincident(g5,g0)
    c: Coincident(g6,g7)
    c: Coincident(g7,g8)
    c: Coincident(g8,g9)
    c: Coincident(g9,g10)
    c: Coincident(g10,g11)
    c: Coincident(g11,g6)
    c: Coincident(g1,g-3)
    c: Coincident(g0,g-4)
    c: Coincident(g0,g-4)
    c: Coincident(g-5,g4)
    c: Coincident(g3,g-5)
    c: Coincident(g2,g-3)
    c: Coincident(g6,g-6)
    c: Coincident(g6,g-6)
    c: Coincident(g7,g-8)
    c: Coincident(g8,g-8)
    c: Coincident(g9,g-7)
    c: Coincident(g10,g-7)
FEATURE [Sketcher::SketchObject] Sketch063  label="MSHT_Template_XY"
  ArcFitTolerance = 0
  AttachmentSupport = -> [XY_Plane012]
  FullyConstrained = true
  MakeInternals = false
  MapMode = 5
  expr: .Constraints.BaseLength = <<Spreadsheet>>.SpacingY * (<<Spreadsheet>>.Rows_test - 1) + <<Spreadsheet>>.SDHoleThickness + 2 * <<Spreadsheet>>.Margin
  expr: .Constraints.Width = <<Spreadsheet>>.SpacingX * (<<Spreadsheet>>.Columns_2 - 1) + <<Spreadsheet>>.SDHoleWidth + 2 * <<Spreadsheet>>.Margin
  expr: Constraints[34] = <<Spreadsheet>>.LockRadius
  expr: Constraints[35] = <<Spreadsheet>>.LockRadius + <<Spreadsheet>>.Tolerance
  expr: Constraints[41] = <<Spreadsheet>>.RidgeDepth
  sketch-geometry (15):
    g0: LineSegment StartX=17.8 StartY=8.55 StartZ=0 EndX=17.8 EndY=-8.55 EndZ=0
    g1: LineSegment StartX=-17.8 StartY=-8.55 StartZ=0 EndX=-17.8 EndY=8.55 EndZ=0
    g2: LineSegment StartX=-17.8 StartY=1e-16 StartZ=0 EndX=17.8 EndY=1e-16 EndZ=0
    g3: LineSegment StartX=4e-16 StartY=8.55 StartZ=0 EndX=1e-16 EndY=-8.55 EndZ=0
    g4: LineSegment StartX=-17.8 StartY=8.55 StartZ=0 EndX=-15.8 EndY=8.55 EndZ=0
    g5: LineSegment StartX=-15.8 StartY=8.55 StartZ=0 EndX=15.8 EndY=8.55 EndZ=0
    g6: ArcOfCircle CenterX=-15.8 CenterY=-4.95 CenterZ=0 NormalX=0 NormalY=0 NormalZ=1 AngleXU=0 Radius=1.6 StartAngle=1.5708 EndAngle=4.71239
    g7: LineSegment StartX=-15.8 StartY=-8.55 StartZ=0 EndX=-15.8 EndY=8.55 EndZ=0
    g8: ArcOfCircle CenterX=-15.8 CenterY=-4.95 CenterZ=0 NormalX=0 NormalY=0 NormalZ=1 AngleXU=0 Radius=1.7 StartAngle=1.5708 EndAngle=4.71239
    g9: LineSegment StartX=15.8 StartY=8.55 StartZ=0 EndX=15.8 EndY=-8.55 EndZ=0
    g10: ArcOfCircle CenterX=15.8 CenterY=-4.95 CenterZ=0 NormalX=0 NormalY=0 NormalZ=1 AngleXU=0 Radius=1.6 StartAngle=4.71239 EndAngle=7.85398
    g11: ArcOfCircle CenterX=15.8 CenterY=-4.95 CenterZ=0 NormalX=0 NormalY=0 NormalZ=1 AngleXU=0 Radius=1.7 StartAngle=4.71239 EndAngle=7.85398
    g12: LineSegment [constr] StartX=-15.8 StartY=-4.95 StartZ=0 EndX=15.8 EndY=-4.95 EndZ=0
    g13: LineSegment StartX=15.8 StartY=8.55 StartZ=0 EndX=17.8 EndY=8.55 EndZ=0
    g14: LineSegment StartX=-17.8 StartY=-8.55 StartZ=0 EndX=17.8 EndY=-8.55 EndZ=0
  constraints (47):
    c: Coincident(g1,g4)
    c: Vertical(g0)
    c: Vertical(g1)
    c: DistanceX(g4,g0) = 35.6  'Width'
    c: PointOnObject(g2,g1)
    c: Coincident(g4,g5)
    c: Horizontal(g4)
    c: PointOnObject(g3,g5)
    c: Coincident(g7,g4)
    c: Vertical(g7)
    c: PointOnObject(g6,g7)
    c: PointOnObject(g6,g7)
    c: Coincident(g8,g6)
    c: PointOnObject(g8,g7)
    c: Vertical(g9)
    c: PointOnObject(g10,g9)
    c: PointOnObject(g10,g9)
    c: Coincident(g11,g10)
    c: PointOnObject(g11,g9)
    c: Equal(g6,g10)
    c: Equal(g11,g8)
    c: PointOnObject(g8,g7)
    c: PointOnObject(g6,g7)
    c: DistanceY(g7,g6) = 2
    c: PointOnObject(g11,g9)
    c: PointOnObject(g10,g9)
    c: Coincident(g12,g6)
    c: Coincident(g12,g10)
    c: Horizontal(g12)
    c: Coincident(g5,g9)
    c: Coincident(g13,g5)
    c: Coincident(g13,g0)
    c: Horizontal(g13)
    c: Symmetric(g4,g5,g3)
    c: Radius(g6) = 1.6
    c: Radius(g8) = 1.7
    c: Horizontal(g14)
    c: Symmetric(g14,g0,g-1)  '__ANCHOR__'
    c: DistanceY(g14,g1) = 17.1  'BaseLength'
    c: Symmetric(g14,g0,g2)
    c: Horizontal(g2)
    c: DistanceX(g1,g7) = 2
    c: PointOnObject(g7,g14)
    c: Coincident(g0,g14)
    c: Coincident(g1,g14)
    c: Symmetric(g7,g9,g3)
    c: Symmetric(g1,g0,g3)
FEATURE [Sketcher::SketchObject] Sketch064  label="MSHT_Lock"
  ArcFitTolerance = 0
  AttachmentOffset = pos=(0,0,1) rot=(0,0,1;0rad)
  AttachmentSupport = -> [XY_Plane012]
  ExternalGeometry = -> [Sketch063]
  FullyConstrained = true
  MakeInternals = false
  MapMode = 5
  Placement = pos=(0,0,1) rot=(0,0,1;0rad)
  expr: .AttachmentOffset.Base.z = <<Spreadsheet>>.RidgeOffset
  sketch-geometry (4):
    g0: ArcOfCircle CenterX=-15.8 CenterY=-4.95 CenterZ=0 NormalX=0 NormalY=0 NormalZ=1 AngleXU=0 Radius=1.6 StartAngle=1.5708 EndAngle=4.71239
    g1: ArcOfCircle CenterX=15.8 CenterY=-4.95 CenterZ=0 NormalX=0 NormalY=0 NormalZ=1 AngleXU=0 Radius=1.6 StartAngle=4.71239 EndAngle=7.85398
    g2: LineSegment StartX=15.8 StartY=-3.35 StartZ=0 EndX=15.8 EndY=-6.55 EndZ=0
    g3: LineSegment StartX=-15.8 StartY=-3.35 StartZ=0 EndX=-15.8 EndY=-6.55 EndZ=0
  constraints (10):
    c: Coincident(g2,g1)
    c: Coincident(g2,g1)
    c: Coincident(g3,g0)
    c: Coincident(g3,g0)
    c: Coincident(g1,g-4)
    c: Coincident(g1,g-4)
    c: Equal(g1,g-4)
    c: Coincident(g0,g-3)
    c: Coincident(g0,g-3)
    c: Equal(g0,g-3)
FEATURE [Sketcher::SketchObject] Sketch066  label="MSHT_Foundation"
  ArcFitTolerance = 0
  AttachmentSupport = -> [XY_Plane012]
  ExternalGeometry = -> [Sketch063]
  FullyConstrained = true
  MakeInternals = false
  MapMode = 5
  sketch-geometry (4):
    g0: LineSegment StartX=17.8 StartY=8.55 StartZ=0 EndX=17.8 EndY=-8.55 EndZ=0
    g1: LineSegment StartX=17.8 StartY=-8.55 StartZ=0 EndX=-17.8 EndY=-8.55 EndZ=0
    g2: LineSegment StartX=-17.8 StartY=-8.55 StartZ=0 EndX=-17.8 EndY=8.55 EndZ=0
    g3: LineSegment StartX=-17.8 StartY=8.55 StartZ=0 EndX=17.8 EndY=8.55 EndZ=0
  constraints (8):
    c: Coincident(g0,g1)
    c: Coincident(g1,g2)
    c: Coincident(g2,g3)
    c: Coincident(g3,g0)
    c: Coincident(g0,g-4)
    c: Coincident(g0,g-4)
    c: Coincident(g2,g-3)
    c: Coincident(g1,g-3)
FEATURE [PartDesign::Pad] Pad028  label="MSHT_Foundation_"
  Direction = (0,0,1)
  Length = 11.6
  Length2 = 10
  Profile = -> Sketch066
  ReferenceAxis = -> Sketch066 [N_Axis]
  Suppressed = false
  Type = 0
  expr: Length = <<Spreadsheet>>.BaseHeight
FEATURE [PartDesign::Plane] DatumPlane003
  AttachmentSupport = -> [Sketch063]
  Length = 60
  MapMode = 7
  Placement = pos=(17.8,8.55,0) rot=(0,0.707107,0.707107;3.14159rad)
  ResizeMode = 0
  Width = 60
FEATURE [Sketcher::SketchObject] Sketch065  label="MSHT_Button"
  ArcFitTolerance = 0
  AttachmentSupport = -> [DatumPlane003]
  ExternalGeometry = -> [Sketch061]
  FullyConstrained = true
  MakeInternals = false
  MapMode = 5
  Placement = pos=(17.8,8.55,0) rot=(0,0.707107,0.707107;3.14159rad)
  sketch-geometry (2):
    g0: ArcOfCircle CenterX=17.8 CenterY=-2.04825e-05 CenterZ=0 NormalX=0 NormalY=0 NormalZ=1 AngleXU=0 Radius=10 StartAngle=2.04825e-06 EndAngle=3.14159
    g1: LineSegment StartX=7.8 StartY=-7e-16 StartZ=0 EndX=27.8 EndY=-1.8e-15 EndZ=0
  constraints (5):
    c: Coincident(g0,g-3)
    c: Coincident(g0,g-3)
    c: Equal(g0,g-3)
    c: Coincident(g1,g0)
    c: Coincident(g1,g0)
FEATURE [PartDesign::Pad] Pad029  label="MSH2T_Button_"
  BaseFeature = -> Pad028
  Direction = (0,1,-2e-16)
  Length = 1.3
  Length2 = 10
  Profile = -> Sketch065
  ReferenceAxis = -> Sketch065 [N_Axis]
  Refine = true
  Suppressed = false
  Type = 0
  expr: Length = <<Spreadsheet>>.WallThickness + <<Spreadsheet>>.Tolerance
FEATURE [PartDesign::Fillet] Fillet017
  Base = -> Pad029 [Face4,Edge1,Edge9,Edge2,Edge10]
  BaseFeature = -> Pad029
  Radius = 1.2
  SupportTransform = false
  Suppressed = false
  UseAllEdges = false
  expr: Radius = <<Spreadsheet>>.WallThickness
FEATURE [PartDesign::Fillet] Fillet018
  Base = -> Fillet017 [Edge11]
  BaseFeature = -> Fillet017
  Radius = 1
  SupportTransform = false
  Suppressed = false
  UseAllEdges = false
FEATURE [PartDesign::Pocket] Pocket021  label="MSHT_SDHoles_"
  BaseFeature = -> Fillet018
  Direction = (0,1,-2e-16)
  Length = 1.1
  Length2 = 5
  Profile = -> Sketch060
  ReferenceAxis = -> Sketch060 [N_Axis]
  Suppressed = false
  Type = 0
  expr: Length = <<Spreadsheet>>.SDHoleThickness
FEATURE [PartDesign::LinearPattern] LinearPattern003
  BaseFeature = -> Pocket021
  Direction = -> Y_Axis012
  Length = 8
  Mode = 0
  Occurrences = 3
  Offset = 4
  Originals = -> [Pocket021]
  Suppressed = false
  TransformMode = 0
  expr: Length = <<Spreadsheet>>.SpacingY * (<<Spreadsheet>>.Rows_test - 1)
  expr: Occurrences = <<Spreadsheet>>.Rows_test
FEATURE [PartDesign::Chamfer] Chamfer006
  Angle = 45
  Base = -> LinearPattern003 [Face21]
  BaseFeature = -> LinearPattern003
  ChamferType = 0
  FlipDirection = false
  Size = 0.6
  Size2 = 1
  SupportTransform = false
  Suppressed = false
  UseAllEdges = false
FEATURE [PartDesign::Pocket] Pocket020  label="MSHT_SDRidges_"
  BaseFeature = -> Chamfer006
  Direction = (0,1,-2e-16)
  Length = 5
  Length2 = 5
  Midplane = true
  Profile = -> Sketch058
  ReferenceAxis = -> Sketch058 [N_Axis]
  Suppressed = false
  Type = 1
FEATURE [PartDesign::Pocket] Pocket019  label="MSHT_Ridge_"
  BaseFeature = -> Pocket020
  Direction = (0,1,-2e-16)
  Length = 5
  Length2 = 5
  Midplane = true
  Profile = -> Sketch062
  ReferenceAxis = -> Sketch062 [N_Axis]
  Suppressed = false
  Type = 1
FEATURE [PartDesign::Pad] Pad031  label="MSH_Lock_"
  BaseFeature = -> Pocket019
  Direction = (0,0,1)
  Length = 4
  Length2 = 10
  Profile = -> Sketch064
  ReferenceAxis = -> Sketch064 [N_Axis]
  Suppressed = false
  Type = 0
  expr: Length = <<Spreadsheet>>.RidgeDepth * 2
FEATURE [PartDesign::Body] Body008  label="Test"
  AllowCompound = false
  Group = -> [ShapeBinder003,Sketch063,Sketch061,Sketch066,Pad028,DatumPlane003,Sketch065,Pad029,Fillet017,Sketch060,Fillet018,Pocket021,LinearPattern003,Chamfer006,Sketch058,Pocket020,Sketch062,Pocket019,Sketch064,Pad031]
  Origin = -> Origin012
  Tip = -> Pad031
